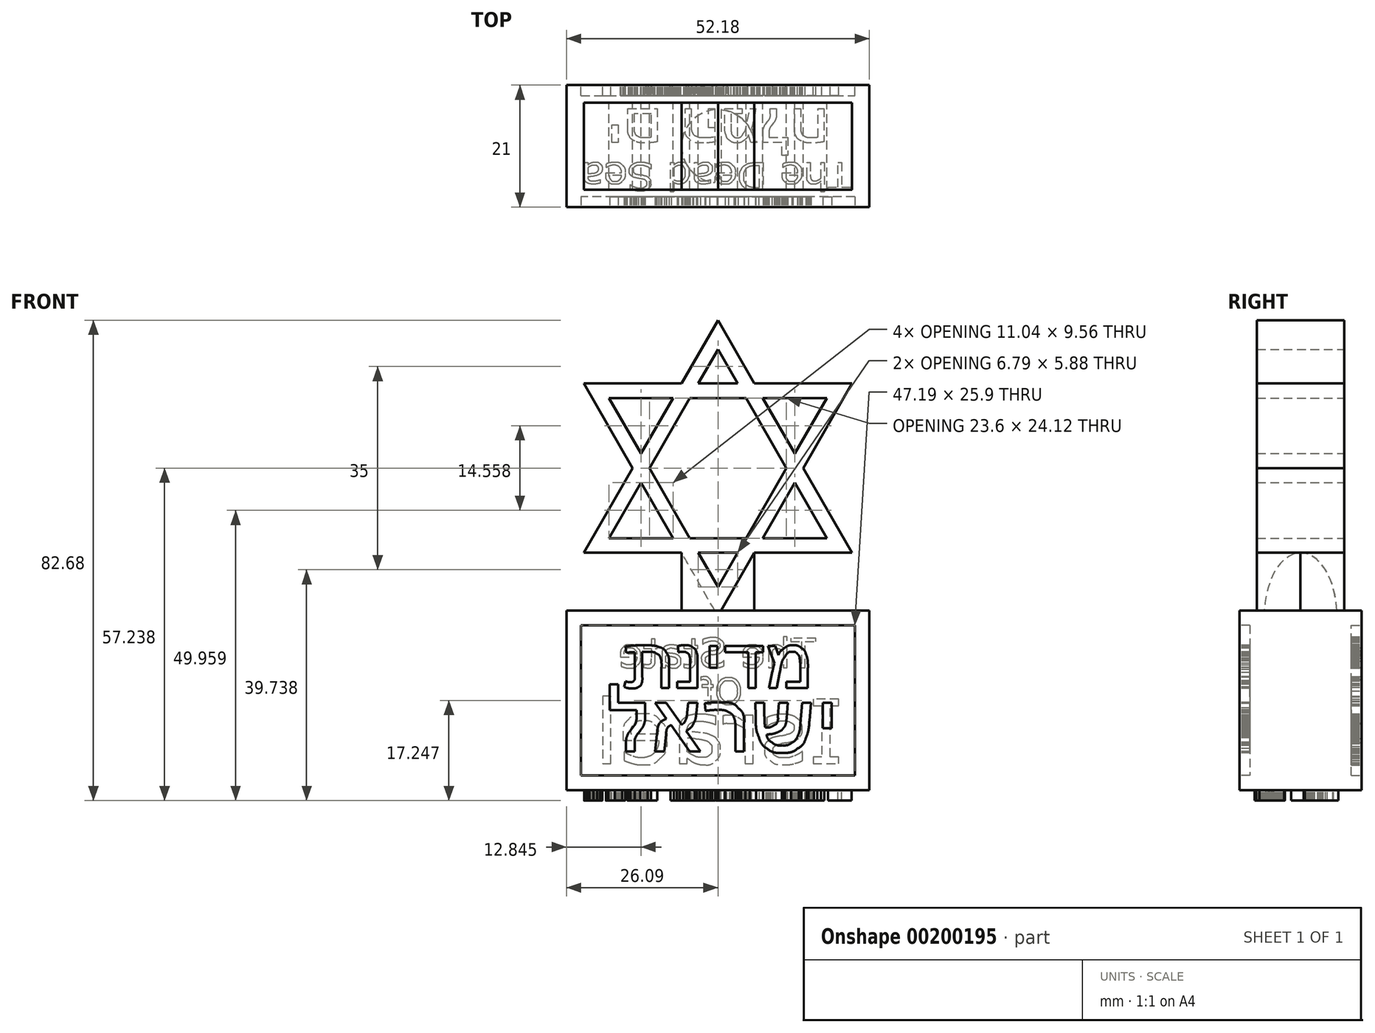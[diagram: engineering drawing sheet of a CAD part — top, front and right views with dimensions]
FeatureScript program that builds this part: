
annotation { "Feature Type Name" : "Feature", "Feature Type Description" : "" }
export const myFeature = defineFeature(function(context is Context, id is Id, definition is map)
    precondition{}
    {
        {
            var Q0;
            Q0=qCreatedBy(makeId("Front.planeOp"),FACE);
            var sketch = newSketch(context, id + "F0", { "sketchPlane" : qUnion([Q0])});
            skLineSegment(sketch, "E0", {"start": v(0, 0) * mm, "end": v(6.28, -10.88) * mm});
            skLineSegment(sketch, "E1", {"start": v(23.1, -40) * mm, "end": v(6.28, -40) * mm});
            skLineSegment(sketch, "E2", {"start": v(0, 0) * mm, "end": v(-6.28, -10.88) * mm});
            skLineSegment(sketch, "E3.0", {"start": v(0, -5) * mm, "end": v(-3.4, -10.88) * mm});
            skLineSegment(sketch, "E3.1", {"start": v(0, -5) * mm, "end": v(3.4, -10.88) * mm});
            skLineSegment(sketch, "E3.2", {"start": v(18.76, -37.5) * mm, "end": v(7.73, -37.5) * mm});
            skLineSegment(sketch, "E4", {"start": v(0, 0) * mm, "end": v(0, -40) * mm, "construction": true});
            skPoint(sketch, "E5", {"position": v(0, -20) * mm});
            skPoint(sketch, "E6", {"position": v(0, -10.88) * mm});
            skLineSegment(sketch, "E7", {"start": v(0, -10.88) * mm, "end": v(3.4, -10.88) * mm});
            skLineSegment(sketch, "E8", {"start": v(0, -40) * mm, "end": v(0, -57.57) * mm, "construction": true});
            skPoint(sketch, "E9", {"position": v(0, -50.88) * mm});
            skLineSegment(sketch, "E10", {"start": v(23.1, -10.88) * mm, "end": v(14.69, -25.44) * mm});
            skLineSegment(sketch, "E11", {"start": v(0, -10.88) * mm, "end": v(-3.4, -10.88) * mm});
            skLineSegment(sketch, "E12", {"start": v(-23.1, -10.88) * mm, "end": v(-14.69, -25.44) * mm});
            skLineSegment(sketch, "E13.0", {"start": v(18.76, -13.38) * mm, "end": v(13.25, -22.94) * mm});
            skLineSegment(sketch, "E14.0", {"start": v(11.19, -13.38) * mm, "end": v(18.76, -13.38) * mm});
            skLineSegment(sketch, "E14.1", {"start": v(11.19, -13.38) * mm, "end": v(7.73, -13.38) * mm});
            skLineSegment(sketch, "E15", {"start": v(-11.9, -13.38) * mm, "end": v(-18.76, -13.38) * mm});
            skLineSegment(sketch, "E16.trimOffspring", {"start": v(-18.76, -13.38) * mm, "end": v(-13.25, -22.94) * mm});
            skLineSegment(sketch, "E17.trimOffspring", {"start": v(4.84, -13.38) * mm, "end": v(11.8, -25.44) * mm});
            skLineSegment(sketch, "E18.trimOffspring", {"start": v(6.28, -10.88) * mm, "end": v(23.1, -10.88) * mm});
            skLineSegment(sketch, "E19.trimOffspring", {"start": v(7.73, -13.38) * mm, "end": v(13.25, -22.94) * mm});
            skLineSegment(sketch, "E20.trimOffspring", {"start": v(4.84, -13.38) * mm, "end": v(-4.84, -13.38) * mm});
            skLineSegment(sketch, "E21.trimOffspring", {"start": v(11.8, -25.44) * mm, "end": v(4.84, -37.5) * mm});
            skLineSegment(sketch, "E22.trimOffspring", {"start": v(14.69, -25.44) * mm, "end": v(23.1, -40) * mm});
            skLineSegment(sketch, "E23.trimOffspring", {"start": v(13.25, -27.94) * mm, "end": v(18.76, -37.5) * mm});
            skLineSegment(sketch, "E24.trimOffspring", {"start": v(13.25, -27.94) * mm, "end": v(7.73, -37.5) * mm});
            skLineSegment(sketch, "E25.trimOffspring", {"start": v(-7.73, -13.38) * mm, "end": v(-13.25, -22.94) * mm});
            skLineSegment(sketch, "E26.trimOffspring", {"start": v(-6.28, -10.88) * mm, "end": v(-23.1, -10.88) * mm});
            skLineSegment(sketch, "E27.trimOffspring", {"start": v(-4.84, -13.38) * mm, "end": v(-11.8, -25.44) * mm});
            skLineSegment(sketch, "E28.trimOffspring", {"start": v(-7.73, -13.38) * mm, "end": v(-11.9, -13.38) * mm});
            skLineSegment(sketch, "E29.trimOffspring", {"start": v(-14.69, -25.44) * mm, "end": v(-23.1, -40) * mm});
            skLineSegment(sketch, "E30.trimOffspring", {"start": v(-13.25, -27.94) * mm, "end": v(-18.76, -37.5) * mm});
            skLineSegment(sketch, "E31.trimOffspring", {"start": v(-13.25, -27.94) * mm, "end": v(-7.73, -37.5) * mm});
            skLineSegment(sketch, "E32.trimOffspring", {"start": v(-11.8, -25.44) * mm, "end": v(-4.84, -37.5) * mm});
            skLineSegment(sketch, "E33.trimOffspring", {"start": v(-6.28, -40) * mm, "end": v(0, -50.88) * mm});
            skLineSegment(sketch, "E34.trimOffspring", {"start": v(-7.73, -37.5) * mm, "end": v(-18.76, -37.5) * mm});
            skLineSegment(sketch, "E35.trimOffspring", {"start": v(-3.4, -40) * mm, "end": v(0, -45.88) * mm});
            skLineSegment(sketch, "E36.trimOffspring", {"start": v(-6.28, -40) * mm, "end": v(-23.1, -40) * mm});
            skLineSegment(sketch, "E37.trimOffspring", {"start": v(3.4, -40) * mm, "end": v(0, -45.88) * mm});
            skLineSegment(sketch, "E38.trimOffspring", {"start": v(4.84, -37.5) * mm, "end": v(-4.84, -37.5) * mm});
            skLineSegment(sketch, "E39.trimOffspring", {"start": v(6.28, -40) * mm, "end": v(0, -50.88) * mm});
            skLineSegment(sketch, "E40.trimOffspring", {"start": v(3.4, -40) * mm, "end": v(-3.4, -40) * mm});
            skSolve(sketch);
        }
        {
            var Q0;
            Q0=makeQuery(id+"F0.imprint","IMPRINT",FACE,{"disambiguationData":[TD([[makeQuery(id+"F0.imprint","IMPRINT",EDGE,{"derivedFrom":sQuery(id+"F0.wireOp",EDGE,"E0")}),-1.0]])]});
            extrude(context, id + "F1", {"entities" : qUnion([Q0]), "depth" : 15 * mm});
        }
        {
            var Q0;
            Q0=makeQuery(id+"F1.opExtrude","SWEPT_EDGE",EDGE,{"disambiguationData":[OSD([sQuery(id+"F0.wireOp",EDGE,"E33.trimOffspring"),sQuery(id+"F0.wireOp",EDGE,"E39.trimOffspring")])]});
            cPlane(context, id + "F2", {"entities" : qUnion([Q0]), "cplaneType" : CPlaneType.LINE_ANGLE, "offset" : 25 * mm, "angle" : 0 * degree, "width" : 150 * mm, "height" : 150 * mm});
        }
        {
            var Q0;
            Q0=qCreatedBy(id+"F2.planeOp",FACE);
            var sketch = newSketch(context, id + "F3", { "sketchPlane" : qUnion([Q0])});
            skLineSegment(sketch, "E41.0", {"start": v(-6.28, -15) * mm, "end": v(-6.28, 0) * mm});
            skLineSegment(sketch, "E42.0", {"start": v(0, -15) * mm, "end": v(0, 0) * mm});
            skLineSegment(sketch, "E43.0", {"start": v(6.28, -15) * mm, "end": v(6.28, 0) * mm});
            skLineSegment(sketch, "E44.0", {"start": v(6.28, 0) * mm, "end": v(0, 0) * mm});
            skLineSegment(sketch, "E45.0", {"start": v(-6.28, 0) * mm, "end": v(0, 0) * mm});
            skLineSegment(sketch, "E46.0", {"start": v(-6.28, -15) * mm, "end": v(0, -15) * mm});
            skLineSegment(sketch, "E47.0", {"start": v(6.28, -15) * mm, "end": v(0, -15) * mm});
            skPoint(sketch, "E48", {"position": v(0, -7.5) * mm});
            skCircle(sketch, "E49", {"center": v(0, -7.5) * mm, "radius": 6.28 * mm});
            skSolve(sketch);
        }
        {
            var Q0;
            {var subQ0=sQuery(id+"F3.wireOp",EDGE,"E49");var subQ1=sQuery(id+"F3.wireOp",EDGE,"E42.0");var subQ2=makeQuery(id+"F3.imprint","INTERSECT",VERTEX,{"disambiguationData":[OD(0.0)],"derivedFrom":[subQ1,subQ0]});Q0=makeQuery(id+"F3.imprint","IMPRINT",FACE,{"disambiguationData":[TD([[makeQuery(id+"F3.imprint","IMPRINT",EDGE,{"disambiguationData":[TD([[subQ2,-1.0]])],"derivedFrom":subQ1}),1.0]])]});}
            var Q1;
            Q1=makeQuery(id+"F1.opExtrude","SWEPT_FACE",FACE,{"disambiguationData":[OSD([sQuery(id+"F0.wireOp",EDGE,"E33.trimOffspring")])]});
            extrude(context, id + "F4", {"entities" : qUnion([Q0]), "operationType" : NewBodyOperationType.ADD, "endBound" : BoundingType.UP_TO_SURFACE, "endBoundEntityFace" : qUnion([Q1]), "depth" : 25 * mm});
        }
        {
            var Q0;
            {var subQ0=sQuery(id+"F3.wireOp",EDGE,"E49");var subQ1=sQuery(id+"F3.wireOp",EDGE,"E42.0");var subQ2=makeQuery(id+"F3.imprint","INTERSECT",VERTEX,{"disambiguationData":[OD(0.0)],"derivedFrom":[subQ1,subQ0]});Q0=makeQuery(id+"F3.imprint","IMPRINT",FACE,{"disambiguationData":[TD([[makeQuery(id+"F3.imprint","IMPRINT",EDGE,{"disambiguationData":[TD([[subQ2,-1.0]])],"derivedFrom":subQ1}),-1.0]])]});}
            var Q1;
            Q1=makeQuery(id+"F1.opExtrude","SWEPT_FACE",FACE,{"disambiguationData":[OSD([sQuery(id+"F0.wireOp",EDGE,"E39.trimOffspring")])]});
            extrude(context, id + "F5", {"entities" : qUnion([Q0]), "operationType" : NewBodyOperationType.ADD, "endBound" : BoundingType.UP_TO_SURFACE, "endBoundEntityFace" : qUnion([Q1]), "depth" : 25 * mm});
        }
        {
            var Q0;
            Q0=qCreatedBy(id+"F2.planeOp",FACE);
            var sketch = newSketch(context, id + "F6", { "sketchPlane" : qUnion([Q0])});
            skLineSegment(sketch, "E50.0", {"start": v(-6.28, 3) * mm, "end": v(-26.1, 3) * mm});
            skLineSegment(sketch, "E50.1", {"start": v(-26.1, -18) * mm, "end": v(-26.1, 3) * mm});
            skLineSegment(sketch, "E50.2", {"start": v(-6.28, -18) * mm, "end": v(-26.1, -18) * mm});
            skLineSegment(sketch, "E51.0", {"start": v(26.1, -18) * mm, "end": v(6.28, -18) * mm});
            skLineSegment(sketch, "E51.1", {"start": v(26.1, -18) * mm, "end": v(26.1, 3) * mm});
            skLineSegment(sketch, "E51.2", {"start": v(26.1, 3) * mm, "end": v(6.28, 3) * mm});
            skLineSegment(sketch, "E52", {"start": v(-6.28, -18) * mm, "end": v(6.28, -18) * mm});
            skLineSegment(sketch, "E53", {"start": v(6.28, 3) * mm, "end": v(-6.28, 3) * mm});
            skPoint(sketch, "E54.0.start.orphan", {"position": v(-6.28, -15) * mm});
            skPoint(sketch, "E55.0.start.orphan", {"position": v(-23.1, -15) * mm});
            skPoint(sketch, "E56.0.end.orphan", {"position": v(-23.1, 0) * mm});
            skPoint(sketch, "E56.0.start.orphan", {"position": v(-6.28, 0) * mm});
            skPoint(sketch, "E57.0.end.orphan", {"position": v(6.28, 0) * mm});
            skPoint(sketch, "E58.0.end.orphan", {"position": v(6.28, -15) * mm});
            skPoint(sketch, "E59.0.end.orphan", {"position": v(23.1, 0) * mm});
            skPoint(sketch, "E59.0.start.orphan", {"position": v(23.1, -15) * mm});
            skSolve(sketch);
        }
        {
            var Q0;
            Q0=qCreatedBy(id+"F2.planeOp",FACE);
            cPlane(context, id + "F7", {"entities" : qUnion([Q0]), "cplaneType" : CPlaneType.OFFSET, "offset" : 30 * mm, "oppositeDirection" : true, "width" : 150 * mm, "height" : 150 * mm});
        }
        {
            var Q0;
            Q0=qCreatedBy(id+"F7.planeOp",FACE);
            var sketch = newSketch(context, id + "F8", { "sketchPlane" : qUnion([Q0])});
            skLineSegment(sketch, "E60.0", {"start": v(-6.28, 3) * mm, "end": v(-26.1, 3) * mm});
            skLineSegment(sketch, "E61.0", {"start": v(-26.1, -18) * mm, "end": v(-26.1, 3) * mm});
            skLineSegment(sketch, "E62.0", {"start": v(6.28, 3) * mm, "end": v(-6.28, 3) * mm});
            skLineSegment(sketch, "E63.0", {"start": v(-6.28, -18) * mm, "end": v(6.28, -18) * mm});
            skLineSegment(sketch, "E64.0", {"start": v(26.1, -18) * mm, "end": v(6.28, -18) * mm});
            skLineSegment(sketch, "E65.0", {"start": v(26.1, -18) * mm, "end": v(26.1, 3) * mm});
            skLineSegment(sketch, "E66.0", {"start": v(26.1, 3) * mm, "end": v(6.28, 3) * mm});
            skLineSegment(sketch, "E67.0", {"start": v(-6.28, -18) * mm, "end": v(-26.1, -18) * mm});
            skSolve(sketch);
        }
        {
            var Q0;
            Q0 = qSketchRegion(id + "F8", true);
            extrude(context, id + "F9", {"entities" : qUnion([Q0]), "operationType" : NewBodyOperationType.ADD, "depth" : 30.9 * mm});
        }
        {
            var Q0;
            Q0=makeQuery(id+"F9.opExtrude","SWEPT_FACE",FACE,{"disambiguationData":[OSD([sQuery(id+"F8.wireOp",EDGE,"E63.0"),sQuery(id+"F8.wireOp",EDGE,"E64.0"),sQuery(id+"F8.wireOp",EDGE,"E67.0")])]});
            var sketch = newSketch(context, id + "F10", { "sketchPlane" : qUnion([Q0])});
            skLineSegment(sketch, "E68.0", {"start": v(26.1, -49.98) * mm, "end": v(-26.1, -49.98) * mm});
            skLineSegment(sketch, "E69.0", {"start": v(-26.1, -49.98) * mm, "end": v(-26.1, -80.88) * mm});
            skLineSegment(sketch, "E70.0", {"start": v(26.1, -49.98) * mm, "end": v(26.1, -80.88) * mm});
            skLineSegment(sketch, "E71.0", {"start": v(26.1, -80.88) * mm, "end": v(-26.1, -80.88) * mm});
            skLineSegment(sketch, "E72.0", {"start": v(23.6, -52.48) * mm, "end": v(-23.6, -52.48) * mm});
            skLineSegment(sketch, "E72.1", {"start": v(23.6, -52.48) * mm, "end": v(23.6, -78.38) * mm});
            skLineSegment(sketch, "E72.2", {"start": v(23.6, -78.38) * mm, "end": v(-23.6, -78.38) * mm});
            skLineSegment(sketch, "E72.3", {"start": v(-23.6, -52.48) * mm, "end": v(-23.6, -78.38) * mm});
            skLineSegment(sketch, "E73", {"start": v(9.73, -59.07) * mm, "end": v(8.6, -56.04) * mm});
            skLineSegment(sketch, "E74", {"start": v(8.6, -56.04) * mm, "end": v(9.89, -56.04) * mm});
            skLineSegment(sketch, "E75", {"start": v(9.89, -56.04) * mm, "end": v(10.42, -57.64) * mm});
            skFitSpline(sketch, "E76", {"points": [v(10.42, -57.64) * mm, v(10.64, -57.17) * mm, v(10.97, -56.77) * mm, v(11.43, -56.45) * mm]});
            skFitSpline(sketch, "E77", {"points": [v(11.43, -56.45) * mm, v(11.88, -56.12) * mm, v(12.37, -55.96) * mm, v(12.9, -55.96) * mm]});
            skFitSpline(sketch, "E78", {"points": [v(12.9, -55.96) * mm, v(13.45, -55.96) * mm, v(13.93, -56.1) * mm, v(14.33, -56.39) * mm]});
            skFitSpline(sketch, "E79", {"points": [v(14.33, -56.39) * mm, v(14.74, -56.67) * mm, v(15.03, -57.08) * mm, v(15.22, -57.63) * mm]});
            skFitSpline(sketch, "E80", {"points": [v(15.22, -57.63) * mm, v(15.4, -58.18) * mm, v(15.49, -59) * mm, v(15.49, -60.1) * mm]});
            skLineSegment(sketch, "E81", {"start": v(15.49, -60.1) * mm, "end": v(15.49, -63.3) * mm});
            skLineSegment(sketch, "E82", {"start": v(15.49, -63.3) * mm, "end": v(11.75, -63.3) * mm});
            skLineSegment(sketch, "E83", {"start": v(11.75, -63.3) * mm, "end": v(11.75, -62.2) * mm});
            skLineSegment(sketch, "E84", {"start": v(11.75, -62.2) * mm, "end": v(14.17, -62.2) * mm});
            skLineSegment(sketch, "E85", {"start": v(14.17, -62.2) * mm, "end": v(14.17, -60.07) * mm});
            skFitSpline(sketch, "E86", {"points": [v(14.17, -60.07) * mm, v(14.17, -59.27) * mm, v(14.14, -58.69) * mm, v(14.09, -58.32) * mm]});
            skFitSpline(sketch, "E87", {"points": [v(14.09, -58.32) * mm, v(14.04, -57.95) * mm, v(13.9, -57.65) * mm, v(13.68, -57.43) * mm]});
            skFitSpline(sketch, "E88", {"points": [v(13.68, -57.43) * mm, v(13.47, -57.2) * mm, v(13.2, -57.08) * mm, v(12.87, -57.08) * mm]});
            skFitSpline(sketch, "E89", {"points": [v(12.87, -57.08) * mm, v(12.36, -57.08) * mm, v(11.92, -57.34) * mm, v(11.56, -57.87) * mm]});
            skFitSpline(sketch, "E90", {"points": [v(11.56, -57.87) * mm, v(11.2, -58.4) * mm, v(10.9, -59.3) * mm, v(10.65, -60.6) * mm]});
            skLineSegment(sketch, "E91", {"start": v(10.65, -60.6) * mm, "end": v(10.14, -63.3) * mm});
            skLineSegment(sketch, "E92", {"start": v(10.14, -63.3) * mm, "end": v(8.82, -63.3) * mm});
            skLineSegment(sketch, "E93", {"start": v(8.82, -63.3) * mm, "end": v(9.4, -60.46) * mm});
            skFitSpline(sketch, "E94", {"points": [v(9.4, -60.46) * mm, v(9.45, -60.2) * mm, v(9.56, -59.73) * mm, v(9.73, -59.07) * mm]});
            skLineSegment(sketch, "E95", {"start": v(7.76, -57.13) * mm, "end": v(6.52, -57.13) * mm});
            skLineSegment(sketch, "E96", {"start": v(6.52, -57.13) * mm, "end": v(6.52, -63.3) * mm});
            skLineSegment(sketch, "E97", {"start": v(6.52, -63.3) * mm, "end": v(5.22, -63.3) * mm});
            skLineSegment(sketch, "E98", {"start": v(5.22, -63.3) * mm, "end": v(5.22, -57.13) * mm});
            skLineSegment(sketch, "E99", {"start": v(5.22, -57.13) * mm, "end": v(1.26, -57.13) * mm});
            skLineSegment(sketch, "E100", {"start": v(1.26, -57.13) * mm, "end": v(1.26, -56.04) * mm});
            skLineSegment(sketch, "E101", {"start": v(1.26, -56.04) * mm, "end": v(7.76, -56.04) * mm});
            skLineSegment(sketch, "E102", {"start": v(7.76, -56.04) * mm, "end": v(7.76, -57.13) * mm});
            skLineSegment(sketch, "E103", {"start": v(-0.07, -56.04) * mm, "end": v(-0.07, -59.8) * mm});
            skLineSegment(sketch, "E104", {"start": v(-0.07, -59.8) * mm, "end": v(-1.4, -59.8) * mm});
            skLineSegment(sketch, "E105", {"start": v(-1.4, -59.8) * mm, "end": v(-1.4, -56.04) * mm});
            skLineSegment(sketch, "E106", {"start": v(-1.4, -56.04) * mm, "end": v(-0.07, -56.04) * mm});
            skLineSegment(sketch, "E107", {"start": v(-3.5, -63.3) * mm, "end": v(-7, -63.3) * mm});
            skLineSegment(sketch, "E108", {"start": v(-7, -63.3) * mm, "end": v(-7, -62.2) * mm});
            skLineSegment(sketch, "E109", {"start": v(-7, -62.2) * mm, "end": v(-4.81, -62.2) * mm});
            skLineSegment(sketch, "E110", {"start": v(-4.81, -62.2) * mm, "end": v(-4.81, -58.64) * mm});
            skFitSpline(sketch, "E111", {"points": [v(-4.81, -58.64) * mm, v(-4.81, -58.25) * mm, v(-4.84, -57.95) * mm, v(-4.9, -57.75) * mm]});
            skFitSpline(sketch, "E112", {"points": [v(-4.9, -57.75) * mm, v(-4.96, -57.55) * mm, v(-5.09, -57.38) * mm, v(-5.29, -57.26) * mm]});
            skFitSpline(sketch, "E113", {"points": [v(-5.29, -57.26) * mm, v(-5.48, -57.14) * mm, v(-5.73, -57.08) * mm, v(-6.06, -57.08) * mm]});
            skFitSpline(sketch, "E114", {"points": [v(-6.06, -57.08) * mm, v(-6.34, -57.08) * mm, v(-6.58, -57.1) * mm, v(-6.8, -57.15) * mm]});
            skLineSegment(sketch, "E115", {"start": v(-6.8, -57.15) * mm, "end": v(-6.9, -56.1) * mm});
            skFitSpline(sketch, "E116", {"points": [v(-6.9, -56.1) * mm, v(-6.6, -56) * mm, v(-6.22, -55.96) * mm, v(-5.78, -55.96) * mm]});
            skFitSpline(sketch, "E117", {"points": [v(-5.78, -55.96) * mm, v(-5.16, -55.96) * mm, v(-4.68, -56.07) * mm, v(-4.36, -56.3) * mm]});
            skFitSpline(sketch, "E118", {"points": [v(-4.36, -56.3) * mm, v(-4.03, -56.54) * mm, v(-3.8, -56.82) * mm, v(-3.68, -57.17) * mm]});
            skFitSpline(sketch, "E119", {"points": [v(-3.68, -57.17) * mm, v(-3.57, -57.5) * mm, v(-3.5, -57.98) * mm, v(-3.5, -58.6) * mm]});
            skLineSegment(sketch, "E120", {"start": v(-3.5, -58.6) * mm, "end": v(-3.5, -63.3) * mm});
            skLineSegment(sketch, "E121", {"start": v(-16.14, -63.12) * mm, "end": v(-15.92, -62.14) * mm});
            skFitSpline(sketch, "E122", {"points": [v(-15.92, -62.14) * mm, v(-15.68, -62.23) * mm, v(-15.42, -62.27) * mm, v(-15.15, -62.27) * mm]});
            skFitSpline(sketch, "E123", {"points": [v(-15.15, -62.27) * mm, v(-14.83, -62.27) * mm, v(-14.61, -62.2) * mm, v(-14.5, -62.06) * mm]});
            skFitSpline(sketch, "E124", {"points": [v(-14.5, -62.06) * mm, v(-14.38, -61.92) * mm, v(-14.32, -61.67) * mm, v(-14.32, -61.3) * mm]});
            skLineSegment(sketch, "E125", {"start": v(-14.32, -61.3) * mm, "end": v(-14.32, -57.12) * mm});
            skFitSpline(sketch, "E126", {"points": [v(-14.32, -57.12) * mm, v(-14.71, -57.12) * mm, v(-15.2, -57.16) * mm, v(-15.76, -57.24) * mm]});
            skLineSegment(sketch, "E127", {"start": v(-15.76, -57.24) * mm, "end": v(-15.88, -56.15) * mm});
            skFitSpline(sketch, "E128", {"points": [v(-15.88, -56.15) * mm, v(-14.84, -56.02) * mm, v(-13.78, -55.96) * mm, v(-12.71, -55.96) * mm]});
            skFitSpline(sketch, "E129", {"points": [v(-12.71, -55.96) * mm, v(-11.63, -55.96) * mm, v(-10.8, -56.05) * mm, v(-10.2, -56.23) * mm]});
            skFitSpline(sketch, "E130", {"points": [v(-10.2, -56.23) * mm, v(-9.62, -56.41) * mm, v(-9.18, -56.75) * mm, v(-8.87, -57.23) * mm]});
            skFitSpline(sketch, "E131", {"points": [v(-8.87, -57.23) * mm, v(-8.56, -57.72) * mm, v(-8.4, -58.43) * mm, v(-8.4, -59.37) * mm]});
            skLineSegment(sketch, "E132", {"start": v(-8.4, -59.37) * mm, "end": v(-8.4, -63.3) * mm});
            skLineSegment(sketch, "E133", {"start": v(-8.4, -63.3) * mm, "end": v(-9.72, -63.3) * mm});
            skLineSegment(sketch, "E134", {"start": v(-9.72, -63.3) * mm, "end": v(-9.72, -59.72) * mm});
            skFitSpline(sketch, "E135", {"points": [v(-9.72, -59.72) * mm, v(-9.72, -59.02) * mm, v(-9.77, -58.5) * mm, v(-9.88, -58.17) * mm]});
            skFitSpline(sketch, "E136", {"points": [v(-9.88, -58.17) * mm, v(-9.98, -57.84) * mm, v(-10.22, -57.58) * mm, v(-10.58, -57.37) * mm]});
            skFitSpline(sketch, "E137", {"points": [v(-10.58, -57.37) * mm, v(-10.94, -57.17) * mm, v(-11.53, -57.06) * mm, v(-12.36, -57.06) * mm]});
            skLineSegment(sketch, "E138", {"start": v(-12.36, -57.06) * mm, "end": v(-13.02, -57.08) * mm});
            skLineSegment(sketch, "E139", {"start": v(-13.02, -57.08) * mm, "end": v(-13.02, -61.47) * mm});
            skFitSpline(sketch, "E140", {"points": [v(-13.02, -61.47) * mm, v(-13.02, -61.93) * mm, v(-13.06, -62.28) * mm, v(-13.15, -62.52) * mm]});
            skFitSpline(sketch, "E141", {"points": [v(-13.15, -62.52) * mm, v(-13.23, -62.76) * mm, v(-13.4, -62.96) * mm, v(-13.68, -63.12) * mm]});
            skFitSpline(sketch, "E142", {"points": [v(-13.68, -63.12) * mm, v(-13.94, -63.27) * mm, v(-14.34, -63.35) * mm, v(-14.86, -63.35) * mm]});
            skFitSpline(sketch, "E143", {"points": [v(-14.86, -63.35) * mm, v(-15.3, -63.35) * mm, v(-15.72, -63.27) * mm, v(-16.14, -63.12) * mm]});
            skLineSegment(sketch, "E144", {"start": v(19.6, -65.87) * mm, "end": v(19.6, -70.2) * mm});
            skLineSegment(sketch, "E145", {"start": v(19.6, -70.2) * mm, "end": v(18.06, -70.2) * mm});
            skLineSegment(sketch, "E146", {"start": v(18.06, -70.2) * mm, "end": v(18.06, -65.87) * mm});
            skLineSegment(sketch, "E147", {"start": v(18.06, -65.87) * mm, "end": v(19.6, -65.87) * mm});
            skLineSegment(sketch, "E148", {"start": v(7.95, -65.87) * mm, "end": v(7.98, -67.23) * mm});
            skFitSpline(sketch, "E149", {"points": [v(7.98, -67.23) * mm, v(8.01, -68.62) * mm, v(8.07, -69.58) * mm, v(8.16, -70.11) * mm]});
            skFitSpline(sketch, "E150", {"points": [v(8.16, -70.11) * mm, v(8.72, -70.11) * mm, v(9.22, -69.98) * mm, v(9.66, -69.7) * mm]});
            skFitSpline(sketch, "E151", {"points": [v(9.66, -69.7) * mm, v(10.11, -69.42) * mm, v(10.33, -68.9) * mm, v(10.33, -68.11) * mm]});
            skLineSegment(sketch, "E152", {"start": v(10.33, -68.11) * mm, "end": v(10.5, -65.87) * mm});
            skLineSegment(sketch, "E153", {"start": v(10.5, -65.87) * mm, "end": v(12.01, -65.87) * mm});
            skLineSegment(sketch, "E154", {"start": v(12.01, -65.87) * mm, "end": v(11.82, -68.5) * mm});
            skFitSpline(sketch, "E155", {"points": [v(11.82, -68.5) * mm, v(11.79, -68.95) * mm, v(11.74, -69.29) * mm, v(11.67, -69.52) * mm]});
            skFitSpline(sketch, "E156", {"points": [v(11.67, -69.52) * mm, v(11.6, -69.75) * mm, v(11.46, -70) * mm, v(11.25, -70.25) * mm]});
            skFitSpline(sketch, "E157", {"points": [v(11.25, -70.25) * mm, v(11.04, -70.5) * mm, v(10.7, -70.73) * mm, v(10.24, -70.93) * mm]});
            skFitSpline(sketch, "E158", {"points": [v(10.24, -70.93) * mm, v(9.78, -71.11) * mm, v(9.17, -71.24) * mm, v(8.39, -71.3) * mm]});
            skFitSpline(sketch, "E159", {"points": [v(8.39, -71.3) * mm, v(8.52, -71.87) * mm, v(8.82, -72.32) * mm, v(9.3, -72.67) * mm]});
            skFitSpline(sketch, "E160", {"points": [v(9.3, -72.67) * mm, v(9.78, -73) * mm, v(10.37, -73.18) * mm, v(11.07, -73.18) * mm]});
            skFitSpline(sketch, "E161", {"points": [v(11.07, -73.18) * mm, v(11.71, -73.18) * mm, v(12.26, -73.02) * mm, v(12.73, -72.72) * mm]});
            skFitSpline(sketch, "E162", {"points": [v(12.73, -72.72) * mm, v(13.19, -72.41) * mm, v(13.53, -72.01) * mm, v(13.75, -71.53) * mm]});
            skFitSpline(sketch, "E163", {"points": [v(13.75, -71.53) * mm, v(13.97, -71.04) * mm, v(14.12, -70.35) * mm, v(14.2, -69.45) * mm]});
            skLineSegment(sketch, "E164", {"start": v(14.2, -69.45) * mm, "end": v(14.53, -65.87) * mm});
            skLineSegment(sketch, "E165", {"start": v(14.53, -65.87) * mm, "end": v(16.04, -65.87) * mm});
            skLineSegment(sketch, "E166", {"start": v(16.04, -65.87) * mm, "end": v(15.76, -68.96) * mm});
            skFitSpline(sketch, "E167", {"points": [v(15.76, -68.96) * mm, v(15.65, -70.12) * mm, v(15.45, -71.1) * mm, v(15.17, -71.86) * mm]});
            skFitSpline(sketch, "E168", {"points": [v(15.17, -71.86) * mm, v(14.88, -72.63) * mm, v(14.4, -73.26) * mm, v(13.69, -73.74) * mm]});
            skFitSpline(sketch, "E169", {"points": [v(13.69, -73.74) * mm, v(12.99, -74.21) * mm, v(12.09, -74.45) * mm, v(10.98, -74.45) * mm]});
            skFitSpline(sketch, "E170", {"points": [v(10.98, -74.45) * mm, v(10, -74.45) * mm, v(9.17, -74.22) * mm, v(8.5, -73.74) * mm]});
            skFitSpline(sketch, "E171", {"points": [v(8.5, -73.74) * mm, v(7.85, -73.27) * mm, v(7.35, -72.59) * mm, v(7.02, -71.7) * mm]});
            skFitSpline(sketch, "E172", {"points": [v(7.02, -71.7) * mm, v(6.7, -70.82) * mm, v(6.53, -69.65) * mm, v(6.53, -68.18) * mm]});
            skLineSegment(sketch, "E173", {"start": v(6.53, -68.18) * mm, "end": v(6.42, -65.87) * mm});
            skLineSegment(sketch, "E174", {"start": v(6.42, -65.87) * mm, "end": v(7.95, -65.87) * mm});
            skFitSpline(sketch, "E175", {"points": [v(-2.27, -65.95) * mm, v(-1.46, -65.83) * mm, v(-0.72, -65.78) * mm, v(-0.04, -65.78) * mm]});
            skFitSpline(sketch, "E176", {"points": [v(-0.04, -65.78) * mm, v(1.65, -65.78) * mm, v(2.82, -66.1) * mm, v(3.48, -66.76) * mm]});
            skFitSpline(sketch, "E177", {"points": [v(3.48, -66.76) * mm, v(4.15, -67.41) * mm, v(4.48, -68.4) * mm, v(4.48, -69.71) * mm]});
            skLineSegment(sketch, "E178", {"start": v(4.48, -69.71) * mm, "end": v(4.48, -74.22) * mm});
            skLineSegment(sketch, "E179", {"start": v(4.48, -74.22) * mm, "end": v(2.99, -74.22) * mm});
            skLineSegment(sketch, "E180", {"start": v(2.99, -74.22) * mm, "end": v(2.99, -70.11) * mm});
            skFitSpline(sketch, "E181", {"points": [v(2.99, -70.11) * mm, v(2.99, -69.35) * mm, v(2.9, -68.78) * mm, v(2.74, -68.4) * mm]});
            skFitSpline(sketch, "E182", {"points": [v(2.74, -68.4) * mm, v(2.58, -68) * mm, v(2.27, -67.69) * mm, v(1.8, -67.45) * mm]});
            skFitSpline(sketch, "E183", {"points": [v(1.8, -67.45) * mm, v(1.35, -67.2) * mm, v(0.7, -67.08) * mm, v(-0.13, -67.08) * mm]});
            skFitSpline(sketch, "E184", {"points": [v(-0.13, -67.08) * mm, v(-0.7, -67.08) * mm, v(-1.36, -67.14) * mm, v(-2.14, -67.24) * mm]});
            skLineSegment(sketch, "E185", {"start": v(-2.14, -67.24) * mm, "end": v(-2.27, -65.95) * mm});
            skLineSegment(sketch, "E186", {"start": v(-3.01, -74.22) * mm, "end": v(-4.87, -74.22) * mm});
            skLineSegment(sketch, "E187", {"start": v(-4.87, -74.22) * mm, "end": v(-8.06, -69.71) * mm});
            skFitSpline(sketch, "E188", {"points": [v(-8.06, -69.71) * mm, v(-8.55, -69.98) * mm, v(-8.84, -70.52) * mm, v(-8.93, -71.33) * mm]});
            skLineSegment(sketch, "E189", {"start": v(-8.93, -71.33) * mm, "end": v(-9.27, -74.22) * mm});
            skLineSegment(sketch, "E190", {"start": v(-9.27, -74.22) * mm, "end": v(-10.83, -74.22) * mm});
            skLineSegment(sketch, "E191", {"start": v(-10.83, -74.22) * mm, "end": v(-10.49, -71.33) * mm});
            skFitSpline(sketch, "E192", {"points": [v(-10.49, -71.33) * mm, v(-10.33, -70) * mm, v(-9.79, -69.08) * mm, v(-8.85, -68.61) * mm]});
            skLineSegment(sketch, "E193", {"start": v(-8.85, -68.61) * mm, "end": v(-10.8, -65.87) * mm});
            skLineSegment(sketch, "E194", {"start": v(-10.8, -65.87) * mm, "end": v(-8.95, -65.87) * mm});
            skLineSegment(sketch, "E195", {"start": v(-8.95, -65.87) * mm, "end": v(-6.27, -69.61) * mm});
            skFitSpline(sketch, "E196", {"points": [v(-6.27, -69.61) * mm, v(-5.94, -69.4) * mm, v(-5.72, -69.15) * mm, v(-5.6, -68.89) * mm]});
            skFitSpline(sketch, "E197", {"points": [v(-5.6, -68.89) * mm, v(-5.46, -68.61) * mm, v(-5.36, -68.17) * mm, v(-5.29, -67.55) * mm]});
            skLineSegment(sketch, "E198", {"start": v(-5.29, -67.55) * mm, "end": v(-5.09, -65.87) * mm});
            skLineSegment(sketch, "E199", {"start": v(-5.09, -65.87) * mm, "end": v(-3.53, -65.87) * mm});
            skLineSegment(sketch, "E200", {"start": v(-3.53, -65.87) * mm, "end": v(-3.72, -67.6) * mm});
            skFitSpline(sketch, "E201", {"points": [v(-3.72, -67.6) * mm, v(-3.8, -68.34) * mm, v(-3.97, -68.94) * mm, v(-4.22, -69.42) * mm]});
            skFitSpline(sketch, "E202", {"points": [v(-4.22, -69.42) * mm, v(-4.47, -69.9) * mm, v(-4.9, -70.32) * mm, v(-5.51, -70.69) * mm]});
            skLineSegment(sketch, "E203", {"start": v(-5.51, -70.69) * mm, "end": v(-3.01, -74.22) * mm});
            skLineSegment(sketch, "E204", {"start": v(-17.15, -65.87) * mm, "end": v(-12.52, -65.87) * mm});
            skLineSegment(sketch, "E205", {"start": v(-12.52, -65.87) * mm, "end": v(-12.52, -67.95) * mm});
            skFitSpline(sketch, "E206", {"points": [v(-12.52, -67.95) * mm, v(-12.52, -68.54) * mm, v(-12.58, -69.01) * mm, v(-12.69, -69.38) * mm]});
            skFitSpline(sketch, "E207", {"points": [v(-12.69, -69.38) * mm, v(-12.8, -69.74) * mm, v(-12.99, -70.11) * mm, v(-13.26, -70.48) * mm]});
            skLineSegment(sketch, "E208", {"start": v(-13.26, -70.48) * mm, "end": v(-13.69, -71.05) * mm});
            skFitSpline(sketch, "E209", {"points": [v(-13.69, -71.05) * mm, v(-14.11, -71.62) * mm, v(-14.32, -72.23) * mm, v(-14.32, -72.89) * mm]});
            skLineSegment(sketch, "E210", {"start": v(-14.32, -72.89) * mm, "end": v(-14.32, -74.22) * mm});
            skLineSegment(sketch, "E211", {"start": v(-14.32, -74.22) * mm, "end": v(-15.83, -74.22) * mm});
            skLineSegment(sketch, "E212", {"start": v(-15.83, -74.22) * mm, "end": v(-15.83, -73.1) * mm});
            skFitSpline(sketch, "E213", {"points": [v(-15.83, -73.1) * mm, v(-15.83, -72.42) * mm, v(-15.76, -71.91) * mm, v(-15.63, -71.57) * mm]});
            skFitSpline(sketch, "E214", {"points": [v(-15.63, -71.57) * mm, v(-15.5, -71.23) * mm, v(-15.3, -70.9) * mm, v(-15.04, -70.56) * mm]});
            skLineSegment(sketch, "E215", {"start": v(-15.04, -70.56) * mm, "end": v(-14.57, -69.96) * mm});
            skFitSpline(sketch, "E216", {"points": [v(-14.57, -69.96) * mm, v(-14.34, -69.67) * mm, v(-14.19, -69.4) * mm, v(-14.13, -69.17) * mm]});
            skFitSpline(sketch, "E217", {"points": [v(-14.13, -69.17) * mm, v(-14.06, -68.93) * mm, v(-14.02, -68.63) * mm, v(-14.02, -68.26) * mm]});
            skLineSegment(sketch, "E218", {"start": v(-14.02, -68.26) * mm, "end": v(-14.02, -67.13) * mm});
            skLineSegment(sketch, "E219", {"start": v(-14.02, -67.13) * mm, "end": v(-18.65, -67.13) * mm});
            skLineSegment(sketch, "E220", {"start": v(-18.65, -67.13) * mm, "end": v(-18.65, -62.68) * mm});
            skLineSegment(sketch, "E221", {"start": v(-18.65, -62.68) * mm, "end": v(-17.15, -62.68) * mm});
            skLineSegment(sketch, "E222", {"start": v(-17.15, -62.68) * mm, "end": v(-17.15, -65.87) * mm});
            skSolve(sketch);
        }
        {
            var Q0;
            Q0=makeQuery(id+"F10.imprint","IMPRINT",FACE,{"disambiguationData":[TD([[makeQuery(id+"F10.imprint","IMPRINT",EDGE,{"derivedFrom":sQuery(id+"F10.wireOp",EDGE,"E72.0")}),1.0]])]});
            extrude(context, id + "F11", {"entities" : qUnion([Q0]), "operationType" : NewBodyOperationType.REMOVE, "oppositeDirection" : true, "depth" : 1.8 * mm});
        }
        {
            var Q0;
            Q0=makeQuery(id+"F9.opExtrude","SWEPT_FACE",FACE,{"disambiguationData":[OSD([sQuery(id+"F8.wireOp",EDGE,"E60.0"),sQuery(id+"F8.wireOp",EDGE,"E62.0"),sQuery(id+"F8.wireOp",EDGE,"E66.0")])]});
            var sketch = newSketch(context, id + "F12", { "sketchPlane" : qUnion([Q0])});
            skLineSegment(sketch, "E223.0.0", {"start": v(-23.6, -78.38) * mm, "end": v(-23.6, -52.48) * mm});
            skLineSegment(sketch, "E223.0.1", {"start": v(-23.6, -52.48) * mm, "end": v(23.6, -52.48) * mm});
            skLineSegment(sketch, "E223.0.2", {"start": v(23.6, -52.48) * mm, "end": v(23.6, -78.38) * mm});
            skLineSegment(sketch, "E223.0.3", {"start": v(23.6, -78.38) * mm, "end": v(-23.6, -78.38) * mm});
            skLineSegment(sketch, "E224", {"start": v(19.87, -76.3) * mm, "end": v(18.47, -76.3) * mm});
            skLineSegment(sketch, "E225", {"start": v(18.47, -76.3) * mm, "end": v(18.47, -64.72) * mm});
            skLineSegment(sketch, "E226", {"start": v(18.47, -64.72) * mm, "end": v(19.87, -64.72) * mm});
            skLineSegment(sketch, "E227", {"start": v(19.87, -64.72) * mm, "end": v(19.87, -76.3) * mm});
            skLineSegment(sketch, "E228", {"start": v(16.33, -72.3) * mm, "end": v(10.2, -72.3) * mm});
            skFitSpline(sketch, "E229", {"points": [v(10.2, -72.3) * mm, v(10.2, -72.8) * mm, v(10.28, -73.25) * mm, v(10.44, -73.63) * mm]});
            skFitSpline(sketch, "E230", {"points": [v(10.44, -73.63) * mm, v(10.6, -74) * mm, v(10.8, -74.32) * mm, v(11.07, -74.56) * mm]});
            skFitSpline(sketch, "E231", {"points": [v(11.07, -74.56) * mm, v(11.33, -74.8) * mm, v(11.63, -74.98) * mm, v(11.99, -75.1) * mm]});
            skFitSpline(sketch, "E232", {"points": [v(11.99, -75.1) * mm, v(12.34, -75.22) * mm, v(12.74, -75.28) * mm, v(13.16, -75.28) * mm]});
            skFitSpline(sketch, "E233", {"points": [v(13.16, -75.28) * mm, v(13.73, -75.28) * mm, v(14.3, -75.17) * mm, v(14.87, -74.94) * mm]});
            skFitSpline(sketch, "E234", {"points": [v(14.87, -74.94) * mm, v(15.44, -74.71) * mm, v(15.85, -74.5) * mm, v(16.1, -74.27) * mm]});
            skLineSegment(sketch, "E235", {"start": v(16.1, -74.27) * mm, "end": v(16.17, -74.27) * mm});
            skLineSegment(sketch, "E236", {"start": v(16.17, -74.27) * mm, "end": v(16.17, -75.8) * mm});
            skFitSpline(sketch, "E237", {"points": [v(16.17, -75.8) * mm, v(15.7, -76) * mm, v(15.22, -76.16) * mm, v(14.73, -76.3) * mm]});
            skFitSpline(sketch, "E238", {"points": [v(14.73, -76.3) * mm, v(14.23, -76.43) * mm, v(13.72, -76.5) * mm, v(13.18, -76.5) * mm]});
            skFitSpline(sketch, "E239", {"points": [v(13.18, -76.5) * mm, v(11.8, -76.5) * mm, v(10.72, -76.13) * mm, v(9.95, -75.38) * mm]});
            skFitSpline(sketch, "E240", {"points": [v(9.95, -75.38) * mm, v(9.17, -74.63) * mm, v(8.79, -73.57) * mm, v(8.79, -72.2) * mm]});
            skFitSpline(sketch, "E241", {"points": [v(8.79, -72.2) * mm, v(8.79, -70.84) * mm, v(9.16, -69.76) * mm, v(9.9, -68.96) * mm]});
            skFitSpline(sketch, "E242", {"points": [v(9.9, -68.96) * mm, v(10.64, -68.16) * mm, v(11.62, -67.76) * mm, v(12.83, -67.76) * mm]});
            skFitSpline(sketch, "E243", {"points": [v(12.83, -67.76) * mm, v(13.95, -67.76) * mm, v(14.81, -68.09) * mm, v(15.42, -68.74) * mm]});
            skFitSpline(sketch, "E244", {"points": [v(15.42, -68.74) * mm, v(16.03, -69.4) * mm, v(16.33, -70.33) * mm, v(16.33, -71.53) * mm]});
            skLineSegment(sketch, "E245", {"start": v(16.33, -71.53) * mm, "end": v(16.33, -72.3) * mm});
            skFitSpline(sketch, "E246", {"points": [v(14.97, -71.22) * mm, v(14.97, -70.49) * mm, v(14.78, -69.92) * mm, v(14.41, -69.52) * mm]});
            skFitSpline(sketch, "E247", {"points": [v(14.41, -69.52) * mm, v(14.05, -69.12) * mm, v(13.5, -68.91) * mm, v(12.75, -68.91) * mm]});
            skFitSpline(sketch, "E248", {"points": [v(12.75, -68.91) * mm, v(12, -68.91) * mm, v(11.4, -69.14) * mm, v(10.96, -69.58) * mm]});
            skFitSpline(sketch, "E249", {"points": [v(10.96, -69.58) * mm, v(10.52, -70.02) * mm, v(10.27, -70.57) * mm, v(10.2, -71.22) * mm]});
            skLineSegment(sketch, "E250", {"start": v(10.2, -71.22) * mm, "end": v(14.97, -71.22) * mm});
            skLineSegment(sketch, "E251", {"start": v(6.67, -76.3) * mm, "end": v(5.27, -76.3) * mm});
            skLineSegment(sketch, "E252", {"start": v(5.27, -76.3) * mm, "end": v(5.27, -75.42) * mm});
            skFitSpline(sketch, "E253", {"points": [v(5.27, -75.42) * mm, v(5.15, -75.5) * mm, v(4.98, -75.62) * mm, v(4.77, -75.78) * mm]});
            skFitSpline(sketch, "E254", {"points": [v(4.77, -75.78) * mm, v(4.56, -75.92) * mm, v(4.36, -76.04) * mm, v(4.16, -76.13) * mm]});
            skFitSpline(sketch, "E255", {"points": [v(4.16, -76.13) * mm, v(3.92, -76.25) * mm, v(3.66, -76.34) * mm, v(3.35, -76.42) * mm]});
            skFitSpline(sketch, "E256", {"points": [v(3.35, -76.42) * mm, v(3.05, -76.5) * mm, v(2.7, -76.54) * mm, v(2.29, -76.54) * mm]});
            skFitSpline(sketch, "E257", {"points": [v(2.29, -76.54) * mm, v(1.54, -76.54) * mm, v(0.9, -76.29) * mm, v(0.38, -75.8) * mm]});
            skFitSpline(sketch, "E258", {"points": [v(0.38, -75.8) * mm, v(-0.14, -75.3) * mm, v(-0.4, -74.66) * mm, v(-0.4, -73.9) * mm]});
            skFitSpline(sketch, "E259", {"points": [v(-0.4, -73.9) * mm, v(-0.4, -73.26) * mm, v(-0.26, -72.75) * mm, v(0, -72.37) * mm]});
            skFitSpline(sketch, "E260", {"points": [v(0, -72.37) * mm, v(0.28, -71.98) * mm, v(0.66, -71.67) * mm, v(1.17, -71.44) * mm]});
            skFitSpline(sketch, "E261", {"points": [v(1.17, -71.44) * mm, v(1.67, -71.22) * mm, v(2.28, -71.07) * mm, v(2.99, -71) * mm]});
            skFitSpline(sketch, "E262", {"points": [v(2.99, -71) * mm, v(3.7, -70.91) * mm, v(4.46, -70.85) * mm, v(5.27, -70.81) * mm]});
            skLineSegment(sketch, "E263", {"start": v(5.27, -70.81) * mm, "end": v(5.27, -70.6) * mm});
            skFitSpline(sketch, "E264", {"points": [v(5.27, -70.6) * mm, v(5.27, -70.28) * mm, v(5.22, -70.02) * mm, v(5.1, -69.8) * mm]});
            skFitSpline(sketch, "E265", {"points": [v(5.1, -69.8) * mm, v(5, -69.6) * mm, v(4.83, -69.44) * mm, v(4.63, -69.32) * mm]});
            skFitSpline(sketch, "E266", {"points": [v(4.63, -69.32) * mm, v(4.43, -69.2) * mm, v(4.19, -69.13) * mm, v(3.91, -69.09) * mm]});
            skFitSpline(sketch, "E267", {"points": [v(3.91, -69.09) * mm, v(3.63, -69.05) * mm, v(3.34, -69.03) * mm, v(3.04, -69.03) * mm]});
            skFitSpline(sketch, "E268", {"points": [v(3.04, -69.03) * mm, v(2.67, -69.03) * mm, v(2.26, -69.08) * mm, v(1.81, -69.17) * mm]});
            skFitSpline(sketch, "E269", {"points": [v(1.81, -69.17) * mm, v(1.36, -69.27) * mm, v(0.9, -69.4) * mm, v(0.41, -69.6) * mm]});
            skLineSegment(sketch, "E270", {"start": v(0.41, -69.6) * mm, "end": v(0.34, -69.6) * mm});
            skLineSegment(sketch, "E271", {"start": v(0.34, -69.6) * mm, "end": v(0.34, -68.17) * mm});
            skFitSpline(sketch, "E272", {"points": [v(0.34, -68.17) * mm, v(0.61, -68.1) * mm, v(1, -68.01) * mm, v(1.52, -67.92) * mm]});
            skFitSpline(sketch, "E273", {"points": [v(1.52, -67.92) * mm, v(2.04, -67.84) * mm, v(2.55, -67.8) * mm, v(3.05, -67.8) * mm]});
            skFitSpline(sketch, "E274", {"points": [v(3.05, -67.8) * mm, v(3.63, -67.8) * mm, v(4.14, -67.84) * mm, v(4.57, -67.94) * mm]});
            skFitSpline(sketch, "E275", {"points": [v(4.57, -67.94) * mm, v(5.01, -68.03) * mm, v(5.39, -68.2) * mm, v(5.7, -68.43) * mm]});
            skFitSpline(sketch, "E276", {"points": [v(5.7, -68.43) * mm, v(6.02, -68.66) * mm, v(6.26, -68.95) * mm, v(6.42, -69.32) * mm]});
            skFitSpline(sketch, "E277", {"points": [v(6.42, -69.32) * mm, v(6.58, -69.68) * mm, v(6.67, -70.13) * mm, v(6.67, -70.66) * mm]});
            skLineSegment(sketch, "E278", {"start": v(6.67, -70.66) * mm, "end": v(6.67, -76.3) * mm});
            skLineSegment(sketch, "E279", {"start": v(5.27, -74.26) * mm, "end": v(5.27, -71.94) * mm});
            skFitSpline(sketch, "E280", {"points": [v(5.27, -71.94) * mm, v(4.85, -71.97) * mm, v(4.34, -72) * mm, v(3.76, -72.06) * mm]});
            skFitSpline(sketch, "E281", {"points": [v(3.76, -72.06) * mm, v(3.19, -72.1) * mm, v(2.73, -72.18) * mm, v(2.4, -72.27) * mm]});
            skFitSpline(sketch, "E282", {"points": [v(2.4, -72.27) * mm, v(2, -72.38) * mm, v(1.67, -72.56) * mm, v(1.42, -72.8) * mm]});
            skFitSpline(sketch, "E283", {"points": [v(1.42, -72.8) * mm, v(1.17, -73.04) * mm, v(1.05, -73.37) * mm, v(1.05, -73.8) * mm]});
            skFitSpline(sketch, "E284", {"points": [v(1.05, -73.8) * mm, v(1.05, -74.27) * mm, v(1.2, -74.63) * mm, v(1.48, -74.88) * mm]});
            skFitSpline(sketch, "E285", {"points": [v(1.48, -74.88) * mm, v(1.77, -75.11) * mm, v(2.2, -75.23) * mm, v(2.8, -75.23) * mm]});
            skFitSpline(sketch, "E286", {"points": [v(2.8, -75.23) * mm, v(3.29, -75.23) * mm, v(3.74, -75.14) * mm, v(4.14, -74.95) * mm]});
            skFitSpline(sketch, "E287", {"points": [v(4.14, -74.95) * mm, v(4.55, -74.76) * mm, v(4.93, -74.53) * mm, v(5.27, -74.26) * mm]});
            skLineSegment(sketch, "E288", {"start": v(-0.86, -69.52) * mm, "end": v(-0.93, -69.52) * mm});
            skFitSpline(sketch, "E289", {"points": [v(-0.93, -69.52) * mm, v(-1.14, -69.47) * mm, v(-1.34, -69.43) * mm, v(-1.54, -69.41) * mm]});
            skFitSpline(sketch, "E290", {"points": [v(-1.54, -69.41) * mm, v(-1.74, -69.39) * mm, v(-1.97, -69.38) * mm, v(-2.24, -69.38) * mm]});
            skFitSpline(sketch, "E291", {"points": [v(-2.24, -69.38) * mm, v(-2.67, -69.38) * mm, v(-3.08, -69.47) * mm, v(-3.49, -69.67) * mm]});
            skFitSpline(sketch, "E292", {"points": [v(-3.49, -69.67) * mm, v(-3.89, -69.85) * mm, v(-4.27, -70.1) * mm, v(-4.65, -70.4) * mm]});
            skLineSegment(sketch, "E293", {"start": v(-4.65, -70.4) * mm, "end": v(-4.65, -76.3) * mm});
            skLineSegment(sketch, "E294", {"start": v(-4.65, -76.3) * mm, "end": v(-6.05, -76.3) * mm});
            skLineSegment(sketch, "E295", {"start": v(-6.05, -76.3) * mm, "end": v(-6.05, -68) * mm});
            skLineSegment(sketch, "E296", {"start": v(-6.05, -68) * mm, "end": v(-4.65, -68) * mm});
            skLineSegment(sketch, "E297", {"start": v(-4.65, -68) * mm, "end": v(-4.65, -69.22) * mm});
            skFitSpline(sketch, "E298", {"points": [v(-4.65, -69.22) * mm, v(-4.1, -68.77) * mm, v(-3.6, -68.46) * mm, v(-3.18, -68.27) * mm]});
            skFitSpline(sketch, "E299", {"points": [v(-3.18, -68.27) * mm, v(-2.75, -68.09) * mm, v(-2.32, -68) * mm, v(-1.88, -68) * mm]});
            skFitSpline(sketch, "E300", {"points": [v(-1.88, -68) * mm, v(-1.63, -68) * mm, v(-1.46, -68) * mm, v(-1.35, -68.01) * mm]});
            skFitSpline(sketch, "E301", {"points": [v(-1.35, -68.01) * mm, v(-1.24, -68.02) * mm, v(-1.08, -68.05) * mm, v(-0.86, -68.08) * mm]});
            skLineSegment(sketch, "E302", {"start": v(-0.86, -68.08) * mm, "end": v(-0.86, -69.52) * mm});
            skFitSpline(sketch, "E303", {"points": [v(-8.05, -73.9) * mm, v(-8.05, -74.67) * mm, v(-8.37, -75.29) * mm, v(-9, -75.78) * mm]});
            skFitSpline(sketch, "E304", {"points": [v(-9, -75.78) * mm, v(-9.63, -76.26) * mm, v(-10.48, -76.5) * mm, v(-11.57, -76.5) * mm]});
            skFitSpline(sketch, "E305", {"points": [v(-11.57, -76.5) * mm, v(-12.18, -76.5) * mm, v(-12.75, -76.43) * mm, v(-13.26, -76.29) * mm]});
            skFitSpline(sketch, "E306", {"points": [v(-13.26, -76.29) * mm, v(-13.78, -76.14) * mm, v(-14.2, -75.98) * mm, v(-14.55, -75.8) * mm]});
            skLineSegment(sketch, "E307", {"start": v(-14.55, -75.8) * mm, "end": v(-14.55, -74.24) * mm});
            skLineSegment(sketch, "E308", {"start": v(-14.55, -74.24) * mm, "end": v(-14.48, -74.24) * mm});
            skFitSpline(sketch, "E309", {"points": [v(-14.48, -74.24) * mm, v(-14.04, -74.57) * mm, v(-13.54, -74.83) * mm, v(-13, -75.03) * mm]});
            skFitSpline(sketch, "E310", {"points": [v(-13, -75.03) * mm, v(-12.46, -75.23) * mm, v(-11.94, -75.32) * mm, v(-11.45, -75.32) * mm]});
            skFitSpline(sketch, "E311", {"points": [v(-11.45, -75.32) * mm, v(-10.83, -75.32) * mm, v(-10.35, -75.22) * mm, v(-10, -75.02) * mm]});
            skFitSpline(sketch, "E312", {"points": [v(-10, -75.02) * mm, v(-9.66, -74.83) * mm, v(-9.48, -74.51) * mm, v(-9.48, -74.09) * mm]});
            skFitSpline(sketch, "E313", {"points": [v(-9.48, -74.09) * mm, v(-9.48, -73.76) * mm, v(-9.58, -73.51) * mm, v(-9.77, -73.34) * mm]});
            skFitSpline(sketch, "E314", {"points": [v(-9.77, -73.34) * mm, v(-9.95, -73.17) * mm, v(-10.32, -73.03) * mm, v(-10.85, -72.91) * mm]});
            skFitSpline(sketch, "E315", {"points": [v(-10.85, -72.91) * mm, v(-11.05, -72.87) * mm, v(-11.31, -72.81) * mm, v(-11.63, -72.75) * mm]});
            skFitSpline(sketch, "E316", {"points": [v(-11.63, -72.75) * mm, v(-11.95, -72.7) * mm, v(-12.24, -72.63) * mm, v(-12.5, -72.56) * mm]});
            skFitSpline(sketch, "E317", {"points": [v(-12.5, -72.56) * mm, v(-13.23, -72.37) * mm, v(-13.75, -72.08) * mm, v(-14.06, -71.71) * mm]});
            skFitSpline(sketch, "E318", {"points": [v(-14.06, -71.71) * mm, v(-14.36, -71.34) * mm, v(-14.51, -70.87) * mm, v(-14.51, -70.33) * mm]});
            skFitSpline(sketch, "E319", {"points": [v(-14.51, -70.33) * mm, v(-14.51, -69.99) * mm, v(-14.44, -69.66) * mm, v(-14.3, -69.36) * mm]});
            skFitSpline(sketch, "E320", {"points": [v(-14.3, -69.36) * mm, v(-14.16, -69.06) * mm, v(-13.95, -68.79) * mm, v(-13.66, -68.55) * mm]});
            skFitSpline(sketch, "E321", {"points": [v(-13.66, -68.55) * mm, v(-13.38, -68.32) * mm, v(-13.03, -68.13) * mm, v(-12.6, -68) * mm]});
            skFitSpline(sketch, "E322", {"points": [v(-12.6, -68) * mm, v(-12.17, -67.86) * mm, v(-11.69, -67.8) * mm, v(-11.16, -67.8) * mm]});
            skFitSpline(sketch, "E323", {"points": [v(-11.16, -67.8) * mm, v(-10.66, -67.8) * mm, v(-10.16, -67.85) * mm, v(-9.65, -67.98) * mm]});
            skFitSpline(sketch, "E324", {"points": [v(-9.65, -67.98) * mm, v(-9.14, -68.1) * mm, v(-8.72, -68.24) * mm, v(-8.38, -68.42) * mm]});
            skLineSegment(sketch, "E325", {"start": v(-8.38, -68.42) * mm, "end": v(-8.38, -69.91) * mm});
            skLineSegment(sketch, "E326", {"start": v(-8.38, -69.91) * mm, "end": v(-8.46, -69.91) * mm});
            skFitSpline(sketch, "E327", {"points": [v(-8.46, -69.91) * mm, v(-8.81, -69.65) * mm, v(-9.25, -69.43) * mm, v(-9.76, -69.25) * mm]});
            skFitSpline(sketch, "E328", {"points": [v(-9.76, -69.25) * mm, v(-10.27, -69.07) * mm, v(-10.77, -68.97) * mm, v(-11.26, -68.97) * mm]});
            skFitSpline(sketch, "E329", {"points": [v(-11.26, -68.97) * mm, v(-11.77, -68.97) * mm, v(-12.2, -69.07) * mm, v(-12.56, -69.27) * mm]});
            skFitSpline(sketch, "E330", {"points": [v(-12.56, -69.27) * mm, v(-12.9, -69.47) * mm, v(-13.09, -69.76) * mm, v(-13.09, -70.14) * mm]});
            skFitSpline(sketch, "E331", {"points": [v(-13.09, -70.14) * mm, v(-13.09, -70.48) * mm, v(-12.98, -70.74) * mm, v(-12.77, -70.92) * mm]});
            skFitSpline(sketch, "E332", {"points": [v(-12.77, -70.92) * mm, v(-12.56, -71.1) * mm, v(-12.22, -71.23) * mm, v(-11.75, -71.34) * mm]});
            skFitSpline(sketch, "E333", {"points": [v(-11.75, -71.34) * mm, v(-11.5, -71.4) * mm, v(-11.2, -71.46) * mm, v(-10.9, -71.52) * mm]});
            skFitSpline(sketch, "E334", {"points": [v(-10.9, -71.52) * mm, v(-10.57, -71.58) * mm, v(-10.3, -71.63) * mm, v(-10.09, -71.68) * mm]});
            skFitSpline(sketch, "E335", {"points": [v(-10.09, -71.68) * mm, v(-9.44, -71.83) * mm, v(-8.94, -72.09) * mm, v(-8.58, -72.45) * mm]});
            skFitSpline(sketch, "E336", {"points": [v(-8.58, -72.45) * mm, v(-8.23, -72.82) * mm, v(-8.05, -73.3) * mm, v(-8.05, -73.9) * mm]});
            skLineSegment(sketch, "E337", {"start": v(-16.4, -76.3) * mm, "end": v(-20.78, -76.3) * mm});
            skLineSegment(sketch, "E338", {"start": v(-20.78, -76.3) * mm, "end": v(-20.78, -75.17) * mm});
            skLineSegment(sketch, "E339", {"start": v(-20.78, -75.17) * mm, "end": v(-19.33, -75.17) * mm});
            skLineSegment(sketch, "E340", {"start": v(-19.33, -75.17) * mm, "end": v(-19.33, -66.35) * mm});
            skLineSegment(sketch, "E341", {"start": v(-19.33, -66.35) * mm, "end": v(-20.78, -66.35) * mm});
            skLineSegment(sketch, "E342", {"start": v(-20.78, -66.35) * mm, "end": v(-20.78, -65.22) * mm});
            skLineSegment(sketch, "E343", {"start": v(-20.78, -65.22) * mm, "end": v(-16.4, -65.22) * mm});
            skLineSegment(sketch, "E344", {"start": v(-16.4, -65.22) * mm, "end": v(-16.4, -66.35) * mm});
            skLineSegment(sketch, "E345", {"start": v(-16.4, -66.35) * mm, "end": v(-17.86, -66.35) * mm});
            skLineSegment(sketch, "E346", {"start": v(-17.86, -66.35) * mm, "end": v(-17.86, -75.17) * mm});
            skLineSegment(sketch, "E347", {"start": v(-17.86, -75.17) * mm, "end": v(-16.4, -75.17) * mm});
            skLineSegment(sketch, "E348", {"start": v(-16.4, -75.17) * mm, "end": v(-16.4, -76.3) * mm});
            skLineSegment(sketch, "E349", {"start": v(2.95, -61.94) * mm, "end": v(2.92, -61.94) * mm});
            skFitSpline(sketch, "E350", {"points": [v(2.92, -61.94) * mm, v(2.85, -61.92) * mm, v(2.77, -61.9) * mm, v(2.67, -61.89) * mm]});
            skFitSpline(sketch, "E351", {"points": [v(2.67, -61.89) * mm, v(2.57, -61.87) * mm, v(2.48, -61.86) * mm, v(2.4, -61.86) * mm]});
            skFitSpline(sketch, "E352", {"points": [v(2.4, -61.86) * mm, v(2.16, -61.86) * mm, v(1.99, -61.91) * mm, v(1.88, -62.02) * mm]});
            skFitSpline(sketch, "E353", {"points": [v(1.88, -62.02) * mm, v(1.77, -62.13) * mm, v(1.72, -62.32) * mm, v(1.72, -62.6) * mm]});
            skLineSegment(sketch, "E354", {"start": v(1.72, -62.6) * mm, "end": v(1.72, -62.71) * mm});
            skLineSegment(sketch, "E355", {"start": v(1.72, -62.71) * mm, "end": v(2.74, -62.71) * mm});
            skLineSegment(sketch, "E356", {"start": v(2.74, -62.71) * mm, "end": v(2.74, -63.19) * mm});
            skLineSegment(sketch, "E357", {"start": v(2.74, -63.19) * mm, "end": v(1.73, -63.19) * mm});
            skLineSegment(sketch, "E358", {"start": v(1.73, -63.19) * mm, "end": v(1.73, -66.07) * mm});
            skLineSegment(sketch, "E359", {"start": v(1.73, -66.07) * mm, "end": v(1.17, -66.07) * mm});
            skLineSegment(sketch, "E360", {"start": v(1.17, -66.07) * mm, "end": v(1.17, -63.19) * mm});
            skLineSegment(sketch, "E361", {"start": v(1.17, -63.19) * mm, "end": v(0.79, -63.19) * mm});
            skLineSegment(sketch, "E362", {"start": v(0.79, -63.19) * mm, "end": v(0.79, -62.71) * mm});
            skLineSegment(sketch, "E363", {"start": v(0.79, -62.71) * mm, "end": v(1.17, -62.71) * mm});
            skLineSegment(sketch, "E364", {"start": v(1.17, -62.71) * mm, "end": v(1.17, -62.6) * mm});
            skFitSpline(sketch, "E365", {"points": [v(1.17, -62.6) * mm, v(1.17, -62.2) * mm, v(1.27, -61.9) * mm, v(1.47, -61.69) * mm]});
            skFitSpline(sketch, "E366", {"points": [v(1.47, -61.69) * mm, v(1.66, -61.47) * mm, v(1.95, -61.36) * mm, v(2.33, -61.36) * mm]});
            skFitSpline(sketch, "E367", {"points": [v(2.33, -61.36) * mm, v(2.45, -61.36) * mm, v(2.57, -61.37) * mm, v(2.67, -61.38) * mm]});
            skFitSpline(sketch, "E368", {"points": [v(2.67, -61.38) * mm, v(2.77, -61.4) * mm, v(2.86, -61.4) * mm, v(2.95, -61.42) * mm]});
            skLineSegment(sketch, "E369", {"start": v(2.95, -61.42) * mm, "end": v(2.95, -61.94) * mm});
            skLineSegment(sketch, "E370", {"start": v(2.95, -61.94) * mm, "end": v(2.95, -61.94) * mm});
            skFitSpline(sketch, "E371", {"points": [v(-0.33, -62.1) * mm, v(-0.14, -62.3) * mm, v(0, -62.56) * mm, v(0.1, -62.85) * mm]});
            skFitSpline(sketch, "E372", {"points": [v(0.1, -62.85) * mm, v(0.19, -63.14) * mm, v(0.24, -63.47) * mm, v(0.24, -63.84) * mm]});
            skFitSpline(sketch, "E373", {"points": [v(0.24, -63.84) * mm, v(0.24, -64.2) * mm, v(0.19, -64.54) * mm, v(0.09, -64.83) * mm]});
            skFitSpline(sketch, "E374", {"points": [v(0.09, -64.83) * mm, v(0, -65.12) * mm, v(-0.15, -65.36) * mm, v(-0.33, -65.56) * mm]});
            skFitSpline(sketch, "E375", {"points": [v(-0.33, -65.56) * mm, v(-0.51, -65.76) * mm, v(-0.73, -65.91) * mm, v(-0.98, -66.01) * mm]});
            skFitSpline(sketch, "E376", {"points": [v(-0.98, -66.01) * mm, v(-1.23, -66.12) * mm, v(-1.52, -66.17) * mm, v(-1.84, -66.17) * mm]});
            skFitSpline(sketch, "E377", {"points": [v(-1.84, -66.17) * mm, v(-2.16, -66.17) * mm, v(-2.44, -66.11) * mm, v(-2.7, -66.01) * mm]});
            skFitSpline(sketch, "E378", {"points": [v(-2.7, -66.01) * mm, v(-2.96, -65.9) * mm, v(-3.18, -65.75) * mm, v(-3.36, -65.56) * mm]});
            skFitSpline(sketch, "E379", {"points": [v(-3.36, -65.56) * mm, v(-3.54, -65.36) * mm, v(-3.68, -65.11) * mm, v(-3.78, -64.83) * mm]});
            skFitSpline(sketch, "E380", {"points": [v(-3.78, -64.83) * mm, v(-3.87, -64.54) * mm, v(-3.92, -64.2) * mm, v(-3.92, -63.84) * mm]});
            skFitSpline(sketch, "E381", {"points": [v(-3.92, -63.84) * mm, v(-3.92, -63.47) * mm, v(-3.87, -63.14) * mm, v(-3.78, -62.86) * mm]});
            skFitSpline(sketch, "E382", {"points": [v(-3.78, -62.86) * mm, v(-3.68, -62.56) * mm, v(-3.54, -62.32) * mm, v(-3.36, -62.1) * mm]});
            skFitSpline(sketch, "E383", {"points": [v(-3.36, -62.1) * mm, v(-3.18, -61.91) * mm, v(-2.96, -61.76) * mm, v(-2.7, -61.66) * mm]});
            skFitSpline(sketch, "E384", {"points": [v(-2.7, -61.66) * mm, v(-2.44, -61.55) * mm, v(-2.15, -61.5) * mm, v(-1.84, -61.5) * mm]});
            skFitSpline(sketch, "E385", {"points": [v(-1.84, -61.5) * mm, v(-1.52, -61.5) * mm, v(-1.23, -61.55) * mm, v(-0.98, -61.66) * mm]});
            skFitSpline(sketch, "E386", {"points": [v(-0.98, -61.66) * mm, v(-0.72, -61.77) * mm, v(-0.5, -61.91) * mm, v(-0.33, -62.1) * mm]});
            skFitSpline(sketch, "E387", {"points": [v(-0.38, -63.84) * mm, v(-0.38, -63.25) * mm, v(-0.51, -62.8) * mm, v(-0.77, -62.5) * mm]});
            skFitSpline(sketch, "E388", {"points": [v(-0.77, -62.5) * mm, v(-1.03, -62.17) * mm, v(-1.39, -62.02) * mm, v(-1.84, -62.02) * mm]});
            skFitSpline(sketch, "E389", {"points": [v(-1.84, -62.02) * mm, v(-2.3, -62.02) * mm, v(-2.65, -62.17) * mm, v(-2.91, -62.5) * mm]});
            skFitSpline(sketch, "E390", {"points": [v(-2.91, -62.5) * mm, v(-3.17, -62.8) * mm, v(-3.3, -63.25) * mm, v(-3.3, -63.84) * mm]});
            skFitSpline(sketch, "E391", {"points": [v(-3.3, -63.84) * mm, v(-3.3, -64.42) * mm, v(-3.17, -64.87) * mm, v(-2.9, -65.19) * mm]});
            skFitSpline(sketch, "E392", {"points": [v(-2.9, -65.19) * mm, v(-2.64, -65.5) * mm, v(-2.28, -65.65) * mm, v(-1.84, -65.65) * mm]});
            skFitSpline(sketch, "E393", {"points": [v(-1.84, -65.65) * mm, v(-1.4, -65.65) * mm, v(-1.04, -65.5) * mm, v(-0.78, -65.19) * mm]});
            skFitSpline(sketch, "E394", {"points": [v(-0.78, -65.19) * mm, v(-0.51, -64.87) * mm, v(-0.38, -64.42) * mm, v(-0.38, -63.84) * mm]});
            skLineSegment(sketch, "E395", {"start": v(16.77, -57.95) * mm, "end": v(13.97, -57.95) * mm});
            skFitSpline(sketch, "E396", {"points": [v(13.97, -57.95) * mm, v(13.97, -58.18) * mm, v(14, -58.39) * mm, v(14.07, -58.56) * mm]});
            skFitSpline(sketch, "E397", {"points": [v(14.07, -58.56) * mm, v(14.14, -58.73) * mm, v(14.24, -58.88) * mm, v(14.36, -58.99) * mm]});
            skFitSpline(sketch, "E398", {"points": [v(14.36, -58.99) * mm, v(14.48, -59.1) * mm, v(14.62, -59.18) * mm, v(14.78, -59.23) * mm]});
            skFitSpline(sketch, "E399", {"points": [v(14.78, -59.23) * mm, v(14.94, -59.29) * mm, v(15.12, -59.31) * mm, v(15.32, -59.31) * mm]});
            skFitSpline(sketch, "E400", {"points": [v(15.32, -59.31) * mm, v(15.58, -59.31) * mm, v(15.84, -59.26) * mm, v(16.1, -59.16) * mm]});
            skFitSpline(sketch, "E401", {"points": [v(16.1, -59.16) * mm, v(16.36, -59.06) * mm, v(16.55, -58.95) * mm, v(16.66, -58.85) * mm]});
            skLineSegment(sketch, "E402", {"start": v(16.66, -58.85) * mm, "end": v(16.7, -58.85) * mm});
            skLineSegment(sketch, "E403", {"start": v(16.7, -58.85) * mm, "end": v(16.7, -59.55) * mm});
            skFitSpline(sketch, "E404", {"points": [v(16.7, -59.55) * mm, v(16.48, -59.64) * mm, v(16.26, -59.72) * mm, v(16.03, -59.78) * mm]});
            skFitSpline(sketch, "E405", {"points": [v(16.03, -59.78) * mm, v(15.8, -59.84) * mm, v(15.57, -59.87) * mm, v(15.33, -59.87) * mm]});
            skFitSpline(sketch, "E406", {"points": [v(15.33, -59.87) * mm, v(14.7, -59.87) * mm, v(14.2, -59.7) * mm, v(13.85, -59.36) * mm]});
            skFitSpline(sketch, "E407", {"points": [v(13.85, -59.36) * mm, v(13.5, -59.02) * mm, v(13.32, -58.53) * mm, v(13.32, -57.9) * mm]});
            skFitSpline(sketch, "E408", {"points": [v(13.32, -57.9) * mm, v(13.32, -57.28) * mm, v(13.49, -56.79) * mm, v(13.82, -56.42) * mm]});
            skFitSpline(sketch, "E409", {"points": [v(13.82, -56.42) * mm, v(14.16, -56.06) * mm, v(14.61, -55.87) * mm, v(15.17, -55.87) * mm]});
            skFitSpline(sketch, "E410", {"points": [v(15.17, -55.87) * mm, v(15.68, -55.87) * mm, v(16.07, -56.02) * mm, v(16.35, -56.32) * mm]});
            skFitSpline(sketch, "E411", {"points": [v(16.35, -56.32) * mm, v(16.63, -56.62) * mm, v(16.77, -57.05) * mm, v(16.77, -57.6) * mm]});
            skLineSegment(sketch, "E412", {"start": v(16.77, -57.6) * mm, "end": v(16.77, -57.95) * mm});
            skFitSpline(sketch, "E413", {"points": [v(16.15, -57.46) * mm, v(16.14, -57.12) * mm, v(16.06, -56.86) * mm, v(15.9, -56.68) * mm]});
            skFitSpline(sketch, "E414", {"points": [v(15.9, -56.68) * mm, v(15.73, -56.5) * mm, v(15.47, -56.4) * mm, v(15.13, -56.4) * mm]});
            skFitSpline(sketch, "E415", {"points": [v(15.13, -56.4) * mm, v(14.79, -56.4) * mm, v(14.51, -56.5) * mm, v(14.31, -56.7) * mm]});
            skFitSpline(sketch, "E416", {"points": [v(14.31, -56.7) * mm, v(14.1, -56.9) * mm, v(14, -57.16) * mm, v(13.97, -57.46) * mm]});
            skLineSegment(sketch, "E417", {"start": v(13.97, -57.46) * mm, "end": v(16.15, -57.46) * mm});
            skFitSpline(sketch, "E418", {"points": [v(12.8, -59.75) * mm, v(12.69, -59.78) * mm, v(12.56, -59.8) * mm, v(12.41, -59.83) * mm]});
            skFitSpline(sketch, "E419", {"points": [v(12.41, -59.83) * mm, v(12.27, -59.85) * mm, v(12.15, -59.86) * mm, v(12.04, -59.86) * mm]});
            skFitSpline(sketch, "E420", {"points": [v(12.04, -59.86) * mm, v(11.65, -59.86) * mm, v(11.35, -59.75) * mm, v(11.15, -59.55) * mm]});
            skFitSpline(sketch, "E421", {"points": [v(11.15, -59.55) * mm, v(10.95, -59.34) * mm, v(10.85, -59) * mm, v(10.85, -58.54) * mm]});
            skLineSegment(sketch, "E422", {"start": v(10.85, -58.54) * mm, "end": v(10.85, -56.52) * mm});
            skLineSegment(sketch, "E423", {"start": v(10.85, -56.52) * mm, "end": v(10.41, -56.52) * mm});
            skLineSegment(sketch, "E424", {"start": v(10.41, -56.52) * mm, "end": v(10.41, -55.98) * mm});
            skLineSegment(sketch, "E425", {"start": v(10.41, -55.98) * mm, "end": v(10.85, -55.98) * mm});
            skLineSegment(sketch, "E426", {"start": v(10.85, -55.98) * mm, "end": v(10.85, -54.89) * mm});
            skLineSegment(sketch, "E427", {"start": v(10.85, -54.89) * mm, "end": v(11.49, -54.89) * mm});
            skLineSegment(sketch, "E428", {"start": v(11.49, -54.89) * mm, "end": v(11.49, -55.98) * mm});
            skLineSegment(sketch, "E429", {"start": v(11.49, -55.98) * mm, "end": v(12.8, -55.98) * mm});
            skLineSegment(sketch, "E430", {"start": v(12.8, -55.98) * mm, "end": v(12.8, -56.52) * mm});
            skLineSegment(sketch, "E431", {"start": v(12.8, -56.52) * mm, "end": v(11.49, -56.52) * mm});
            skLineSegment(sketch, "E432", {"start": v(11.49, -56.52) * mm, "end": v(11.49, -58.25) * mm});
            skFitSpline(sketch, "E433", {"points": [v(11.49, -58.25) * mm, v(11.49, -58.45) * mm, v(11.5, -58.6) * mm, v(11.5, -58.72) * mm]});
            skFitSpline(sketch, "E434", {"points": [v(11.5, -58.72) * mm, v(11.5, -58.83) * mm, v(11.54, -58.94) * mm, v(11.6, -59.03) * mm]});
            skFitSpline(sketch, "E435", {"points": [v(11.6, -59.03) * mm, v(11.65, -59.13) * mm, v(11.71, -59.2) * mm, v(11.8, -59.24) * mm]});
            skFitSpline(sketch, "E436", {"points": [v(11.8, -59.24) * mm, v(11.89, -59.28) * mm, v(12.02, -59.3) * mm, v(12.2, -59.3) * mm]});
            skFitSpline(sketch, "E437", {"points": [v(12.2, -59.3) * mm, v(12.3, -59.3) * mm, v(12.42, -59.28) * mm, v(12.53, -59.25) * mm]});
            skFitSpline(sketch, "E438", {"points": [v(12.53, -59.25) * mm, v(12.64, -59.22) * mm, v(12.72, -59.2) * mm, v(12.77, -59.17) * mm]});
            skLineSegment(sketch, "E439", {"start": v(12.77, -59.17) * mm, "end": v(12.8, -59.17) * mm});
            skLineSegment(sketch, "E440", {"start": v(12.8, -59.17) * mm, "end": v(12.8, -59.75) * mm});
            skLineSegment(sketch, "E441", {"start": v(12.8, -59.75) * mm, "end": v(12.8, -59.75) * mm});
            skLineSegment(sketch, "E442", {"start": v(9.6, -59.78) * mm, "end": v(8.96, -59.78) * mm});
            skLineSegment(sketch, "E443", {"start": v(8.96, -59.78) * mm, "end": v(8.96, -59.38) * mm});
            skFitSpline(sketch, "E444", {"points": [v(8.96, -59.38) * mm, v(8.9, -59.42) * mm, v(8.82, -59.47) * mm, v(8.73, -59.54) * mm]});
            skFitSpline(sketch, "E445", {"points": [v(8.73, -59.54) * mm, v(8.63, -59.6) * mm, v(8.54, -59.66) * mm, v(8.45, -59.7) * mm]});
            skFitSpline(sketch, "E446", {"points": [v(8.45, -59.7) * mm, v(8.34, -59.76) * mm, v(8.22, -59.8) * mm, v(8.08, -59.83) * mm]});
            skFitSpline(sketch, "E447", {"points": [v(8.08, -59.83) * mm, v(7.94, -59.87) * mm, v(7.78, -59.89) * mm, v(7.6, -59.89) * mm]});
            skFitSpline(sketch, "E448", {"points": [v(7.6, -59.89) * mm, v(7.25, -59.89) * mm, v(6.96, -59.78) * mm, v(6.72, -59.55) * mm]});
            skFitSpline(sketch, "E449", {"points": [v(6.72, -59.55) * mm, v(6.48, -59.32) * mm, v(6.36, -59.03) * mm, v(6.36, -58.68) * mm]});
            skFitSpline(sketch, "E450", {"points": [v(6.36, -58.68) * mm, v(6.36, -58.4) * mm, v(6.42, -58.16) * mm, v(6.55, -57.98) * mm]});
            skFitSpline(sketch, "E451", {"points": [v(6.55, -57.98) * mm, v(6.67, -57.8) * mm, v(6.85, -57.66) * mm, v(7.08, -57.56) * mm]});
            skFitSpline(sketch, "E452", {"points": [v(7.08, -57.56) * mm, v(7.3, -57.46) * mm, v(7.59, -57.39) * mm, v(7.91, -57.35) * mm]});
            skFitSpline(sketch, "E453", {"points": [v(7.91, -57.35) * mm, v(8.24, -57.32) * mm, v(8.58, -57.29) * mm, v(8.96, -57.27) * mm]});
            skLineSegment(sketch, "E454", {"start": v(8.96, -57.27) * mm, "end": v(8.96, -57.17) * mm});
            skFitSpline(sketch, "E455", {"points": [v(8.96, -57.17) * mm, v(8.96, -57.03) * mm, v(8.93, -56.9) * mm, v(8.88, -56.81) * mm]});
            skFitSpline(sketch, "E456", {"points": [v(8.88, -56.81) * mm, v(8.83, -56.71) * mm, v(8.76, -56.64) * mm, v(8.66, -56.59) * mm]});
            skFitSpline(sketch, "E457", {"points": [v(8.66, -56.59) * mm, v(8.57, -56.53) * mm, v(8.46, -56.5) * mm, v(8.33, -56.48) * mm]});
            skFitSpline(sketch, "E458", {"points": [v(8.33, -56.48) * mm, v(8.2, -56.46) * mm, v(8.07, -56.45) * mm, v(7.93, -56.45) * mm]});
            skFitSpline(sketch, "E459", {"points": [v(7.93, -56.45) * mm, v(7.77, -56.45) * mm, v(7.58, -56.48) * mm, v(7.37, -56.52) * mm]});
            skFitSpline(sketch, "E460", {"points": [v(7.37, -56.52) * mm, v(7.17, -56.56) * mm, v(6.95, -56.63) * mm, v(6.73, -56.71) * mm]});
            skLineSegment(sketch, "E461", {"start": v(6.73, -56.71) * mm, "end": v(6.7, -56.71) * mm});
            skLineSegment(sketch, "E462", {"start": v(6.7, -56.71) * mm, "end": v(6.7, -56.06) * mm});
            skFitSpline(sketch, "E463", {"points": [v(6.7, -56.06) * mm, v(6.82, -56.03) * mm, v(7, -55.99) * mm, v(7.24, -55.95) * mm]});
            skFitSpline(sketch, "E464", {"points": [v(7.24, -55.95) * mm, v(7.48, -55.9) * mm, v(7.7, -55.89) * mm, v(7.94, -55.89) * mm]});
            skFitSpline(sketch, "E465", {"points": [v(7.94, -55.89) * mm, v(8.2, -55.89) * mm, v(8.44, -55.91) * mm, v(8.64, -55.96) * mm]});
            skFitSpline(sketch, "E466", {"points": [v(8.64, -55.96) * mm, v(8.84, -56) * mm, v(9, -56.07) * mm, v(9.15, -56.18) * mm]});
            skFitSpline(sketch, "E467", {"points": [v(9.15, -56.18) * mm, v(9.3, -56.28) * mm, v(9.4, -56.42) * mm, v(9.48, -56.59) * mm]});
            skFitSpline(sketch, "E468", {"points": [v(9.48, -56.59) * mm, v(9.56, -56.75) * mm, v(9.6, -56.96) * mm, v(9.6, -57.2) * mm]});
            skLineSegment(sketch, "E469", {"start": v(9.6, -57.2) * mm, "end": v(9.6, -59.78) * mm});
            skLineSegment(sketch, "E470", {"start": v(9.6, -59.78) * mm, "end": v(9.6, -59.78) * mm});
            skLineSegment(sketch, "E471", {"start": v(8.96, -58.85) * mm, "end": v(8.96, -57.79) * mm});
            skFitSpline(sketch, "E472", {"points": [v(8.96, -57.79) * mm, v(8.76, -57.8) * mm, v(8.53, -57.82) * mm, v(8.27, -57.84) * mm]});
            skFitSpline(sketch, "E473", {"points": [v(8.27, -57.84) * mm, v(8, -57.86) * mm, v(7.8, -57.9) * mm, v(7.64, -57.94) * mm]});
            skFitSpline(sketch, "E474", {"points": [v(7.64, -57.94) * mm, v(7.45, -57.99) * mm, v(7.3, -58.07) * mm, v(7.2, -58.18) * mm]});
            skFitSpline(sketch, "E475", {"points": [v(7.2, -58.18) * mm, v(7.08, -58.3) * mm, v(7.02, -58.44) * mm, v(7.02, -58.64) * mm]});
            skFitSpline(sketch, "E476", {"points": [v(7.02, -58.64) * mm, v(7.02, -58.85) * mm, v(7.09, -59.02) * mm, v(7.22, -59.13) * mm]});
            skFitSpline(sketch, "E477", {"points": [v(7.22, -59.13) * mm, v(7.35, -59.24) * mm, v(7.55, -59.3) * mm, v(7.82, -59.3) * mm]});
            skFitSpline(sketch, "E478", {"points": [v(7.82, -59.3) * mm, v(8.05, -59.3) * mm, v(8.25, -59.25) * mm, v(8.44, -59.16) * mm]});
            skFitSpline(sketch, "E479", {"points": [v(8.44, -59.16) * mm, v(8.63, -59.08) * mm, v(8.8, -58.97) * mm, v(8.96, -58.85) * mm]});
            skFitSpline(sketch, "E480", {"points": [v(5.86, -59.75) * mm, v(5.74, -59.78) * mm, v(5.6, -59.8) * mm, v(5.47, -59.83) * mm]});
            skFitSpline(sketch, "E481", {"points": [v(5.47, -59.83) * mm, v(5.33, -59.85) * mm, v(5.2, -59.86) * mm, v(5.09, -59.86) * mm]});
            skFitSpline(sketch, "E482", {"points": [v(5.09, -59.86) * mm, v(4.7, -59.86) * mm, v(4.4, -59.75) * mm, v(4.2, -59.55) * mm]});
            skFitSpline(sketch, "E483", {"points": [v(4.2, -59.55) * mm, v(4, -59.34) * mm, v(3.9, -59) * mm, v(3.9, -58.54) * mm]});
            skLineSegment(sketch, "E484", {"start": v(3.9, -58.54) * mm, "end": v(3.9, -56.52) * mm});
            skLineSegment(sketch, "E485", {"start": v(3.9, -56.52) * mm, "end": v(3.47, -56.52) * mm});
            skLineSegment(sketch, "E486", {"start": v(3.47, -56.52) * mm, "end": v(3.47, -55.98) * mm});
            skLineSegment(sketch, "E487", {"start": v(3.47, -55.98) * mm, "end": v(3.9, -55.98) * mm});
            skLineSegment(sketch, "E488", {"start": v(3.9, -55.98) * mm, "end": v(3.9, -54.89) * mm});
            skLineSegment(sketch, "E489", {"start": v(3.9, -54.89) * mm, "end": v(4.54, -54.89) * mm});
            skLineSegment(sketch, "E490", {"start": v(4.54, -54.89) * mm, "end": v(4.54, -55.98) * mm});
            skLineSegment(sketch, "E491", {"start": v(4.54, -55.98) * mm, "end": v(5.86, -55.98) * mm});
            skLineSegment(sketch, "E492", {"start": v(5.86, -55.98) * mm, "end": v(5.86, -56.52) * mm});
            skLineSegment(sketch, "E493", {"start": v(5.86, -56.52) * mm, "end": v(4.54, -56.52) * mm});
            skLineSegment(sketch, "E494", {"start": v(4.54, -56.52) * mm, "end": v(4.54, -58.25) * mm});
            skFitSpline(sketch, "E495", {"points": [v(4.54, -58.25) * mm, v(4.54, -58.45) * mm, v(4.54, -58.6) * mm, v(4.55, -58.72) * mm]});
            skFitSpline(sketch, "E496", {"points": [v(4.55, -58.72) * mm, v(4.56, -58.83) * mm, v(4.6, -58.94) * mm, v(4.65, -59.03) * mm]});
            skFitSpline(sketch, "E497", {"points": [v(4.65, -59.03) * mm, v(4.7, -59.13) * mm, v(4.77, -59.2) * mm, v(4.85, -59.24) * mm]});
            skFitSpline(sketch, "E498", {"points": [v(4.85, -59.24) * mm, v(4.94, -59.28) * mm, v(5.08, -59.3) * mm, v(5.25, -59.3) * mm]});
            skFitSpline(sketch, "E499", {"points": [v(5.25, -59.3) * mm, v(5.36, -59.3) * mm, v(5.47, -59.28) * mm, v(5.58, -59.25) * mm]});
            skFitSpline(sketch, "E500", {"points": [v(5.58, -59.25) * mm, v(5.7, -59.22) * mm, v(5.78, -59.2) * mm, v(5.83, -59.17) * mm]});
            skLineSegment(sketch, "E501", {"start": v(5.83, -59.17) * mm, "end": v(5.86, -59.17) * mm});
            skLineSegment(sketch, "E502", {"start": v(5.86, -59.17) * mm, "end": v(5.86, -59.75) * mm});
            skLineSegment(sketch, "E503", {"start": v(5.86, -59.75) * mm, "end": v(5.86, -59.75) * mm});
            skFitSpline(sketch, "E504", {"points": [v(2.85, -58.34) * mm, v(2.85, -58.53) * mm, v(2.8, -58.73) * mm, v(2.71, -58.92) * mm]});
            skFitSpline(sketch, "E505", {"points": [v(2.71, -58.92) * mm, v(2.62, -59.11) * mm, v(2.5, -59.28) * mm, v(2.33, -59.41) * mm]});
            skFitSpline(sketch, "E506", {"points": [v(2.33, -59.41) * mm, v(2.15, -59.56) * mm, v(1.94, -59.67) * mm, v(1.7, -59.75) * mm]});
            skFitSpline(sketch, "E507", {"points": [v(1.7, -59.75) * mm, v(1.45, -59.83) * mm, v(1.16, -59.88) * mm, v(0.82, -59.88) * mm]});
            skFitSpline(sketch, "E508", {"points": [v(0.82, -59.88) * mm, v(0.45, -59.88) * mm, v(0.13, -59.84) * mm, v(-0.17, -59.77) * mm]});
            skFitSpline(sketch, "E509", {"points": [v(-0.17, -59.77) * mm, v(-0.46, -59.7) * mm, v(-0.75, -59.6) * mm, v(-1.06, -59.47) * mm]});
            skLineSegment(sketch, "E510", {"start": v(-1.06, -59.47) * mm, "end": v(-1.06, -58.63) * mm});
            skLineSegment(sketch, "E511", {"start": v(-1.06, -58.63) * mm, "end": v(-1, -58.63) * mm});
            skFitSpline(sketch, "E512", {"points": [v(-1, -58.63) * mm, v(-0.75, -58.84) * mm, v(-0.46, -59) * mm, v(-0.12, -59.12) * mm]});
            skFitSpline(sketch, "E513", {"points": [v(-0.12, -59.12) * mm, v(0.22, -59.24) * mm, v(0.53, -59.3) * mm, v(0.83, -59.3) * mm]});
            skFitSpline(sketch, "E514", {"points": [v(0.83, -59.3) * mm, v(1.24, -59.3) * mm, v(1.57, -59.21) * mm, v(1.8, -59.06) * mm]});
            skFitSpline(sketch, "E515", {"points": [v(1.8, -59.06) * mm, v(2.04, -58.9) * mm, v(2.15, -58.7) * mm, v(2.15, -58.43) * mm]});
            skFitSpline(sketch, "E516", {"points": [v(2.15, -58.43) * mm, v(2.15, -58.2) * mm, v(2.1, -58.04) * mm, v(1.99, -57.93) * mm]});
            skFitSpline(sketch, "E517", {"points": [v(1.99, -57.93) * mm, v(1.88, -57.83) * mm, v(1.7, -57.74) * mm, v(1.48, -57.69) * mm]});
            skFitSpline(sketch, "E518", {"points": [v(1.48, -57.69) * mm, v(1.31, -57.64) * mm, v(1.13, -57.6) * mm, v(0.93, -57.57) * mm]});
            skFitSpline(sketch, "E519", {"points": [v(0.93, -57.57) * mm, v(0.73, -57.54) * mm, v(0.52, -57.5) * mm, v(0.3, -57.46) * mm]});
            skFitSpline(sketch, "E520", {"points": [v(0.3, -57.46) * mm, v(-0.15, -57.37) * mm, v(-0.48, -57.2) * mm, v(-0.7, -56.97) * mm]});
            skFitSpline(sketch, "E521", {"points": [v(-0.7, -56.97) * mm, v(-0.92, -56.74) * mm, v(-1.03, -56.44) * mm, v(-1.03, -56.07) * mm]});
            skFitSpline(sketch, "E522", {"points": [v(-1.03, -56.07) * mm, v(-1.03, -55.65) * mm, v(-0.85, -55.3) * mm, v(-0.49, -55.03) * mm]});
            skFitSpline(sketch, "E523", {"points": [v(-0.49, -55.03) * mm, v(-0.13, -54.76) * mm, v(0.33, -54.62) * mm, v(0.88, -54.62) * mm]});
            skFitSpline(sketch, "E524", {"points": [v(0.88, -54.62) * mm, v(1.23, -54.62) * mm, v(1.56, -54.65) * mm, v(1.86, -54.72) * mm]});
            skFitSpline(sketch, "E525", {"points": [v(1.86, -54.72) * mm, v(2.16, -54.8) * mm, v(2.42, -54.87) * mm, v(2.65, -54.97) * mm]});
            skLineSegment(sketch, "E526", {"start": v(2.65, -54.97) * mm, "end": v(2.65, -55.77) * mm});
            skLineSegment(sketch, "E527", {"start": v(2.65, -55.77) * mm, "end": v(2.6, -55.77) * mm});
            skFitSpline(sketch, "E528", {"points": [v(2.6, -55.77) * mm, v(2.4, -55.6) * mm, v(2.15, -55.47) * mm, v(1.84, -55.37) * mm]});
            skFitSpline(sketch, "E529", {"points": [v(1.84, -55.37) * mm, v(1.53, -55.26) * mm, v(1.2, -55.2) * mm, v(0.87, -55.2) * mm]});
            skFitSpline(sketch, "E530", {"points": [v(0.87, -55.2) * mm, v(0.51, -55.2) * mm, v(0.22, -55.28) * mm, v(0, -55.43) * mm]});
            skFitSpline(sketch, "E531", {"points": [v(0, -55.43) * mm, v(-0.22, -55.58) * mm, v(-0.32, -55.77) * mm, v(-0.32, -56) * mm]});
            skFitSpline(sketch, "E532", {"points": [v(-0.32, -56) * mm, v(-0.32, -56.22) * mm, v(-0.27, -56.38) * mm, v(-0.16, -56.5) * mm]});
            skFitSpline(sketch, "E533", {"points": [v(-0.16, -56.5) * mm, v(-0.05, -56.62) * mm, v(0.14, -56.72) * mm, v(0.42, -56.78) * mm]});
            skFitSpline(sketch, "E534", {"points": [v(0.42, -56.78) * mm, v(0.56, -56.81) * mm, v(0.77, -56.85) * mm, v(1.03, -56.9) * mm]});
            skFitSpline(sketch, "E535", {"points": [v(1.03, -56.9) * mm, v(1.3, -56.94) * mm, v(1.53, -56.99) * mm, v(1.72, -57.04) * mm]});
            skFitSpline(sketch, "E536", {"points": [v(1.72, -57.04) * mm, v(2.1, -57.13) * mm, v(2.38, -57.29) * mm, v(2.57, -57.49) * mm]});
            skFitSpline(sketch, "E537", {"points": [v(2.57, -57.49) * mm, v(2.76, -57.7) * mm, v(2.85, -57.97) * mm, v(2.85, -58.34) * mm]});
            skLineSegment(sketch, "E538", {"start": v(-4.3, -57.95) * mm, "end": v(-7.1, -57.95) * mm});
            skFitSpline(sketch, "E539", {"points": [v(-7.1, -57.95) * mm, v(-7.1, -58.18) * mm, v(-7.07, -58.39) * mm, v(-7, -58.56) * mm]});
            skFitSpline(sketch, "E540", {"points": [v(-7, -58.56) * mm, v(-6.93, -58.73) * mm, v(-6.84, -58.88) * mm, v(-6.71, -58.99) * mm]});
            skFitSpline(sketch, "E541", {"points": [v(-6.71, -58.99) * mm, v(-6.6, -59.1) * mm, v(-6.46, -59.18) * mm, v(-6.3, -59.23) * mm]});
            skFitSpline(sketch, "E542", {"points": [v(-6.3, -59.23) * mm, v(-6.13, -59.29) * mm, v(-5.95, -59.31) * mm, v(-5.76, -59.31) * mm]});
            skFitSpline(sketch, "E543", {"points": [v(-5.76, -59.31) * mm, v(-5.5, -59.31) * mm, v(-5.24, -59.26) * mm, v(-4.98, -59.16) * mm]});
            skFitSpline(sketch, "E544", {"points": [v(-4.98, -59.16) * mm, v(-4.71, -59.06) * mm, v(-4.53, -58.95) * mm, v(-4.41, -58.85) * mm]});
            skLineSegment(sketch, "E545", {"start": v(-4.41, -58.85) * mm, "end": v(-4.38, -58.85) * mm});
            skLineSegment(sketch, "E546", {"start": v(-4.38, -58.85) * mm, "end": v(-4.38, -59.55) * mm});
            skFitSpline(sketch, "E547", {"points": [v(-4.38, -59.55) * mm, v(-4.6, -59.64) * mm, v(-4.82, -59.72) * mm, v(-5.04, -59.78) * mm]});
            skFitSpline(sketch, "E548", {"points": [v(-5.04, -59.78) * mm, v(-5.27, -59.84) * mm, v(-5.5, -59.87) * mm, v(-5.75, -59.87) * mm]});
            skFitSpline(sketch, "E549", {"points": [v(-5.75, -59.87) * mm, v(-6.38, -59.87) * mm, v(-6.87, -59.7) * mm, v(-7.23, -59.36) * mm]});
            skFitSpline(sketch, "E550", {"points": [v(-7.23, -59.36) * mm, v(-7.58, -59.02) * mm, v(-7.76, -58.53) * mm, v(-7.76, -57.9) * mm]});
            skFitSpline(sketch, "E551", {"points": [v(-7.76, -57.9) * mm, v(-7.76, -57.28) * mm, v(-7.59, -56.79) * mm, v(-7.25, -56.42) * mm]});
            skFitSpline(sketch, "E552", {"points": [v(-7.25, -56.42) * mm, v(-6.91, -56.06) * mm, v(-6.46, -55.87) * mm, v(-5.9, -55.87) * mm]});
            skFitSpline(sketch, "E553", {"points": [v(-5.9, -55.87) * mm, v(-5.4, -55.87) * mm, v(-5, -56.02) * mm, v(-4.72, -56.32) * mm]});
            skFitSpline(sketch, "E554", {"points": [v(-4.72, -56.32) * mm, v(-4.44, -56.62) * mm, v(-4.3, -57.05) * mm, v(-4.3, -57.6) * mm]});
            skLineSegment(sketch, "E555", {"start": v(-4.3, -57.6) * mm, "end": v(-4.3, -57.95) * mm});
            skFitSpline(sketch, "E556", {"points": [v(-4.93, -57.46) * mm, v(-4.93, -57.12) * mm, v(-5.02, -56.86) * mm, v(-5.18, -56.68) * mm]});
            skFitSpline(sketch, "E557", {"points": [v(-5.18, -56.68) * mm, v(-5.35, -56.5) * mm, v(-5.6, -56.4) * mm, v(-5.94, -56.4) * mm]});
            skFitSpline(sketch, "E558", {"points": [v(-5.94, -56.4) * mm, v(-6.29, -56.4) * mm, v(-6.56, -56.5) * mm, v(-6.76, -56.7) * mm]});
            skFitSpline(sketch, "E559", {"points": [v(-6.76, -56.7) * mm, v(-6.97, -56.9) * mm, v(-7.08, -57.16) * mm, v(-7.1, -57.46) * mm]});
            skLineSegment(sketch, "E560", {"start": v(-7.1, -57.46) * mm, "end": v(-4.93, -57.46) * mm});
            skLineSegment(sketch, "E561", {"start": v(-8.72, -59.78) * mm, "end": v(-9.36, -59.78) * mm});
            skLineSegment(sketch, "E562", {"start": v(-9.36, -59.78) * mm, "end": v(-9.36, -57.62) * mm});
            skFitSpline(sketch, "E563", {"points": [v(-9.36, -57.62) * mm, v(-9.36, -57.44) * mm, v(-9.37, -57.28) * mm, v(-9.4, -57.13) * mm]});
            skFitSpline(sketch, "E564", {"points": [v(-9.4, -57.13) * mm, v(-9.41, -56.97) * mm, v(-9.45, -56.85) * mm, v(-9.5, -56.77) * mm]});
            skFitSpline(sketch, "E565", {"points": [v(-9.5, -56.77) * mm, v(-9.56, -56.67) * mm, v(-9.64, -56.6) * mm, v(-9.75, -56.55) * mm]});
            skFitSpline(sketch, "E566", {"points": [v(-9.75, -56.55) * mm, v(-9.86, -56.5) * mm, v(-10, -56.48) * mm, v(-10.17, -56.48) * mm]});
            skFitSpline(sketch, "E567", {"points": [v(-10.17, -56.48) * mm, v(-10.34, -56.48) * mm, v(-10.52, -56.53) * mm, v(-10.71, -56.61) * mm]});
            skFitSpline(sketch, "E568", {"points": [v(-10.71, -56.61) * mm, v(-10.9, -56.7) * mm, v(-11.09, -56.8) * mm, v(-11.26, -56.94) * mm]});
            skLineSegment(sketch, "E569", {"start": v(-11.26, -56.94) * mm, "end": v(-11.26, -59.78) * mm});
            skLineSegment(sketch, "E570", {"start": v(-11.26, -59.78) * mm, "end": v(-11.9, -59.78) * mm});
            skLineSegment(sketch, "E571", {"start": v(-11.9, -59.78) * mm, "end": v(-11.9, -54.48) * mm});
            skLineSegment(sketch, "E572", {"start": v(-11.9, -54.48) * mm, "end": v(-11.26, -54.48) * mm});
            skLineSegment(sketch, "E573", {"start": v(-11.26, -54.48) * mm, "end": v(-11.26, -56.4) * mm});
            skFitSpline(sketch, "E574", {"points": [v(-11.26, -56.4) * mm, v(-11.06, -56.24) * mm, v(-10.86, -56.1) * mm, v(-10.64, -56.01) * mm]});
            skFitSpline(sketch, "E575", {"points": [v(-10.64, -56.01) * mm, v(-10.43, -55.92) * mm, v(-10.21, -55.87) * mm, v(-9.99, -55.87) * mm]});
            skFitSpline(sketch, "E576", {"points": [v(-9.99, -55.87) * mm, v(-9.58, -55.87) * mm, v(-9.26, -56) * mm, v(-9.05, -56.24) * mm]});
            skFitSpline(sketch, "E577", {"points": [v(-9.05, -56.24) * mm, v(-8.83, -56.5) * mm, v(-8.72, -56.85) * mm, v(-8.72, -57.31) * mm]});
            skLineSegment(sketch, "E578", {"start": v(-8.72, -57.31) * mm, "end": v(-8.72, -59.78) * mm});
            skLineSegment(sketch, "E579", {"start": v(-12.54, -55.31) * mm, "end": v(-14.35, -55.31) * mm});
            skLineSegment(sketch, "E580", {"start": v(-14.35, -55.31) * mm, "end": v(-14.35, -59.78) * mm});
            skLineSegment(sketch, "E581", {"start": v(-14.35, -59.78) * mm, "end": v(-15.03, -59.78) * mm});
            skLineSegment(sketch, "E582", {"start": v(-15.03, -59.78) * mm, "end": v(-15.03, -55.31) * mm});
            skLineSegment(sketch, "E583", {"start": v(-15.03, -55.31) * mm, "end": v(-16.84, -55.31) * mm});
            skLineSegment(sketch, "E584", {"start": v(-16.84, -55.31) * mm, "end": v(-16.84, -54.71) * mm});
            skLineSegment(sketch, "E585", {"start": v(-16.84, -54.71) * mm, "end": v(-12.54, -54.71) * mm});
            skLineSegment(sketch, "E586", {"start": v(-12.54, -54.71) * mm, "end": v(-12.54, -55.31) * mm});
            skSolve(sketch);
        }
        {
            var Q0;
            Q0=makeQuery(id+"F12.imprint","IMPRINT",FACE,{"disambiguationData":[TD([[makeQuery(id+"F12.imprint","IMPRINT",EDGE,{"derivedFrom":sQuery(id+"F12.wireOp",EDGE,"E223.0.0")}),-1.0]])]});
            var Q1;
            Q1=makeQuery(id+"F12.imprint","IMPRINT",FACE,{"disambiguationData":[TD([[makeQuery(id+"F12.imprint","IMPRINT",EDGE,{"derivedFrom":sQuery(id+"F12.wireOp",EDGE,"E556")}),1.0]])]});
            var Q2;
            Q2=makeQuery(id+"F12.imprint","IMPRINT",FACE,{"disambiguationData":[TD([[makeQuery(id+"F12.imprint","IMPRINT",EDGE,{"derivedFrom":sQuery(id+"F12.wireOp",EDGE,"E387")}),1.0]])]});
            var Q3;
            Q3=makeQuery(id+"F12.imprint","IMPRINT",FACE,{"disambiguationData":[TD([[makeQuery(id+"F12.imprint","IMPRINT",EDGE,{"derivedFrom":sQuery(id+"F12.wireOp",EDGE,"E471")}),1.0]])]});
            var Q4;
            Q4=makeQuery(id+"F12.imprint","IMPRINT",FACE,{"disambiguationData":[TD([[makeQuery(id+"F12.imprint","IMPRINT",EDGE,{"derivedFrom":sQuery(id+"F12.wireOp",EDGE,"E413")}),1.0]])]});
            var Q5;
            Q5=makeQuery(id+"F12.imprint","IMPRINT",FACE,{"disambiguationData":[TD([[makeQuery(id+"F12.imprint","IMPRINT",EDGE,{"derivedFrom":sQuery(id+"F12.wireOp",EDGE,"E246")}),1.0]])]});
            var Q6;
            Q6=makeQuery(id+"F12.imprint","IMPRINT",FACE,{"disambiguationData":[TD([[makeQuery(id+"F12.imprint","IMPRINT",EDGE,{"derivedFrom":sQuery(id+"F12.wireOp",EDGE,"E279")}),1.0]])]});
            extrude(context, id + "F13", {"entities" : qUnion([Q0, Q1, Q2, Q3, Q4, Q5, Q6]), "operationType" : NewBodyOperationType.REMOVE, "oppositeDirection" : true, "depth" : 1.8 * mm});
        }
        {
            var Q0;
            Q0=makeQuery(id+"F9.opExtrude","CAP_FACE",FACE,{"disambiguationData":[OSD([sQuery(id+"F8.wireOp",EDGE,"E61.0"),sQuery(id+"F8.wireOp",EDGE,"E60.0"),sQuery(id+"F8.wireOp",EDGE,"E62.0"),sQuery(id+"F8.wireOp",EDGE,"E63.0"),sQuery(id+"F8.wireOp",EDGE,"E64.0"),sQuery(id+"F8.wireOp",EDGE,"E65.0"),sQuery(id+"F8.wireOp",EDGE,"E66.0"),sQuery(id+"F8.wireOp",EDGE,"E67.0")])],"isStart":true});
            var sketch = newSketch(context, id + "F14", { "sketchPlane" : qUnion([Q0])});
            skLineSegment(sketch, "E587", {"start": v(13.18, 1.02) * mm, "end": v(14.24, 1.02) * mm});
            skLineSegment(sketch, "E588", {"start": v(14.24, 1.02) * mm, "end": v(14.24, 4.2) * mm});
            skFitSpline(sketch, "E589", {"points": [v(14.24, 4.2) * mm, v(14.24, 4.62) * mm, v(14.28, 4.96) * mm, v(14.38, 5.2) * mm]});
            skFitSpline(sketch, "E590", {"points": [v(14.38, 5.2) * mm, v(14.47, 5.45) * mm, v(14.67, 5.65) * mm, v(14.95, 5.8) * mm]});
            skFitSpline(sketch, "E591", {"points": [v(14.95, 5.8) * mm, v(15.24, 5.94) * mm, v(15.65, 6.02) * mm, v(16.19, 6.02) * mm]});
            skFitSpline(sketch, "E592", {"points": [v(16.19, 6.02) * mm, v(16.5, 6.02) * mm, v(16.85, 6) * mm, v(17.23, 5.94) * mm]});
            skLineSegment(sketch, "E593", {"start": v(17.23, 5.94) * mm, "end": v(17.23, 1.02) * mm});
            skLineSegment(sketch, "E594", {"start": v(17.23, 1.02) * mm, "end": v(18.29, 1.02) * mm});
            skLineSegment(sketch, "E595", {"start": v(18.29, 1.02) * mm, "end": v(18.29, 6.74) * mm});
            skFitSpline(sketch, "E596", {"points": [v(18.29, 6.74) * mm, v(17.5, 6.87) * mm, v(16.78, 6.94) * mm, v(16.12, 6.94) * mm]});
            skFitSpline(sketch, "E597", {"points": [v(16.12, 6.94) * mm, v(15.4, 6.94) * mm, v(14.82, 6.83) * mm, v(14.38, 6.62) * mm]});
            skFitSpline(sketch, "E598", {"points": [v(14.38, 6.62) * mm, v(13.94, 6.4) * mm, v(13.63, 6.12) * mm, v(13.45, 5.77) * mm]});
            skFitSpline(sketch, "E599", {"points": [v(13.45, 5.77) * mm, v(13.27, 5.42) * mm, v(13.18, 4.93) * mm, v(13.18, 4.3) * mm]});
            skLineSegment(sketch, "E600", {"start": v(13.18, 4.3) * mm, "end": v(13.18, 1.02) * mm});
            skLineSegment(sketch, "E601", {"start": v(11, 6.87) * mm, "end": v(7.75, 6.87) * mm});
            skLineSegment(sketch, "E602", {"start": v(7.75, 6.87) * mm, "end": v(7.75, 5.41) * mm});
            skFitSpline(sketch, "E603", {"points": [v(7.75, 5.41) * mm, v(7.75, 5) * mm, v(7.8, 4.67) * mm, v(7.87, 4.41) * mm]});
            skFitSpline(sketch, "E604", {"points": [v(7.87, 4.41) * mm, v(7.95, 4.16) * mm, v(8.08, 3.9) * mm, v(8.27, 3.64) * mm]});
            skLineSegment(sketch, "E605", {"start": v(8.27, 3.64) * mm, "end": v(8.57, 3.24) * mm});
            skFitSpline(sketch, "E606", {"points": [v(8.57, 3.24) * mm, v(8.87, 2.84) * mm, v(9.02, 2.41) * mm, v(9.02, 1.96) * mm]});
            skLineSegment(sketch, "E607", {"start": v(9.02, 1.96) * mm, "end": v(9.02, 1.02) * mm});
            skLineSegment(sketch, "E608", {"start": v(9.02, 1.02) * mm, "end": v(10.07, 1.02) * mm});
            skLineSegment(sketch, "E609", {"start": v(10.07, 1.02) * mm, "end": v(10.07, 1.8) * mm});
            skFitSpline(sketch, "E610", {"points": [v(10.07, 1.8) * mm, v(10.07, 2.28) * mm, v(10.02, 2.64) * mm, v(9.93, 2.88) * mm]});
            skFitSpline(sketch, "E611", {"points": [v(9.93, 2.88) * mm, v(9.83, 3.12) * mm, v(9.7, 3.35) * mm, v(9.52, 3.58) * mm]});
            skLineSegment(sketch, "E612", {"start": v(9.52, 3.58) * mm, "end": v(9.19, 4) * mm});
            skFitSpline(sketch, "E613", {"points": [v(9.19, 4) * mm, v(9.02, 4.2) * mm, v(8.92, 4.4) * mm, v(8.88, 4.56) * mm]});
            skFitSpline(sketch, "E614", {"points": [v(8.88, 4.56) * mm, v(8.83, 4.72) * mm, v(8.8, 4.94) * mm, v(8.8, 5.2) * mm]});
            skLineSegment(sketch, "E615", {"start": v(8.8, 5.2) * mm, "end": v(8.8, 5.99) * mm});
            skLineSegment(sketch, "E616", {"start": v(8.8, 5.99) * mm, "end": v(12.04, 5.99) * mm});
            skLineSegment(sketch, "E617", {"start": v(12.04, 5.99) * mm, "end": v(12.04, 9.1) * mm});
            skLineSegment(sketch, "E618", {"start": v(12.04, 9.1) * mm, "end": v(11, 9.1) * mm});
            skLineSegment(sketch, "E619", {"start": v(11, 9.1) * mm, "end": v(11, 6.87) * mm});
            skLineSegment(sketch, "E620", {"start": v(5.8, 4.43) * mm, "end": v(6.7, 6.87) * mm});
            skLineSegment(sketch, "E621", {"start": v(6.7, 6.87) * mm, "end": v(5.68, 6.87) * mm});
            skLineSegment(sketch, "E622", {"start": v(5.68, 6.87) * mm, "end": v(5.25, 5.58) * mm});
            skFitSpline(sketch, "E623", {"points": [v(5.25, 5.58) * mm, v(5.07, 5.96) * mm, v(4.8, 6.28) * mm, v(4.43, 6.54) * mm]});
            skFitSpline(sketch, "E624", {"points": [v(4.43, 6.54) * mm, v(4.07, 6.8) * mm, v(3.67, 6.94) * mm, v(3.25, 6.94) * mm]});
            skFitSpline(sketch, "E625", {"points": [v(3.25, 6.94) * mm, v(2.8, 6.94) * mm, v(2.42, 6.82) * mm, v(2.1, 6.59) * mm]});
            skFitSpline(sketch, "E626", {"points": [v(2.1, 6.59) * mm, v(1.77, 6.36) * mm, v(1.53, 6.03) * mm, v(1.38, 5.58) * mm]});
            skFitSpline(sketch, "E627", {"points": [v(1.38, 5.58) * mm, v(1.23, 5.14) * mm, v(1.16, 4.48) * mm, v(1.16, 3.6) * mm]});
            skLineSegment(sketch, "E628", {"start": v(1.16, 3.6) * mm, "end": v(1.16, 1.02) * mm});
            skLineSegment(sketch, "E629", {"start": v(1.16, 1.02) * mm, "end": v(4.18, 1.02) * mm});
            skLineSegment(sketch, "E630", {"start": v(4.18, 1.02) * mm, "end": v(4.18, 1.9) * mm});
            skLineSegment(sketch, "E631", {"start": v(4.18, 1.9) * mm, "end": v(2.22, 1.9) * mm});
            skLineSegment(sketch, "E632", {"start": v(2.22, 1.9) * mm, "end": v(2.22, 3.62) * mm});
            skFitSpline(sketch, "E633", {"points": [v(2.22, 3.62) * mm, v(2.22, 4.26) * mm, v(2.25, 4.73) * mm, v(2.3, 5.03) * mm]});
            skFitSpline(sketch, "E634", {"points": [v(2.3, 5.03) * mm, v(2.33, 5.33) * mm, v(2.44, 5.57) * mm, v(2.62, 5.75) * mm]});
            skFitSpline(sketch, "E635", {"points": [v(2.62, 5.75) * mm, v(2.79, 5.94) * mm, v(3, 6.03) * mm, v(3.27, 6.03) * mm]});
            skFitSpline(sketch, "E636", {"points": [v(3.27, 6.03) * mm, v(3.68, 6.03) * mm, v(4.03, 5.82) * mm, v(4.32, 5.4) * mm]});
            skFitSpline(sketch, "E637", {"points": [v(4.32, 5.4) * mm, v(4.61, 4.97) * mm, v(4.86, 4.23) * mm, v(5.06, 3.19) * mm]});
            skLineSegment(sketch, "E638", {"start": v(5.06, 3.19) * mm, "end": v(5.47, 1.02) * mm});
            skLineSegment(sketch, "E639", {"start": v(5.47, 1.02) * mm, "end": v(6.54, 1.02) * mm});
            skLineSegment(sketch, "E640", {"start": v(6.54, 1.02) * mm, "end": v(6.07, 3.3) * mm});
            skFitSpline(sketch, "E641", {"points": [v(6.07, 3.3) * mm, v(6.03, 3.52) * mm, v(5.94, 3.9) * mm, v(5.8, 4.43) * mm]});
            skFitSpline(sketch, "E642", {"points": [v(-0.47, 6.76) * mm, v(-1.14, 6.88) * mm, v(-1.78, 6.94) * mm, v(-2.41, 6.94) * mm]});
            skFitSpline(sketch, "E643", {"points": [v(-2.41, 6.94) * mm, v(-3.63, 6.94) * mm, v(-4.47, 6.7) * mm, v(-4.94, 6.26) * mm]});
            skFitSpline(sketch, "E644", {"points": [v(-4.94, 6.26) * mm, v(-5.4, 5.8) * mm, v(-5.64, 5.11) * mm, v(-5.64, 4.18) * mm]});
            skLineSegment(sketch, "E645", {"start": v(-5.64, 4.18) * mm, "end": v(-5.64, 1.02) * mm});
            skLineSegment(sketch, "E646", {"start": v(-5.64, 1.02) * mm, "end": v(-4.59, 1.02) * mm});
            skLineSegment(sketch, "E647", {"start": v(-4.59, 1.02) * mm, "end": v(-4.59, 3.9) * mm});
            skFitSpline(sketch, "E648", {"points": [v(-4.59, 3.9) * mm, v(-4.59, 4.48) * mm, v(-4.52, 4.91) * mm, v(-4.38, 5.18) * mm]});
            skFitSpline(sketch, "E649", {"points": [v(-4.38, 5.18) * mm, v(-4.25, 5.46) * mm, v(-4.01, 5.67) * mm, v(-3.68, 5.8) * mm]});
            skFitSpline(sketch, "E650", {"points": [v(-3.68, 5.8) * mm, v(-3.35, 5.95) * mm, v(-2.87, 6.02) * mm, v(-2.23, 6.02) * mm]});
            skFitSpline(sketch, "E651", {"points": [v(-2.23, 6.02) * mm, v(-1.73, 6.02) * mm, v(-1.17, 5.97) * mm, v(-0.56, 5.87) * mm]});
            skLineSegment(sketch, "E652", {"start": v(-0.56, 5.87) * mm, "end": v(-0.47, 6.76) * mm});
            skLineSegment(sketch, "E653", {"start": v(-1.59, 4.32) * mm, "end": v(-1.59, 1.02) * mm});
            skLineSegment(sketch, "E654", {"start": v(-1.59, 1.02) * mm, "end": v(-0.54, 1.02) * mm});
            skLineSegment(sketch, "E655", {"start": v(-0.54, 1.02) * mm, "end": v(-0.54, 4.32) * mm});
            skLineSegment(sketch, "E656", {"start": v(-0.54, 4.32) * mm, "end": v(-1.59, 4.32) * mm});
            skLineSegment(sketch, "E657", {"start": v(-15.52, 1.02) * mm, "end": v(-10.42, 1.02) * mm});
            skLineSegment(sketch, "E658", {"start": v(-10.42, 1.02) * mm, "end": v(-10.42, 6.74) * mm});
            skFitSpline(sketch, "E659", {"points": [v(-10.42, 6.74) * mm, v(-11.2, 6.87) * mm, v(-11.93, 6.94) * mm, v(-12.59, 6.94) * mm]});
            skFitSpline(sketch, "E660", {"points": [v(-12.59, 6.94) * mm, v(-13.3, 6.94) * mm, v(-13.89, 6.83) * mm, v(-14.32, 6.62) * mm]});
            skFitSpline(sketch, "E661", {"points": [v(-14.32, 6.62) * mm, v(-14.76, 6.4) * mm, v(-15.07, 6.12) * mm, v(-15.25, 5.77) * mm]});
            skFitSpline(sketch, "E662", {"points": [v(-15.25, 5.77) * mm, v(-15.43, 5.42) * mm, v(-15.52, 4.93) * mm, v(-15.52, 4.3) * mm]});
            skLineSegment(sketch, "E663", {"start": v(-15.52, 4.3) * mm, "end": v(-15.52, 1.02) * mm});
            skLineSegment(sketch, "E664", {"start": v(-14.47, 1.9) * mm, "end": v(-14.47, 4.2) * mm});
            skFitSpline(sketch, "E665", {"points": [v(-14.47, 4.2) * mm, v(-14.47, 4.62) * mm, v(-14.42, 4.96) * mm, v(-14.33, 5.2) * mm]});
            skFitSpline(sketch, "E666", {"points": [v(-14.33, 5.2) * mm, v(-14.23, 5.45) * mm, v(-14.04, 5.65) * mm, v(-13.76, 5.8) * mm]});
            skFitSpline(sketch, "E667", {"points": [v(-13.76, 5.8) * mm, v(-13.47, 5.94) * mm, v(-13.06, 6.02) * mm, v(-12.52, 6.02) * mm]});
            skFitSpline(sketch, "E668", {"points": [v(-12.52, 6.02) * mm, v(-12.2, 6.02) * mm, v(-11.86, 6) * mm, v(-11.47, 5.94) * mm]});
            skLineSegment(sketch, "E669", {"start": v(-11.47, 5.94) * mm, "end": v(-11.47, 1.9) * mm});
            skLineSegment(sketch, "E670", {"start": v(-11.47, 1.9) * mm, "end": v(-14.47, 1.9) * mm});
            skLineSegment(sketch, "E671", {"start": v(-18.26, 6.87) * mm, "end": v(-18.26, 3.84) * mm});
            skLineSegment(sketch, "E672", {"start": v(-18.26, 3.84) * mm, "end": v(-17.19, 3.84) * mm});
            skLineSegment(sketch, "E673", {"start": v(-17.19, 3.84) * mm, "end": v(-17.19, 6.87) * mm});
            skLineSegment(sketch, "E674", {"start": v(-17.19, 6.87) * mm, "end": v(-18.26, 6.87) * mm});
            skLineSegment(sketch, "E675", {"start": v(-23.02, 10.34) * mm, "end": v(-22.41, 10.34) * mm});
            skLineSegment(sketch, "E676", {"start": v(-22.41, 10.34) * mm, "end": v(-22.41, 10.72) * mm});
            skFitSpline(sketch, "E677", {"points": [v(-22.41, 10.72) * mm, v(-22.36, 10.69) * mm, v(-22.28, 10.63) * mm, v(-22.19, 10.57) * mm]});
            skFitSpline(sketch, "E678", {"points": [v(-22.19, 10.57) * mm, v(-22.1, 10.5) * mm, v(-22.01, 10.45) * mm, v(-21.92, 10.41) * mm]});
            skFitSpline(sketch, "E679", {"points": [v(-21.92, 10.41) * mm, v(-21.82, 10.36) * mm, v(-21.7, 10.32) * mm, v(-21.57, 10.29) * mm]});
            skFitSpline(sketch, "E680", {"points": [v(-21.57, 10.29) * mm, v(-21.44, 10.25) * mm, v(-21.29, 10.24) * mm, v(-21.1, 10.24) * mm]});
            skFitSpline(sketch, "E681", {"points": [v(-21.1, 10.24) * mm, v(-20.78, 10.24) * mm, v(-20.5, 10.34) * mm, v(-20.28, 10.56) * mm]});
            skFitSpline(sketch, "E682", {"points": [v(-20.28, 10.56) * mm, v(-20.05, 10.78) * mm, v(-19.94, 11.05) * mm, v(-19.94, 11.39) * mm]});
            skFitSpline(sketch, "E683", {"points": [v(-19.94, 11.39) * mm, v(-19.94, 11.66) * mm, v(-20, 11.88) * mm, v(-20.11, 12.05) * mm]});
            skFitSpline(sketch, "E684", {"points": [v(-20.11, 12.05) * mm, v(-20.23, 12.22) * mm, v(-20.4, 12.36) * mm, v(-20.62, 12.45) * mm]});
            skFitSpline(sketch, "E685", {"points": [v(-20.62, 12.45) * mm, v(-20.84, 12.55) * mm, v(-21.1, 12.62) * mm, v(-21.41, 12.65) * mm]});
            skFitSpline(sketch, "E686", {"points": [v(-21.41, 12.65) * mm, v(-21.72, 12.69) * mm, v(-22.06, 12.71) * mm, v(-22.41, 12.73) * mm]});
            skLineSegment(sketch, "E687", {"start": v(-22.41, 12.73) * mm, "end": v(-22.41, 12.82) * mm});
            skFitSpline(sketch, "E688", {"points": [v(-22.41, 12.82) * mm, v(-22.41, 12.96) * mm, v(-22.39, 13.08) * mm, v(-22.34, 13.17) * mm]});
            skFitSpline(sketch, "E689", {"points": [v(-22.34, 13.17) * mm, v(-22.29, 13.26) * mm, v(-22.22, 13.33) * mm, v(-22.13, 13.38) * mm]});
            skFitSpline(sketch, "E690", {"points": [v(-22.13, 13.38) * mm, v(-22.04, 13.43) * mm, v(-21.94, 13.47) * mm, v(-21.82, 13.48) * mm]});
            skFitSpline(sketch, "E691", {"points": [v(-21.82, 13.48) * mm, v(-21.7, 13.5) * mm, v(-21.57, 13.5) * mm, v(-21.44, 13.5) * mm]});
            skFitSpline(sketch, "E692", {"points": [v(-21.44, 13.5) * mm, v(-21.28, 13.5) * mm, v(-21.1, 13.49) * mm, v(-20.9, 13.44) * mm]});
            skFitSpline(sketch, "E693", {"points": [v(-20.9, 13.44) * mm, v(-20.7, 13.4) * mm, v(-20.5, 13.34) * mm, v(-20.3, 13.26) * mm]});
            skLineSegment(sketch, "E694", {"start": v(-20.3, 13.26) * mm, "end": v(-20.26, 13.26) * mm});
            skLineSegment(sketch, "E695", {"start": v(-20.26, 13.26) * mm, "end": v(-20.26, 13.88) * mm});
            skFitSpline(sketch, "E696", {"points": [v(-20.26, 13.88) * mm, v(-20.38, 13.91) * mm, v(-20.55, 13.95) * mm, v(-20.78, 13.99) * mm]});
            skFitSpline(sketch, "E697", {"points": [v(-20.78, 13.99) * mm, v(-21, 14.03) * mm, v(-21.22, 14.05) * mm, v(-21.44, 14.05) * mm]});
            skFitSpline(sketch, "E698", {"points": [v(-21.44, 14.05) * mm, v(-21.7, 14.05) * mm, v(-21.92, 14.03) * mm, v(-22.1, 13.98) * mm]});
            skFitSpline(sketch, "E699", {"points": [v(-22.1, 13.98) * mm, v(-22.3, 13.94) * mm, v(-22.46, 13.87) * mm, v(-22.6, 13.77) * mm]});
            skFitSpline(sketch, "E700", {"points": [v(-22.6, 13.77) * mm, v(-22.73, 13.67) * mm, v(-22.84, 13.54) * mm, v(-22.9, 13.38) * mm]});
            skFitSpline(sketch, "E701", {"points": [v(-22.9, 13.38) * mm, v(-22.98, 13.22) * mm, v(-23.02, 13.03) * mm, v(-23.02, 12.8) * mm]});
            skLineSegment(sketch, "E702", {"start": v(-23.02, 12.8) * mm, "end": v(-23.02, 10.34) * mm});
            skLineSegment(sketch, "E703", {"start": v(-22.41, 11.23) * mm, "end": v(-22.41, 12.24) * mm});
            skFitSpline(sketch, "E704", {"points": [v(-22.41, 12.24) * mm, v(-22.22, 12.23) * mm, v(-22, 12.2) * mm, v(-21.75, 12.19) * mm]});
            skFitSpline(sketch, "E705", {"points": [v(-21.75, 12.19) * mm, v(-21.5, 12.17) * mm, v(-21.3, 12.14) * mm, v(-21.16, 12.1) * mm]});
            skFitSpline(sketch, "E706", {"points": [v(-21.16, 12.1) * mm, v(-20.98, 12.04) * mm, v(-20.84, 11.97) * mm, v(-20.73, 11.86) * mm]});
            skFitSpline(sketch, "E707", {"points": [v(-20.73, 11.86) * mm, v(-20.62, 11.76) * mm, v(-20.57, 11.61) * mm, v(-20.57, 11.43) * mm]});
            skFitSpline(sketch, "E708", {"points": [v(-20.57, 11.43) * mm, v(-20.57, 11.22) * mm, v(-20.63, 11.07) * mm, v(-20.76, 10.96) * mm]});
            skFitSpline(sketch, "E709", {"points": [v(-20.76, 10.96) * mm, v(-20.88, 10.86) * mm, v(-21.07, 10.8) * mm, v(-21.33, 10.8) * mm]});
            skFitSpline(sketch, "E710", {"points": [v(-21.33, 10.8) * mm, v(-21.54, 10.8) * mm, v(-21.74, 10.84) * mm, v(-21.92, 10.93) * mm]});
            skFitSpline(sketch, "E711", {"points": [v(-21.92, 10.93) * mm, v(-22.1, 11.01) * mm, v(-22.26, 11.11) * mm, v(-22.41, 11.23) * mm]});
            skLineSegment(sketch, "E712", {"start": v(-19.28, 12.08) * mm, "end": v(-16.6, 12.08) * mm});
            skFitSpline(sketch, "E713", {"points": [v(-16.6, 12.08) * mm, v(-16.6, 11.86) * mm, v(-16.64, 11.67) * mm, v(-16.7, 11.5) * mm]});
            skFitSpline(sketch, "E714", {"points": [v(-16.7, 11.5) * mm, v(-16.78, 11.34) * mm, v(-16.87, 11.2) * mm, v(-16.98, 11.1) * mm]});
            skFitSpline(sketch, "E715", {"points": [v(-16.98, 11.1) * mm, v(-17.1, 11) * mm, v(-17.23, 10.91) * mm, v(-17.38, 10.86) * mm]});
            skFitSpline(sketch, "E716", {"points": [v(-17.38, 10.86) * mm, v(-17.54, 10.8) * mm, v(-17.7, 10.78) * mm, v(-17.9, 10.78) * mm]});
            skFitSpline(sketch, "E717", {"points": [v(-17.9, 10.78) * mm, v(-18.14, 10.78) * mm, v(-18.39, 10.83) * mm, v(-18.64, 10.93) * mm]});
            skFitSpline(sketch, "E718", {"points": [v(-18.64, 10.93) * mm, v(-18.89, 11.03) * mm, v(-19.07, 11.13) * mm, v(-19.17, 11.22) * mm]});
            skLineSegment(sketch, "E719", {"start": v(-19.17, 11.22) * mm, "end": v(-19.2, 11.22) * mm});
            skLineSegment(sketch, "E720", {"start": v(-19.2, 11.22) * mm, "end": v(-19.2, 10.56) * mm});
            skFitSpline(sketch, "E721", {"points": [v(-19.2, 10.56) * mm, v(-19, 10.47) * mm, v(-18.8, 10.4) * mm, v(-18.58, 10.34) * mm]});
            skFitSpline(sketch, "E722", {"points": [v(-18.58, 10.34) * mm, v(-18.36, 10.28) * mm, v(-18.14, 10.25) * mm, v(-17.9, 10.25) * mm]});
            skFitSpline(sketch, "E723", {"points": [v(-17.9, 10.25) * mm, v(-17.3, 10.25) * mm, v(-16.83, 10.41) * mm, v(-16.5, 10.74) * mm]});
            skFitSpline(sketch, "E724", {"points": [v(-16.5, 10.74) * mm, v(-16.16, 11.07) * mm, v(-15.99, 11.53) * mm, v(-15.99, 12.13) * mm]});
            skFitSpline(sketch, "E725", {"points": [v(-15.99, 12.13) * mm, v(-15.99, 12.72) * mm, v(-16.15, 13.19) * mm, v(-16.47, 13.54) * mm]});
            skFitSpline(sketch, "E726", {"points": [v(-16.47, 13.54) * mm, v(-16.8, 13.89) * mm, v(-17.22, 14.06) * mm, v(-17.75, 14.06) * mm]});
            skFitSpline(sketch, "E727", {"points": [v(-17.75, 14.06) * mm, v(-18.24, 14.06) * mm, v(-18.61, 13.92) * mm, v(-18.88, 13.63) * mm]});
            skFitSpline(sketch, "E728", {"points": [v(-18.88, 13.63) * mm, v(-19.14, 13.35) * mm, v(-19.28, 12.94) * mm, v(-19.28, 12.42) * mm]});
            skLineSegment(sketch, "E729", {"start": v(-19.28, 12.42) * mm, "end": v(-19.28, 12.08) * mm});
            skFitSpline(sketch, "E730", {"points": [v(-18.68, 12.55) * mm, v(-18.68, 12.87) * mm, v(-18.6, 13.12) * mm, v(-18.44, 13.3) * mm]});
            skFitSpline(sketch, "E731", {"points": [v(-18.44, 13.3) * mm, v(-18.28, 13.47) * mm, v(-18.04, 13.56) * mm, v(-17.72, 13.56) * mm]});
            skFitSpline(sketch, "E732", {"points": [v(-17.72, 13.56) * mm, v(-17.4, 13.56) * mm, v(-17.13, 13.46) * mm, v(-16.94, 13.27) * mm]});
            skFitSpline(sketch, "E733", {"points": [v(-16.94, 13.27) * mm, v(-16.74, 13.08) * mm, v(-16.63, 12.84) * mm, v(-16.6, 12.55) * mm]});
            skLineSegment(sketch, "E734", {"start": v(-16.6, 12.55) * mm, "end": v(-18.68, 12.55) * mm});
            skFitSpline(sketch, "E735", {"points": [v(-15.26, 11.71) * mm, v(-15.26, 11.53) * mm, v(-15.22, 11.34) * mm, v(-15.13, 11.16) * mm]});
            skFitSpline(sketch, "E736", {"points": [v(-15.13, 11.16) * mm, v(-15.04, 10.97) * mm, v(-14.92, 10.82) * mm, v(-14.76, 10.69) * mm]});
            skFitSpline(sketch, "E737", {"points": [v(-14.76, 10.69) * mm, v(-14.59, 10.55) * mm, v(-14.39, 10.44) * mm, v(-14.16, 10.37) * mm]});
            skFitSpline(sketch, "E738", {"points": [v(-14.16, 10.37) * mm, v(-13.93, 10.29) * mm, v(-13.65, 10.25) * mm, v(-13.33, 10.25) * mm]});
            skFitSpline(sketch, "E739", {"points": [v(-13.33, 10.25) * mm, v(-12.98, 10.25) * mm, v(-12.66, 10.28) * mm, v(-12.39, 10.35) * mm]});
            skFitSpline(sketch, "E740", {"points": [v(-12.39, 10.35) * mm, v(-12.1, 10.41) * mm, v(-11.83, 10.5) * mm, v(-11.54, 10.63) * mm]});
            skLineSegment(sketch, "E741", {"start": v(-11.54, 10.63) * mm, "end": v(-11.54, 11.44) * mm});
            skLineSegment(sketch, "E742", {"start": v(-11.54, 11.44) * mm, "end": v(-11.58, 11.44) * mm});
            skFitSpline(sketch, "E743", {"points": [v(-11.58, 11.44) * mm, v(-11.83, 11.24) * mm, v(-12.11, 11.08) * mm, v(-12.43, 10.97) * mm]});
            skFitSpline(sketch, "E744", {"points": [v(-12.43, 10.97) * mm, v(-12.75, 10.86) * mm, v(-13.05, 10.8) * mm, v(-13.33, 10.8) * mm]});
            skFitSpline(sketch, "E745", {"points": [v(-13.33, 10.8) * mm, v(-13.73, 10.8) * mm, v(-14.04, 10.88) * mm, v(-14.26, 11.03) * mm]});
            skFitSpline(sketch, "E746", {"points": [v(-14.26, 11.03) * mm, v(-14.48, 11.18) * mm, v(-14.6, 11.38) * mm, v(-14.6, 11.62) * mm]});
            skFitSpline(sketch, "E747", {"points": [v(-14.6, 11.62) * mm, v(-14.6, 11.84) * mm, v(-14.54, 12) * mm, v(-14.44, 12.1) * mm]});
            skFitSpline(sketch, "E748", {"points": [v(-14.44, 12.1) * mm, v(-14.33, 12.2) * mm, v(-14.17, 12.28) * mm, v(-13.96, 12.33) * mm]});
            skFitSpline(sketch, "E749", {"points": [v(-13.96, 12.33) * mm, v(-13.8, 12.38) * mm, v(-13.62, 12.41) * mm, v(-13.43, 12.44) * mm]});
            skFitSpline(sketch, "E750", {"points": [v(-13.43, 12.44) * mm, v(-13.24, 12.47) * mm, v(-13.04, 12.5) * mm, v(-12.83, 12.55) * mm]});
            skFitSpline(sketch, "E751", {"points": [v(-12.83, 12.55) * mm, v(-12.4, 12.64) * mm, v(-12.08, 12.8) * mm, v(-11.88, 13.01) * mm]});
            skFitSpline(sketch, "E752", {"points": [v(-11.88, 13.01) * mm, v(-11.67, 13.23) * mm, v(-11.57, 13.52) * mm, v(-11.57, 13.87) * mm]});
            skFitSpline(sketch, "E753", {"points": [v(-11.57, 13.87) * mm, v(-11.57, 14.28) * mm, v(-11.74, 14.6) * mm, v(-12.08, 14.86) * mm]});
            skFitSpline(sketch, "E754", {"points": [v(-12.08, 14.86) * mm, v(-12.42, 15.12) * mm, v(-12.86, 15.25) * mm, v(-13.38, 15.25) * mm]});
            skFitSpline(sketch, "E755", {"points": [v(-13.38, 15.25) * mm, v(-13.72, 15.25) * mm, v(-14.03, 15.22) * mm, v(-14.32, 15.16) * mm]});
            skFitSpline(sketch, "E756", {"points": [v(-14.32, 15.16) * mm, v(-14.6, 15.1) * mm, v(-14.85, 15.01) * mm, v(-15.07, 14.92) * mm]});
            skLineSegment(sketch, "E757", {"start": v(-15.07, 14.92) * mm, "end": v(-15.07, 14.16) * mm});
            skLineSegment(sketch, "E758", {"start": v(-15.07, 14.16) * mm, "end": v(-15.02, 14.16) * mm});
            skFitSpline(sketch, "E759", {"points": [v(-15.02, 14.16) * mm, v(-14.84, 14.31) * mm, v(-14.6, 14.44) * mm, v(-14.3, 14.54) * mm]});
            skFitSpline(sketch, "E760", {"points": [v(-14.3, 14.54) * mm, v(-14, 14.65) * mm, v(-13.7, 14.7) * mm, v(-13.38, 14.7) * mm]});
            skFitSpline(sketch, "E761", {"points": [v(-13.38, 14.7) * mm, v(-13.03, 14.7) * mm, v(-12.76, 14.63) * mm, v(-12.55, 14.48) * mm]});
            skFitSpline(sketch, "E762", {"points": [v(-12.55, 14.48) * mm, v(-12.34, 14.34) * mm, v(-12.24, 14.16) * mm, v(-12.24, 13.93) * mm]});
            skFitSpline(sketch, "E763", {"points": [v(-12.24, 13.93) * mm, v(-12.24, 13.73) * mm, v(-12.29, 13.57) * mm, v(-12.4, 13.46) * mm]});
            skFitSpline(sketch, "E764", {"points": [v(-12.4, 13.46) * mm, v(-12.5, 13.35) * mm, v(-12.68, 13.26) * mm, v(-12.94, 13.2) * mm]});
            skFitSpline(sketch, "E765", {"points": [v(-12.94, 13.2) * mm, v(-13.08, 13.17) * mm, v(-13.28, 13.13) * mm, v(-13.53, 13.09) * mm]});
            skFitSpline(sketch, "E766", {"points": [v(-13.53, 13.09) * mm, v(-13.79, 13.04) * mm, v(-14, 13) * mm, v(-14.18, 12.95) * mm]});
            skFitSpline(sketch, "E767", {"points": [v(-14.18, 12.95) * mm, v(-14.54, 12.86) * mm, v(-14.8, 12.71) * mm, v(-14.99, 12.52) * mm]});
            skFitSpline(sketch, "E768", {"points": [v(-14.99, 12.52) * mm, v(-15.17, 12.33) * mm, v(-15.26, 12.06) * mm, v(-15.26, 11.71) * mm]});
            skLineSegment(sketch, "E769", {"start": v(-8.17, 10.34) * mm, "end": v(-7.56, 10.34) * mm});
            skLineSegment(sketch, "E770", {"start": v(-7.56, 10.34) * mm, "end": v(-7.56, 10.72) * mm});
            skFitSpline(sketch, "E771", {"points": [v(-7.56, 10.72) * mm, v(-7.38, 10.56) * mm, v(-7.2, 10.45) * mm, v(-7.01, 10.36) * mm]});
            skFitSpline(sketch, "E772", {"points": [v(-7.01, 10.36) * mm, v(-6.82, 10.28) * mm, v(-6.61, 10.24) * mm, v(-6.4, 10.24) * mm]});
            skFitSpline(sketch, "E773", {"points": [v(-6.4, 10.24) * mm, v(-5.96, 10.24) * mm, v(-5.62, 10.4) * mm, v(-5.36, 10.74) * mm]});
            skFitSpline(sketch, "E774", {"points": [v(-5.36, 10.74) * mm, v(-5.1, 11.07) * mm, v(-4.98, 11.53) * mm, v(-4.98, 12.12) * mm]});
            skFitSpline(sketch, "E775", {"points": [v(-4.98, 12.12) * mm, v(-4.98, 12.43) * mm, v(-5.02, 12.7) * mm, v(-5.11, 12.94) * mm]});
            skFitSpline(sketch, "E776", {"points": [v(-5.11, 12.94) * mm, v(-5.2, 13.18) * mm, v(-5.32, 13.39) * mm, v(-5.47, 13.55) * mm]});
            skFitSpline(sketch, "E777", {"points": [v(-5.47, 13.55) * mm, v(-5.61, 13.72) * mm, v(-5.79, 13.84) * mm, v(-5.98, 13.93) * mm]});
            skFitSpline(sketch, "E778", {"points": [v(-5.98, 13.93) * mm, v(-6.18, 14.02) * mm, v(-6.38, 14.06) * mm, v(-6.6, 14.06) * mm]});
            skFitSpline(sketch, "E779", {"points": [v(-6.6, 14.06) * mm, v(-6.78, 14.06) * mm, v(-6.95, 14.04) * mm, v(-7.1, 14) * mm]});
            skFitSpline(sketch, "E780", {"points": [v(-7.1, 14) * mm, v(-7.24, 13.96) * mm, v(-7.4, 13.9) * mm, v(-7.56, 13.81) * mm]});
            skLineSegment(sketch, "E781", {"start": v(-7.56, 13.81) * mm, "end": v(-7.56, 15.38) * mm});
            skLineSegment(sketch, "E782", {"start": v(-7.56, 15.38) * mm, "end": v(-8.17, 15.38) * mm});
            skLineSegment(sketch, "E783", {"start": v(-8.17, 15.38) * mm, "end": v(-8.17, 10.34) * mm});
            skLineSegment(sketch, "E784", {"start": v(-7.56, 11.23) * mm, "end": v(-7.56, 13.3) * mm});
            skFitSpline(sketch, "E785", {"points": [v(-7.56, 13.3) * mm, v(-7.4, 13.38) * mm, v(-7.25, 13.43) * mm, v(-7.12, 13.46) * mm]});
            skFitSpline(sketch, "E786", {"points": [v(-7.12, 13.46) * mm, v(-6.99, 13.49) * mm, v(-6.85, 13.5) * mm, v(-6.7, 13.5) * mm]});
            skFitSpline(sketch, "E787", {"points": [v(-6.7, 13.5) * mm, v(-6.35, 13.5) * mm, v(-6.09, 13.38) * mm, v(-5.9, 13.15) * mm]});
            skFitSpline(sketch, "E788", {"points": [v(-5.9, 13.15) * mm, v(-5.7, 12.9) * mm, v(-5.61, 12.57) * mm, v(-5.61, 12.13) * mm]});
            skFitSpline(sketch, "E789", {"points": [v(-5.61, 12.13) * mm, v(-5.61, 11.7) * mm, v(-5.68, 11.38) * mm, v(-5.83, 11.15) * mm]});
            skFitSpline(sketch, "E790", {"points": [v(-5.83, 11.15) * mm, v(-5.98, 10.93) * mm, v(-6.21, 10.82) * mm, v(-6.54, 10.82) * mm]});
            skFitSpline(sketch, "E791", {"points": [v(-6.54, 10.82) * mm, v(-6.71, 10.82) * mm, v(-6.89, 10.85) * mm, v(-7.06, 10.93) * mm]});
            skFitSpline(sketch, "E792", {"points": [v(-7.06, 10.93) * mm, v(-7.24, 11) * mm, v(-7.4, 11.1) * mm, v(-7.56, 11.23) * mm]});
            skLineSegment(sketch, "E793", {"start": v(-4.05, 10.34) * mm, "end": v(-3.44, 10.34) * mm});
            skLineSegment(sketch, "E794", {"start": v(-3.44, 10.34) * mm, "end": v(-3.44, 10.72) * mm});
            skFitSpline(sketch, "E795", {"points": [v(-3.44, 10.72) * mm, v(-3.4, 10.69) * mm, v(-3.32, 10.63) * mm, v(-3.22, 10.57) * mm]});
            skFitSpline(sketch, "E796", {"points": [v(-3.22, 10.57) * mm, v(-3.13, 10.5) * mm, v(-3.04, 10.45) * mm, v(-2.96, 10.41) * mm]});
            skFitSpline(sketch, "E797", {"points": [v(-2.96, 10.41) * mm, v(-2.86, 10.36) * mm, v(-2.74, 10.32) * mm, v(-2.6, 10.29) * mm]});
            skFitSpline(sketch, "E798", {"points": [v(-2.6, 10.29) * mm, v(-2.48, 10.25) * mm, v(-2.32, 10.24) * mm, v(-2.14, 10.24) * mm]});
            skFitSpline(sketch, "E799", {"points": [v(-2.14, 10.24) * mm, v(-1.82, 10.24) * mm, v(-1.54, 10.34) * mm, v(-1.31, 10.56) * mm]});
            skFitSpline(sketch, "E800", {"points": [v(-1.31, 10.56) * mm, v(-1.09, 10.78) * mm, v(-0.97, 11.05) * mm, v(-0.97, 11.39) * mm]});
            skFitSpline(sketch, "E801", {"points": [v(-0.97, 11.39) * mm, v(-0.97, 11.66) * mm, v(-1.03, 11.88) * mm, v(-1.15, 12.05) * mm]});
            skFitSpline(sketch, "E802", {"points": [v(-1.15, 12.05) * mm, v(-1.27, 12.22) * mm, v(-1.44, 12.36) * mm, v(-1.65, 12.45) * mm]});
            skFitSpline(sketch, "E803", {"points": [v(-1.65, 12.45) * mm, v(-1.87, 12.55) * mm, v(-2.14, 12.62) * mm, v(-2.45, 12.65) * mm]});
            skFitSpline(sketch, "E804", {"points": [v(-2.45, 12.65) * mm, v(-2.76, 12.69) * mm, v(-3.09, 12.71) * mm, v(-3.44, 12.73) * mm]});
            skLineSegment(sketch, "E805", {"start": v(-3.44, 12.73) * mm, "end": v(-3.44, 12.82) * mm});
            skFitSpline(sketch, "E806", {"points": [v(-3.44, 12.82) * mm, v(-3.44, 12.96) * mm, v(-3.42, 13.08) * mm, v(-3.37, 13.17) * mm]});
            skFitSpline(sketch, "E807", {"points": [v(-3.37, 13.17) * mm, v(-3.32, 13.26) * mm, v(-3.25, 13.33) * mm, v(-3.16, 13.38) * mm]});
            skFitSpline(sketch, "E808", {"points": [v(-3.16, 13.38) * mm, v(-3.08, 13.43) * mm, v(-2.97, 13.47) * mm, v(-2.85, 13.48) * mm]});
            skFitSpline(sketch, "E809", {"points": [v(-2.85, 13.48) * mm, v(-2.73, 13.5) * mm, v(-2.6, 13.5) * mm, v(-2.47, 13.5) * mm]});
            skFitSpline(sketch, "E810", {"points": [v(-2.47, 13.5) * mm, v(-2.31, 13.5) * mm, v(-2.13, 13.49) * mm, v(-1.94, 13.44) * mm]});
            skFitSpline(sketch, "E811", {"points": [v(-1.94, 13.44) * mm, v(-1.74, 13.4) * mm, v(-1.54, 13.34) * mm, v(-1.33, 13.26) * mm]});
            skLineSegment(sketch, "E812", {"start": v(-1.33, 13.26) * mm, "end": v(-1.3, 13.26) * mm});
            skLineSegment(sketch, "E813", {"start": v(-1.3, 13.26) * mm, "end": v(-1.3, 13.88) * mm});
            skFitSpline(sketch, "E814", {"points": [v(-1.3, 13.88) * mm, v(-1.41, 13.91) * mm, v(-1.58, 13.95) * mm, v(-1.8, 13.99) * mm]});
            skFitSpline(sketch, "E815", {"points": [v(-1.8, 13.99) * mm, v(-2.03, 14.03) * mm, v(-2.26, 14.05) * mm, v(-2.47, 14.05) * mm]});
            skFitSpline(sketch, "E816", {"points": [v(-2.47, 14.05) * mm, v(-2.73, 14.05) * mm, v(-2.95, 14.03) * mm, v(-3.14, 13.98) * mm]});
            skFitSpline(sketch, "E817", {"points": [v(-3.14, 13.98) * mm, v(-3.33, 13.94) * mm, v(-3.5, 13.87) * mm, v(-3.63, 13.77) * mm]});
            skFitSpline(sketch, "E818", {"points": [v(-3.63, 13.77) * mm, v(-3.77, 13.67) * mm, v(-3.87, 13.54) * mm, v(-3.94, 13.38) * mm]});
            skFitSpline(sketch, "E819", {"points": [v(-3.94, 13.38) * mm, v(-4.02, 13.22) * mm, v(-4.05, 13.03) * mm, v(-4.05, 12.8) * mm]});
            skLineSegment(sketch, "E820", {"start": v(-4.05, 12.8) * mm, "end": v(-4.05, 10.34) * mm});
            skLineSegment(sketch, "E821", {"start": v(-3.44, 11.23) * mm, "end": v(-3.44, 12.24) * mm});
            skFitSpline(sketch, "E822", {"points": [v(-3.44, 12.24) * mm, v(-3.26, 12.23) * mm, v(-3.04, 12.2) * mm, v(-2.79, 12.19) * mm]});
            skFitSpline(sketch, "E823", {"points": [v(-2.79, 12.19) * mm, v(-2.54, 12.17) * mm, v(-2.34, 12.14) * mm, v(-2.19, 12.1) * mm]});
            skFitSpline(sketch, "E824", {"points": [v(-2.19, 12.1) * mm, v(-2.01, 12.04) * mm, v(-1.87, 11.97) * mm, v(-1.76, 11.86) * mm]});
            skFitSpline(sketch, "E825", {"points": [v(-1.76, 11.86) * mm, v(-1.66, 11.76) * mm, v(-1.6, 11.61) * mm, v(-1.6, 11.43) * mm]});
            skFitSpline(sketch, "E826", {"points": [v(-1.6, 11.43) * mm, v(-1.6, 11.22) * mm, v(-1.66, 11.07) * mm, v(-1.8, 10.96) * mm]});
            skFitSpline(sketch, "E827", {"points": [v(-1.8, 10.96) * mm, v(-1.92, 10.86) * mm, v(-2.1, 10.8) * mm, v(-2.36, 10.8) * mm]});
            skFitSpline(sketch, "E828", {"points": [v(-2.36, 10.8) * mm, v(-2.58, 10.8) * mm, v(-2.77, 10.84) * mm, v(-2.95, 10.93) * mm]});
            skFitSpline(sketch, "E829", {"points": [v(-2.95, 10.93) * mm, v(-3.13, 11.01) * mm, v(-3.3, 11.11) * mm, v(-3.44, 11.23) * mm]});
            skLineSegment(sketch, "E830", {"start": v(-0.31, 12.08) * mm, "end": v(2.36, 12.08) * mm});
            skFitSpline(sketch, "E831", {"points": [v(2.36, 12.08) * mm, v(2.36, 11.86) * mm, v(2.32, 11.67) * mm, v(2.26, 11.5) * mm]});
            skFitSpline(sketch, "E832", {"points": [v(2.26, 11.5) * mm, v(2.2, 11.34) * mm, v(2.1, 11.2) * mm, v(1.98, 11.1) * mm]});
            skFitSpline(sketch, "E833", {"points": [v(1.98, 11.1) * mm, v(1.87, 11) * mm, v(1.74, 10.91) * mm, v(1.58, 10.86) * mm]});
            skFitSpline(sketch, "E834", {"points": [v(1.58, 10.86) * mm, v(1.43, 10.8) * mm, v(1.26, 10.78) * mm, v(1.07, 10.78) * mm]});
            skFitSpline(sketch, "E835", {"points": [v(1.07, 10.78) * mm, v(0.82, 10.78) * mm, v(0.58, 10.83) * mm, v(0.33, 10.93) * mm]});
            skFitSpline(sketch, "E836", {"points": [v(0.33, 10.93) * mm, v(0.08, 11.03) * mm, v(-0.1, 11.13) * mm, v(-0.2, 11.22) * mm]});
            skLineSegment(sketch, "E837", {"start": v(-0.2, 11.22) * mm, "end": v(-0.24, 11.22) * mm});
            skLineSegment(sketch, "E838", {"start": v(-0.24, 11.22) * mm, "end": v(-0.24, 10.56) * mm});
            skFitSpline(sketch, "E839", {"points": [v(-0.24, 10.56) * mm, v(-0.03, 10.47) * mm, v(0.18, 10.4) * mm, v(0.39, 10.34) * mm]});
            skFitSpline(sketch, "E840", {"points": [v(0.39, 10.34) * mm, v(0.6, 10.28) * mm, v(0.83, 10.25) * mm, v(1.06, 10.25) * mm]});
            skFitSpline(sketch, "E841", {"points": [v(1.06, 10.25) * mm, v(1.66, 10.25) * mm, v(2.13, 10.41) * mm, v(2.47, 10.74) * mm]});
            skFitSpline(sketch, "E842", {"points": [v(2.47, 10.74) * mm, v(2.8, 11.07) * mm, v(2.98, 11.53) * mm, v(2.98, 12.13) * mm]});
            skFitSpline(sketch, "E843", {"points": [v(2.98, 12.13) * mm, v(2.98, 12.72) * mm, v(2.82, 13.19) * mm, v(2.5, 13.54) * mm]});
            skFitSpline(sketch, "E844", {"points": [v(2.5, 13.54) * mm, v(2.17, 13.89) * mm, v(1.74, 14.06) * mm, v(1.22, 14.06) * mm]});
            skFitSpline(sketch, "E845", {"points": [v(1.22, 14.06) * mm, v(0.73, 14.06) * mm, v(0.35, 13.92) * mm, v(0.09, 13.63) * mm]});
            skFitSpline(sketch, "E846", {"points": [v(0.09, 13.63) * mm, v(-0.18, 13.35) * mm, v(-0.31, 12.94) * mm, v(-0.31, 12.42) * mm]});
            skLineSegment(sketch, "E847", {"start": v(-0.31, 12.42) * mm, "end": v(-0.31, 12.08) * mm});
            skFitSpline(sketch, "E848", {"points": [v(0.28, 12.55) * mm, v(0.28, 12.87) * mm, v(0.37, 13.12) * mm, v(0.53, 13.3) * mm]});
            skFitSpline(sketch, "E849", {"points": [v(0.53, 13.3) * mm, v(0.68, 13.47) * mm, v(0.92, 13.56) * mm, v(1.25, 13.56) * mm]});
            skFitSpline(sketch, "E850", {"points": [v(1.25, 13.56) * mm, v(1.58, 13.56) * mm, v(1.84, 13.46) * mm, v(2.03, 13.27) * mm]});
            skFitSpline(sketch, "E851", {"points": [v(2.03, 13.27) * mm, v(2.22, 13.08) * mm, v(2.33, 12.84) * mm, v(2.36, 12.55) * mm]});
            skLineSegment(sketch, "E852", {"start": v(2.36, 12.55) * mm, "end": v(0.28, 12.55) * mm});
            skFitSpline(sketch, "E853", {"points": [v(3.72, 12.75) * mm, v(3.72, 12.3) * mm, v(3.81, 11.9) * mm, v(4, 11.55) * mm]});
            skFitSpline(sketch, "E854", {"points": [v(4, 11.55) * mm, v(4.2, 11.2) * mm, v(4.45, 10.92) * mm, v(4.77, 10.72) * mm]});
            skFitSpline(sketch, "E855", {"points": [v(4.77, 10.72) * mm, v(4.99, 10.59) * mm, v(5.23, 10.49) * mm, v(5.5, 10.43) * mm]});
            skFitSpline(sketch, "E856", {"points": [v(5.5, 10.43) * mm, v(5.78, 10.37) * mm, v(6.13, 10.34) * mm, v(6.58, 10.34) * mm]});
            skLineSegment(sketch, "E857", {"start": v(6.58, 10.34) * mm, "end": v(7.8, 10.34) * mm});
            skLineSegment(sketch, "E858", {"start": v(7.8, 10.34) * mm, "end": v(7.8, 15.17) * mm});
            skLineSegment(sketch, "E859", {"start": v(7.8, 15.17) * mm, "end": v(6.6, 15.17) * mm});
            skFitSpline(sketch, "E860", {"points": [v(6.6, 15.17) * mm, v(6.12, 15.17) * mm, v(5.74, 15.13) * mm, v(5.47, 15.06) * mm]});
            skFitSpline(sketch, "E861", {"points": [v(5.47, 15.06) * mm, v(5.19, 15) * mm, v(4.95, 14.9) * mm, v(4.76, 14.78) * mm]});
            skFitSpline(sketch, "E862", {"points": [v(4.76, 14.78) * mm, v(4.43, 14.58) * mm, v(4.18, 14.3) * mm, v(4, 13.96) * mm]});
            skFitSpline(sketch, "E863", {"points": [v(4, 13.96) * mm, v(3.8, 13.62) * mm, v(3.72, 13.22) * mm, v(3.72, 12.75) * mm]});
            skFitSpline(sketch, "E864", {"points": [v(4.39, 12.76) * mm, v(4.39, 13.13) * mm, v(4.45, 13.45) * mm, v(4.59, 13.71) * mm]});
            skFitSpline(sketch, "E865", {"points": [v(4.59, 13.71) * mm, v(4.72, 13.97) * mm, v(4.91, 14.18) * mm, v(5.18, 14.33) * mm]});
            skFitSpline(sketch, "E866", {"points": [v(5.18, 14.33) * mm, v(5.37, 14.43) * mm, v(5.57, 14.5) * mm, v(5.78, 14.55) * mm]});
            skFitSpline(sketch, "E867", {"points": [v(5.78, 14.55) * mm, v(6, 14.6) * mm, v(6.25, 14.61) * mm, v(6.55, 14.61) * mm]});
            skLineSegment(sketch, "E868", {"start": v(6.55, 14.61) * mm, "end": v(7.15, 14.61) * mm});
            skLineSegment(sketch, "E869", {"start": v(7.15, 14.61) * mm, "end": v(7.15, 10.89) * mm});
            skLineSegment(sketch, "E870", {"start": v(7.15, 10.89) * mm, "end": v(6.55, 10.89) * mm});
            skFitSpline(sketch, "E871", {"points": [v(6.55, 10.89) * mm, v(6.24, 10.89) * mm, v(5.97, 10.91) * mm, v(5.74, 10.96) * mm]});
            skFitSpline(sketch, "E872", {"points": [v(5.74, 10.96) * mm, v(5.51, 11) * mm, v(5.3, 11.09) * mm, v(5.1, 11.2) * mm]});
            skFitSpline(sketch, "E873", {"points": [v(5.1, 11.2) * mm, v(4.87, 11.36) * mm, v(4.69, 11.56) * mm, v(4.57, 11.82) * mm]});
            skFitSpline(sketch, "E874", {"points": [v(4.57, 11.82) * mm, v(4.45, 12.07) * mm, v(4.39, 12.38) * mm, v(4.39, 12.76) * mm]});
            skLineSegment(sketch, "E875", {"start": v(11.1, 12.08) * mm, "end": v(13.77, 12.08) * mm});
            skFitSpline(sketch, "E876", {"points": [v(13.77, 12.08) * mm, v(13.77, 11.86) * mm, v(13.74, 11.67) * mm, v(13.67, 11.5) * mm]});
            skFitSpline(sketch, "E877", {"points": [v(13.67, 11.5) * mm, v(13.6, 11.34) * mm, v(13.51, 11.2) * mm, v(13.4, 11.1) * mm]});
            skFitSpline(sketch, "E878", {"points": [v(13.4, 11.1) * mm, v(13.29, 11) * mm, v(13.15, 10.91) * mm, v(13, 10.86) * mm]});
            skFitSpline(sketch, "E879", {"points": [v(13, 10.86) * mm, v(12.84, 10.8) * mm, v(12.67, 10.78) * mm, v(12.49, 10.78) * mm]});
            skFitSpline(sketch, "E880", {"points": [v(12.49, 10.78) * mm, v(12.24, 10.78) * mm, v(12, 10.83) * mm, v(11.74, 10.93) * mm]});
            skFitSpline(sketch, "E881", {"points": [v(11.74, 10.93) * mm, v(11.5, 11.03) * mm, v(11.31, 11.13) * mm, v(11.2, 11.22) * mm]});
            skLineSegment(sketch, "E882", {"start": v(11.2, 11.22) * mm, "end": v(11.18, 11.22) * mm});
            skLineSegment(sketch, "E883", {"start": v(11.18, 11.22) * mm, "end": v(11.18, 10.56) * mm});
            skFitSpline(sketch, "E884", {"points": [v(11.18, 10.56) * mm, v(11.38, 10.47) * mm, v(11.6, 10.4) * mm, v(11.8, 10.34) * mm]});
            skFitSpline(sketch, "E885", {"points": [v(11.8, 10.34) * mm, v(12.02, 10.28) * mm, v(12.24, 10.25) * mm, v(12.48, 10.25) * mm]});
            skFitSpline(sketch, "E886", {"points": [v(12.48, 10.25) * mm, v(13.08, 10.25) * mm, v(13.55, 10.41) * mm, v(13.89, 10.74) * mm]});
            skFitSpline(sketch, "E887", {"points": [v(13.89, 10.74) * mm, v(14.22, 11.07) * mm, v(14.4, 11.53) * mm, v(14.4, 12.13) * mm]});
            skFitSpline(sketch, "E888", {"points": [v(14.4, 12.13) * mm, v(14.4, 12.72) * mm, v(14.23, 13.19) * mm, v(13.9, 13.54) * mm]});
            skFitSpline(sketch, "E889", {"points": [v(13.9, 13.54) * mm, v(13.59, 13.89) * mm, v(13.16, 14.06) * mm, v(12.63, 14.06) * mm]});
            skFitSpline(sketch, "E890", {"points": [v(12.63, 14.06) * mm, v(12.14, 14.06) * mm, v(11.77, 13.92) * mm, v(11.5, 13.63) * mm]});
            skFitSpline(sketch, "E891", {"points": [v(11.5, 13.63) * mm, v(11.24, 13.35) * mm, v(11.1, 12.94) * mm, v(11.1, 12.42) * mm]});
            skLineSegment(sketch, "E892", {"start": v(11.1, 12.42) * mm, "end": v(11.1, 12.08) * mm});
            skFitSpline(sketch, "E893", {"points": [v(11.7, 12.55) * mm, v(11.7, 12.87) * mm, v(11.78, 13.12) * mm, v(11.94, 13.3) * mm]});
            skFitSpline(sketch, "E894", {"points": [v(11.94, 13.3) * mm, v(12.1, 13.47) * mm, v(12.34, 13.56) * mm, v(12.66, 13.56) * mm]});
            skFitSpline(sketch, "E895", {"points": [v(12.66, 13.56) * mm, v(13, 13.56) * mm, v(13.25, 13.46) * mm, v(13.45, 13.27) * mm]});
            skFitSpline(sketch, "E896", {"points": [v(13.45, 13.27) * mm, v(13.64, 13.08) * mm, v(13.75, 12.84) * mm, v(13.77, 12.55) * mm]});
            skLineSegment(sketch, "E897", {"start": v(13.77, 12.55) * mm, "end": v(11.7, 12.55) * mm});
            skLineSegment(sketch, "E898", {"start": v(15.31, 10.34) * mm, "end": v(15.92, 10.34) * mm});
            skLineSegment(sketch, "E899", {"start": v(15.92, 10.34) * mm, "end": v(15.92, 12.4) * mm});
            skFitSpline(sketch, "E900", {"points": [v(15.92, 12.4) * mm, v(15.92, 12.57) * mm, v(15.93, 12.72) * mm, v(15.95, 12.87) * mm]});
            skFitSpline(sketch, "E901", {"points": [v(15.95, 12.87) * mm, v(15.97, 13.01) * mm, v(16, 13.13) * mm, v(16.06, 13.2) * mm]});
            skFitSpline(sketch, "E902", {"points": [v(16.06, 13.2) * mm, v(16.11, 13.3) * mm, v(16.19, 13.37) * mm, v(16.3, 13.41) * mm]});
            skFitSpline(sketch, "E903", {"points": [v(16.3, 13.41) * mm, v(16.4, 13.46) * mm, v(16.52, 13.48) * mm, v(16.69, 13.48) * mm]});
            skFitSpline(sketch, "E904", {"points": [v(16.69, 13.48) * mm, v(16.85, 13.48) * mm, v(17.03, 13.44) * mm, v(17.2, 13.36) * mm]});
            skFitSpline(sketch, "E905", {"points": [v(17.2, 13.36) * mm, v(17.39, 13.27) * mm, v(17.56, 13.17) * mm, v(17.73, 13.04) * mm]});
            skLineSegment(sketch, "E906", {"start": v(17.73, 13.04) * mm, "end": v(17.73, 10.34) * mm});
            skLineSegment(sketch, "E907", {"start": v(17.73, 10.34) * mm, "end": v(18.34, 10.34) * mm});
            skLineSegment(sketch, "E908", {"start": v(18.34, 10.34) * mm, "end": v(18.34, 15.38) * mm});
            skLineSegment(sketch, "E909", {"start": v(18.34, 15.38) * mm, "end": v(17.73, 15.38) * mm});
            skLineSegment(sketch, "E910", {"start": v(17.73, 15.38) * mm, "end": v(17.73, 13.56) * mm});
            skFitSpline(sketch, "E911", {"points": [v(17.73, 13.56) * mm, v(17.54, 13.71) * mm, v(17.34, 13.84) * mm, v(17.14, 13.93) * mm]});
            skFitSpline(sketch, "E912", {"points": [v(17.14, 13.93) * mm, v(16.94, 14.02) * mm, v(16.73, 14.06) * mm, v(16.51, 14.06) * mm]});
            skFitSpline(sketch, "E913", {"points": [v(16.51, 14.06) * mm, v(16.12, 14.06) * mm, v(15.82, 13.94) * mm, v(15.62, 13.7) * mm]});
            skFitSpline(sketch, "E914", {"points": [v(15.62, 13.7) * mm, v(15.41, 13.47) * mm, v(15.31, 13.13) * mm, v(15.31, 12.69) * mm]});
            skLineSegment(sketch, "E915", {"start": v(15.31, 12.69) * mm, "end": v(15.31, 10.34) * mm});
            skLineSegment(sketch, "E916", {"start": v(18.95, 14.6) * mm, "end": v(20.67, 14.6) * mm});
            skLineSegment(sketch, "E917", {"start": v(20.67, 14.6) * mm, "end": v(20.67, 10.34) * mm});
            skLineSegment(sketch, "E918", {"start": v(20.67, 10.34) * mm, "end": v(21.31, 10.34) * mm});
            skLineSegment(sketch, "E919", {"start": v(21.31, 10.34) * mm, "end": v(21.31, 14.6) * mm});
            skLineSegment(sketch, "E920", {"start": v(21.31, 14.6) * mm, "end": v(23.04, 14.6) * mm});
            skLineSegment(sketch, "E921", {"start": v(23.04, 14.6) * mm, "end": v(23.04, 15.17) * mm});
            skLineSegment(sketch, "E922", {"start": v(23.04, 15.17) * mm, "end": v(18.95, 15.17) * mm});
            skLineSegment(sketch, "E923", {"start": v(18.95, 15.17) * mm, "end": v(18.95, 14.6) * mm});
            skSolve(sketch);
        }
        {
            var Q0;
            Q0=makeQuery(id+"F14.imprint","IMPRINT",FACE,{"disambiguationData":[TD([[makeQuery(id+"F14.imprint","IMPRINT",EDGE,{"derivedFrom":sQuery(id+"F14.wireOp",EDGE,"E675")}),1.0]])]});
            var Q1;
            Q1=makeQuery(id+"F14.imprint","IMPRINT",FACE,{"disambiguationData":[TD([[makeQuery(id+"F14.imprint","IMPRINT",EDGE,{"derivedFrom":sQuery(id+"F14.wireOp",EDGE,"E712")}),1.0]])]});
            var Q2;
            Q2=makeQuery(id+"F14.imprint","IMPRINT",FACE,{"disambiguationData":[TD([[makeQuery(id+"F14.imprint","IMPRINT",EDGE,{"derivedFrom":sQuery(id+"F14.wireOp",EDGE,"E735")}),1.0]])]});
            var Q3;
            Q3=makeQuery(id+"F14.imprint","IMPRINT",FACE,{"disambiguationData":[TD([[makeQuery(id+"F14.imprint","IMPRINT",EDGE,{"derivedFrom":sQuery(id+"F14.wireOp",EDGE,"E769")}),1.0]])]});
            var Q4;
            Q4=makeQuery(id+"F14.imprint","IMPRINT",FACE,{"disambiguationData":[TD([[makeQuery(id+"F14.imprint","IMPRINT",EDGE,{"derivedFrom":sQuery(id+"F14.wireOp",EDGE,"E793")}),1.0]])]});
            var Q5;
            Q5=makeQuery(id+"F14.imprint","IMPRINT",FACE,{"disambiguationData":[TD([[makeQuery(id+"F14.imprint","IMPRINT",EDGE,{"derivedFrom":sQuery(id+"F14.wireOp",EDGE,"E830")}),1.0]])]});
            var Q6;
            Q6=makeQuery(id+"F14.imprint","IMPRINT",FACE,{"disambiguationData":[TD([[makeQuery(id+"F14.imprint","IMPRINT",EDGE,{"derivedFrom":sQuery(id+"F14.wireOp",EDGE,"E853")}),1.0]])]});
            var Q7;
            Q7=makeQuery(id+"F14.imprint","IMPRINT",FACE,{"disambiguationData":[TD([[makeQuery(id+"F14.imprint","IMPRINT",EDGE,{"derivedFrom":sQuery(id+"F14.wireOp",EDGE,"E875")}),1.0]])]});
            var Q8;
            Q8=makeQuery(id+"F14.imprint","IMPRINT",FACE,{"disambiguationData":[TD([[makeQuery(id+"F14.imprint","IMPRINT",EDGE,{"derivedFrom":sQuery(id+"F14.wireOp",EDGE,"E898")}),1.0]])]});
            var Q9;
            Q9=makeQuery(id+"F14.imprint","IMPRINT",FACE,{"disambiguationData":[TD([[makeQuery(id+"F14.imprint","IMPRINT",EDGE,{"derivedFrom":sQuery(id+"F14.wireOp",EDGE,"E916")}),1.0]])]});
            var Q10;
            Q10=makeQuery(id+"F14.imprint","IMPRINT",FACE,{"disambiguationData":[TD([[makeQuery(id+"F14.imprint","IMPRINT",EDGE,{"derivedFrom":sQuery(id+"F14.wireOp",EDGE,"E587")}),1.0]])]});
            var Q11;
            Q11=makeQuery(id+"F14.imprint","IMPRINT",FACE,{"disambiguationData":[TD([[makeQuery(id+"F14.imprint","IMPRINT",EDGE,{"derivedFrom":sQuery(id+"F14.wireOp",EDGE,"E601")}),1.0]])]});
            var Q12;
            Q12=makeQuery(id+"F14.imprint","IMPRINT",FACE,{"disambiguationData":[TD([[makeQuery(id+"F14.imprint","IMPRINT",EDGE,{"derivedFrom":sQuery(id+"F14.wireOp",EDGE,"E620")}),1.0]])]});
            var Q13;
            Q13=makeQuery(id+"F14.imprint","IMPRINT",FACE,{"disambiguationData":[TD([[makeQuery(id+"F14.imprint","IMPRINT",EDGE,{"derivedFrom":sQuery(id+"F14.wireOp",EDGE,"E642")}),1.0]])]});
            var Q14;
            Q14=makeQuery(id+"F14.imprint","IMPRINT",FACE,{"disambiguationData":[TD([[makeQuery(id+"F14.imprint","IMPRINT",EDGE,{"derivedFrom":sQuery(id+"F14.wireOp",EDGE,"E653")}),1.0]])]});
            var Q15;
            Q15=makeQuery(id+"F14.imprint","IMPRINT",FACE,{"disambiguationData":[TD([[makeQuery(id+"F14.imprint","IMPRINT",EDGE,{"derivedFrom":sQuery(id+"F14.wireOp",EDGE,"E657")}),1.0]])]});
            var Q16;
            Q16=makeQuery(id+"F14.imprint","IMPRINT",FACE,{"disambiguationData":[TD([[makeQuery(id+"F14.imprint","IMPRINT",EDGE,{"derivedFrom":sQuery(id+"F14.wireOp",EDGE,"E671")}),1.0]])]});
            var Q17;
            Q17=sQuery(id+"F14.wireOp",EDGE,"E906");
            var Q18;
            Q18=sQuery(id+"F14.wireOp",EDGE,"E595");
            var Q19;
            Q19=sQuery(id+"F14.wireOp",EDGE,"E647");
            var Q20;
            Q20=sQuery(id+"F14.wireOp",EDGE,"E617");
            var Q21;
            Q21=sQuery(id+"F14.wireOp",EDGE,"E919");
            var Q22;
            Q22=sQuery(id+"F14.wireOp",EDGE,"E600");
            var Q23;
            Q23=sQuery(id+"F14.wireOp",EDGE,"E593");
            var Q24;
            Q24=sQuery(id+"F14.wireOp",EDGE,"E869");
            var Q25;
            Q25=sQuery(id+"F14.wireOp",EDGE,"E645");
            var Q26;
            Q26=sQuery(id+"F14.wireOp",EDGE,"E858");
            var Q27;
            Q27=sQuery(id+"F14.wireOp",EDGE,"E917");
            var Q28;
            Q28=sQuery(id+"F14.wireOp",EDGE,"E588");
            var Q29;
            Q29=sQuery(id+"F14.wireOp",EDGE,"E616");
            var Q30;
            Q30=sQuery(id+"F14.wireOp",EDGE,"E601");
            var Q31;
            Q31=sQuery(id+"F14.wireOp",EDGE,"E620");
            var Q32;
            Q32=sQuery(id+"F14.wireOp",EDGE,"E908");
            var Q33;
            Q33=sQuery(id+"F14.wireOp",EDGE,"E669");
            var Q34;
            Q34=sQuery(id+"F14.wireOp",EDGE,"E653");
            var Q35;
            Q35=sQuery(id+"F14.wireOp",EDGE,"E671");
            var Q36;
            Q36=sQuery(id+"F14.wireOp",EDGE,"E655");
            var Q37;
            Q37=sQuery(id+"F14.wireOp",EDGE,"E670");
            var Q38;
            Q38=sQuery(id+"F14.wireOp",EDGE,"E658");
            var Q39;
            Q39=sQuery(id+"F14.wireOp",EDGE,"E673");
            var Q40;
            Q40=sQuery(id+"F14.wireOp",EDGE,"E657");
            var Q41;
            Q41=sQuery(id+"F14.wireOp",EDGE,"E635");
            var Q42;
            Q42=sQuery(id+"F14.wireOp",EDGE,"E890");
            var Q43;
            Q43=sQuery(id+"F14.wireOp",EDGE,"E599");
            var Q44;
            Q44=sQuery(id+"F14.wireOp",EDGE,"E619");
            var Q45;
            Q45=sQuery(id+"F14.wireOp",EDGE,"E667");
            var Q46;
            Q46=sQuery(id+"F14.wireOp",EDGE,"E631");
            var Q47;
            Q47=sQuery(id+"F14.wireOp",EDGE,"E773");
            var Q48;
            Q48=sQuery(id+"F14.wireOp",EDGE,"E916");
            var Q49;
            Q49=sQuery(id+"F14.wireOp",EDGE,"E921");
            var Q50;
            Q50=sQuery(id+"F14.wireOp",EDGE,"E666");
            var Q51;
            Q51=sQuery(id+"F14.wireOp",EDGE,"E618");
            var Q52;
            Q52=sQuery(id+"F14.wireOp",EDGE,"E920");
            var Q53;
            Q53=sQuery(id+"F14.wireOp",EDGE,"E613");
            var Q54;
            Q54=sQuery(id+"F14.wireOp",EDGE,"E629");
            var Q55;
            Q55=sQuery(id+"F14.wireOp",EDGE,"E651");
            var Q56;
            Q56=sQuery(id+"F14.wireOp",EDGE,"E603");
            var Q57;
            Q57=sQuery(id+"F14.wireOp",EDGE,"E922");
            var Q58;
            Q58=sQuery(id+"F14.wireOp",EDGE,"E634");
            var Q59;
            Q59=sQuery(id+"F14.wireOp",EDGE,"E650");
            var Q60;
            Q60=sQuery(id+"F14.wireOp",EDGE,"E662");
            var Q61;
            Q61=sQuery(id+"F14.wireOp",EDGE,"E633");
            var Q62;
            Q62=sQuery(id+"F14.wireOp",EDGE,"E596");
            var Q63;
            Q63=sQuery(id+"F14.wireOp",EDGE,"E728");
            var Q64;
            Q64=sQuery(id+"F14.wireOp",EDGE,"E660");
            var Q65;
            Q65=sQuery(id+"F14.wireOp",EDGE,"E614");
            var Q66;
            Q66=sQuery(id+"F14.wireOp",EDGE,"E646");
            var Q67;
            Q67=sQuery(id+"F14.wireOp",EDGE,"E857");
            var Q68;
            Q68=sQuery(id+"F14.wireOp",EDGE,"E598");
            var Q69;
            Q69=sQuery(id+"F14.wireOp",EDGE,"E644");
            var Q70;
            Q70=sQuery(id+"F14.wireOp",EDGE,"E615");
            var Q71;
            Q71=sQuery(id+"F14.wireOp",EDGE,"E664");
            var Q72;
            Q72=sQuery(id+"F14.wireOp",EDGE,"E632");
            var Q73;
            Q73=sQuery(id+"F14.wireOp",EDGE,"E648");
            var Q74;
            Q74=sQuery(id+"F14.wireOp",EDGE,"E594");
            var Q75;
            Q75=sQuery(id+"F14.wireOp",EDGE,"E590");
            var Q76;
            Q76=sQuery(id+"F14.wireOp",EDGE,"E589");
            var Q77;
            Q77=sQuery(id+"F14.wireOp",EDGE,"E592");
            var Q78;
            Q78=sQuery(id+"F14.wireOp",EDGE,"E630");
            var Q79;
            Q79=sQuery(id+"F14.wireOp",EDGE,"E587");
            var Q80;
            Q80=sQuery(id+"F14.wireOp",EDGE,"E887");
            var Q81;
            Q81=sQuery(id+"F14.wireOp",EDGE,"E663");
            var Q82;
            Q82=sQuery(id+"F14.wireOp",EDGE,"E870");
            var Q83;
            Q83=sQuery(id+"F14.wireOp",EDGE,"E918");
            var Q84;
            Q84=sQuery(id+"F14.wireOp",EDGE,"E789");
            var Q85;
            Q85=sQuery(id+"F14.wireOp",EDGE,"E628");
            var Q86;
            Q86=sQuery(id+"F14.wireOp",EDGE,"E790");
            var Q87;
            Q87=sQuery(id+"F14.wireOp",EDGE,"E774");
            var Q88;
            Q88=sQuery(id+"F14.wireOp",EDGE,"E665");
            var Q89;
            Q89=sQuery(id+"F14.wireOp",EDGE,"E591");
            var Q90;
            Q90=sQuery(id+"F14.wireOp",EDGE,"E661");
            var Q91;
            Q91=sQuery(id+"F14.wireOp",EDGE,"E602");
            var Q92;
            Q92=sQuery(id+"F14.wireOp",EDGE,"E612");
            var Q93;
            Q93=sQuery(id+"F14.wireOp",EDGE,"E597");
            var Q94;
            Q94=sQuery(id+"F14.wireOp",EDGE,"E923");
            var Q95;
            Q95=sQuery(id+"F14.wireOp",EDGE,"E891");
            var Q96;
            Q96=sQuery(id+"F14.wireOp",EDGE,"E604");
            var Q97;
            Q97=sQuery(id+"F14.wireOp",EDGE,"E668");
            var Q98;
            Q98=sQuery(id+"F14.wireOp",EDGE,"E652");
            var Q99;
            Q99=sQuery(id+"F14.wireOp",EDGE,"E780");
            var Q100;
            Q100=sQuery(id+"F14.wireOp",EDGE,"E782");
            var Q101;
            Q101=sQuery(id+"F14.wireOp",EDGE,"E862");
            var Q102;
            Q102=sQuery(id+"F14.wireOp",EDGE,"E621");
            var Q103;
            Q103=sQuery(id+"F14.wireOp",EDGE,"E605");
            var Q104;
            Q104=sQuery(id+"F14.wireOp",EDGE,"E910");
            var Q105;
            Q105=sQuery(id+"F14.wireOp",EDGE,"E637");
            var Q106;
            Q106=sQuery(id+"F14.wireOp",EDGE,"E607");
            var Q107;
            Q107=sQuery(id+"F14.wireOp",EDGE,"E639");
            var Q108;
            Q108=sQuery(id+"F14.wireOp",EDGE,"E781");
            var Q109;
            Q109=sQuery(id+"F14.wireOp",EDGE,"E783");
            var Q110;
            Q110=sQuery(id+"F14.wireOp",EDGE,"E909");
            var Q111;
            Q111=sQuery(id+"F14.wireOp",EDGE,"E622");
            var Q112;
            Q112=sQuery(id+"F14.wireOp",EDGE,"E606");
            var Q113;
            Q113=sQuery(id+"F14.wireOp",EDGE,"E638");
            var Q114;
            Q114=sQuery(id+"F14.wireOp",EDGE,"E654");
            var Q115;
            Q115=sQuery(id+"F14.wireOp",EDGE,"E608");
            var Q116;
            Q116=sQuery(id+"F14.wireOp",EDGE,"E672");
            var Q117;
            Q117=sQuery(id+"F14.wireOp",EDGE,"E656");
            var Q118;
            Q118=sQuery(id+"F14.wireOp",EDGE,"E640");
            var Q119;
            Q119=sQuery(id+"F14.wireOp",EDGE,"E784");
            var Q120;
            Q120=sQuery(id+"F14.wireOp",EDGE,"E642");
            var Q121;
            Q121=sQuery(id+"F14.wireOp",EDGE,"E626");
            var Q122;
            Q122=sQuery(id+"F14.wireOp",EDGE,"E610");
            var Q123;
            Q123=sQuery(id+"F14.wireOp",EDGE,"E674");
            var Q124;
            Q124=sQuery(id+"F14.wireOp",EDGE,"E899");
            var Q125;
            Q125=sQuery(id+"F14.wireOp",EDGE,"E625");
            var Q126;
            Q126=sQuery(id+"F14.wireOp",EDGE,"E609");
            var Q127;
            Q127=sQuery(id+"F14.wireOp",EDGE,"E641");
            var Q128;
            Q128=sQuery(id+"F14.wireOp",EDGE,"E785");
            var Q129;
            Q129=sQuery(id+"F14.wireOp",EDGE,"E779");
            var Q130;
            Q130=sQuery(id+"F14.wireOp",EDGE,"E659");
            var Q131;
            Q131=sQuery(id+"F14.wireOp",EDGE,"E649");
            var Q132;
            Q132=sQuery(id+"F14.wireOp",EDGE,"E643");
            var Q133;
            Q133=sQuery(id+"F14.wireOp",EDGE,"E627");
            var Q134;
            Q134=sQuery(id+"F14.wireOp",EDGE,"E611");
            var Q135;
            Q135=sQuery(id+"F14.wireOp",EDGE,"E787");
            var Q136;
            Q136=sQuery(id+"F14.wireOp",EDGE,"E786");
            var Q137;
            Q137=sQuery(id+"F14.wireOp",EDGE,"E914");
            var Q138;
            Q138=sQuery(id+"F14.wireOp",EDGE,"E778");
            var Q139;
            Q139=sQuery(id+"F14.wireOp",EDGE,"E725");
            var Q140;
            Q140=sQuery(id+"F14.wireOp",EDGE,"E886");
            var Q141;
            Q141=sQuery(id+"F14.wireOp",EDGE,"E854");
            var Q142;
            Q142=sQuery(id+"F14.wireOp",EDGE,"E726");
            var Q143;
            Q143=sQuery(id+"F14.wireOp",EDGE,"E727");
            var Q144;
            Q144=sQuery(id+"F14.wireOp",EDGE,"E907");
            var Q145;
            Q145=sQuery(id+"F14.wireOp",EDGE,"E636");
            var Q146;
            Q146=sQuery(id+"F14.wireOp",EDGE,"E732");
            var Q147;
            Q147=sQuery(id+"F14.wireOp",EDGE,"E892");
            var Q148;
            Q148=sQuery(id+"F14.wireOp",EDGE,"E766");
            var Q149;
            Q149=sQuery(id+"F14.wireOp",EDGE,"E894");
            var Q150;
            Q150=sQuery(id+"F14.wireOp",EDGE,"E749");
            var Q151;
            Q151=sQuery(id+"F14.wireOp",EDGE,"E733");
            var Q152;
            Q152=sQuery(id+"F14.wireOp",EDGE,"E765");
            var Q153;
            Q153=sQuery(id+"F14.wireOp",EDGE,"E861");
            var Q154;
            Q154=sQuery(id+"F14.wireOp",EDGE,"E893");
            var Q155;
            Q155=sQuery(id+"F14.wireOp",EDGE,"E750");
            var Q156;
            Q156=sQuery(id+"F14.wireOp",EDGE,"E734");
            var Q157;
            Q157=sQuery(id+"F14.wireOp",EDGE,"E915");
            var Q158;
            Q158=sQuery(id+"F14.wireOp",EDGE,"E753");
            var Q159;
            Q159=sQuery(id+"F14.wireOp",EDGE,"E897");
            var Q160;
            Q160=sQuery(id+"F14.wireOp",EDGE,"E913");
            var Q161;
            Q161=sQuery(id+"F14.wireOp",EDGE,"E754");
            var Q162;
            Q162=sQuery(id+"F14.wireOp",EDGE,"E898");
            var Q163;
            Q163=sQuery(id+"F14.wireOp",EDGE,"E731");
            var Q164;
            Q164=sQuery(id+"F14.wireOp",EDGE,"E762");
            var Q165;
            Q165=sQuery(id+"F14.wireOp",EDGE,"E874");
            var Q166;
            Q166=sQuery(id+"F14.wireOp",EDGE,"E772");
            var Q167;
            Q167=sQuery(id+"F14.wireOp",EDGE,"E792");
            var Q168;
            Q168=sQuery(id+"F14.wireOp",EDGE,"E841");
            var Q169;
            Q169=sQuery(id+"F14.wireOp",EDGE,"E904");
            var Q170;
            Q170=sQuery(id+"F14.wireOp",EDGE,"E744");
            var Q171;
            Q171=sQuery(id+"F14.wireOp",EDGE,"E776");
            var Q172;
            Q172=sQuery(id+"F14.wireOp",EDGE,"E756");
            var Q173;
            Q173=sQuery(id+"F14.wireOp",EDGE,"E696");
            var Q174;
            Q174=sQuery(id+"F14.wireOp",EDGE,"E868");
            var Q175;
            Q175=sQuery(id+"F14.wireOp",EDGE,"E872");
            var Q176;
            Q176=sQuery(id+"F14.wireOp",EDGE,"E743");
            var Q177;
            Q177=sQuery(id+"F14.wireOp",EDGE,"E788");
            var Q178;
            Q178=sQuery(id+"F14.wireOp",EDGE,"E745");
            var Q179;
            Q179=sQuery(id+"F14.wireOp",EDGE,"E905");
            var Q180;
            Q180=sQuery(id+"F14.wireOp",EDGE,"E761");
            var Q181;
            Q181=sQuery(id+"F14.wireOp",EDGE,"E760");
            var Q182;
            Q182=sQuery(id+"F14.wireOp",EDGE,"E681");
            var Q183;
            Q183=sQuery(id+"F14.wireOp",EDGE,"E712");
            var Q184;
            Q184=sQuery(id+"F14.wireOp",EDGE,"E855");
            var Q185;
            Q185=sQuery(id+"F14.wireOp",EDGE,"E709");
            var Q186;
            Q186=sQuery(id+"F14.wireOp",EDGE,"E853");
            var Q187;
            Q187=sQuery(id+"F14.wireOp",EDGE,"E741");
            var Q188;
            Q188=sQuery(id+"F14.wireOp",EDGE,"E885");
            var Q189;
            Q189=sQuery(id+"F14.wireOp",EDGE,"E740");
            var Q190;
            Q190=sQuery(id+"F14.wireOp",EDGE,"E757");
            var Q191;
            Q191=sQuery(id+"F14.wireOp",EDGE,"E775");
            var Q192;
            Q192=sQuery(id+"F14.wireOp",EDGE,"E693");
            var Q193;
            Q193=sQuery(id+"F14.wireOp",EDGE,"E889");
            var Q194;
            Q194=sQuery(id+"F14.wireOp",EDGE,"E697");
            var Q195;
            Q195=sQuery(id+"F14.wireOp",EDGE,"E873");
            var Q196;
            Q196=sQuery(id+"F14.wireOp",EDGE,"E901");
            var Q197;
            Q197=sQuery(id+"F14.wireOp",EDGE,"E856");
            var Q198;
            Q198=sQuery(id+"F14.wireOp",EDGE,"E777");
            var Q199;
            Q199=sQuery(id+"F14.wireOp",EDGE,"E888");
            var Q200;
            Q200=sQuery(id+"F14.wireOp",EDGE,"E900");
            var Q201;
            Q201=sQuery(id+"F14.wireOp",EDGE,"E871");
            var Q202;
            Q202=sQuery(id+"F14.wireOp",EDGE,"E791");
            var Q203;
            Q203=sQuery(id+"F14.wireOp",EDGE,"E759");
            var Q204;
            Q204=sQuery(id+"F14.wireOp",EDGE,"E903");
            var Q205;
            Q205=sQuery(id+"F14.wireOp",EDGE,"E884");
            var Q206;
            Q206=sQuery(id+"F14.wireOp",EDGE,"E763");
            var Q207;
            Q207=sQuery(id+"F14.wireOp",EDGE,"E875");
            var Q208;
            Q208=sQuery(id+"F14.wireOp",EDGE,"E859");
            var Q209;
            Q209=sQuery(id+"F14.wireOp",EDGE,"E843");
            var Q210;
            Q210=sQuery(id+"F14.wireOp",EDGE,"E716");
            var Q211;
            Q211=sQuery(id+"F14.wireOp",EDGE,"E814");
            var Q212;
            Q212=sQuery(id+"F14.wireOp",EDGE,"E764");
            var Q213;
            Q213=sQuery(id+"F14.wireOp",EDGE,"E876");
            var Q214;
            Q214=sQuery(id+"F14.wireOp",EDGE,"E860");
            var Q215;
            Q215=sQuery(id+"F14.wireOp",EDGE,"E844");
            var Q216;
            Q216=sQuery(id+"F14.wireOp",EDGE,"E878");
            var Q217;
            Q217=sQuery(id+"F14.wireOp",EDGE,"E846");
            var Q218;
            Q218=sQuery(id+"F14.wireOp",EDGE,"E717");
            var Q219;
            Q219=sQuery(id+"F14.wireOp",EDGE,"E623");
            var Q220;
            Q220=sQuery(id+"F14.wireOp",EDGE,"E751");
            var Q221;
            Q221=sQuery(id+"F14.wireOp",EDGE,"E767");
            var Q222;
            Q222=sQuery(id+"F14.wireOp",EDGE,"E879");
            var Q223;
            Q223=sQuery(id+"F14.wireOp",EDGE,"E863");
            var Q224;
            Q224=sQuery(id+"F14.wireOp",EDGE,"E911");
            var Q225;
            Q225=sQuery(id+"F14.wireOp",EDGE,"E895");
            var Q226;
            Q226=sQuery(id+"F14.wireOp",EDGE,"E877");
            var Q227;
            Q227=sQuery(id+"F14.wireOp",EDGE,"E845");
            var Q228;
            Q228=sQuery(id+"F14.wireOp",EDGE,"E624");
            var Q229;
            Q229=sQuery(id+"F14.wireOp",EDGE,"E752");
            var Q230;
            Q230=sQuery(id+"F14.wireOp",EDGE,"E768");
            var Q231;
            Q231=sQuery(id+"F14.wireOp",EDGE,"E880");
            var Q232;
            Q232=sQuery(id+"F14.wireOp",EDGE,"E864");
            var Q233;
            Q233=sQuery(id+"F14.wireOp",EDGE,"E912");
            var Q234;
            Q234=sQuery(id+"F14.wireOp",EDGE,"E896");
            var Q235;
            Q235=sQuery(id+"F14.wireOp",EDGE,"E851");
            var Q236;
            Q236=sQuery(id+"F14.wireOp",EDGE,"E883");
            var Q237;
            Q237=sQuery(id+"F14.wireOp",EDGE,"E867");
            var Q238;
            Q238=sQuery(id+"F14.wireOp",EDGE,"E881");
            var Q239;
            Q239=sQuery(id+"F14.wireOp",EDGE,"E769");
            var Q240;
            Q240=sQuery(id+"F14.wireOp",EDGE,"E865");
            var Q241;
            Q241=sQuery(id+"F14.wireOp",EDGE,"E723");
            var Q242;
            Q242=sQuery(id+"F14.wireOp",EDGE,"E771");
            var Q243;
            Q243=sQuery(id+"F14.wireOp",EDGE,"E739");
            var Q244;
            Q244=sQuery(id+"F14.wireOp",EDGE,"E755");
            var Q245;
            Q245=sQuery(id+"F14.wireOp",EDGE,"E770");
            var Q246;
            Q246=sQuery(id+"F14.wireOp",EDGE,"E738");
            var Q247;
            Q247=sQuery(id+"F14.wireOp",EDGE,"E850");
            var Q248;
            Q248=sQuery(id+"F14.wireOp",EDGE,"E866");
            var Q249;
            Q249=sQuery(id+"F14.wireOp",EDGE,"E746");
            var Q250;
            Q250=sQuery(id+"F14.wireOp",EDGE,"E820");
            var Q251;
            Q251=sQuery(id+"F14.wireOp",EDGE,"E714");
            var Q252;
            Q252=sQuery(id+"F14.wireOp",EDGE,"E713");
            var Q253;
            Q253=sQuery(id+"F14.wireOp",EDGE,"E695");
            var Q254;
            Q254=sQuery(id+"F14.wireOp",EDGE,"E758");
            var Q255;
            Q255=sQuery(id+"F14.wireOp",EDGE,"E730");
            var Q256;
            Q256=sQuery(id+"F14.wireOp",EDGE,"E840");
            var Q257;
            Q257=sQuery(id+"F14.wireOp",EDGE,"E902");
            var Q258;
            Q258=sQuery(id+"F14.wireOp",EDGE,"E742");
            var Q259;
            Q259=sQuery(id+"F14.wireOp",EDGE,"E724");
            var Q260;
            Q260=sQuery(id+"F14.wireOp",EDGE,"E794");
            var Q261;
            Q261=sQuery(id+"F14.wireOp",EDGE,"E793");
            var Q262;
            Q262=sQuery(id+"F14.wireOp",EDGE,"E680");
            var Q263;
            Q263=sQuery(id+"F14.wireOp",EDGE,"E748");
            var Q264;
            Q264=sQuery(id+"F14.wireOp",EDGE,"E796");
            var Q265;
            Q265=sQuery(id+"F14.wireOp",EDGE,"E798");
            var Q266;
            Q266=sQuery(id+"F14.wireOp",EDGE,"E735");
            var Q267;
            Q267=sQuery(id+"F14.wireOp",EDGE,"E813");
            var Q268;
            Q268=sQuery(id+"F14.wireOp",EDGE,"E797");
            var Q269;
            Q269=sQuery(id+"F14.wireOp",EDGE,"E815");
            var Q270;
            Q270=sQuery(id+"F14.wireOp",EDGE,"E829");
            var Q271;
            Q271=sQuery(id+"F14.wireOp",EDGE,"E736");
            var Q272;
            Q272=sQuery(id+"F14.wireOp",EDGE,"E722");
            var Q273;
            Q273=sQuery(id+"F14.wireOp",EDGE,"E737");
            var Q274;
            Q274=sQuery(id+"F14.wireOp",EDGE,"E849");
            var Q275;
            Q275=sQuery(id+"F14.wireOp",EDGE,"E795");
            var Q276;
            Q276=sQuery(id+"F14.wireOp",EDGE,"E882");
            var Q277;
            Q277=sQuery(id+"F14.wireOp",EDGE,"E747");
            var Q278;
            Q278=sQuery(id+"F14.wireOp",EDGE,"E715");
            var Q279;
            Q279=sQuery(id+"F14.wireOp",EDGE,"E811");
            var Q280;
            Q280=sQuery(id+"F14.wireOp",EDGE,"E842");
            var Q281;
            Q281=sQuery(id+"F14.wireOp",EDGE,"E805");
            var Q282;
            Q282=sQuery(id+"F14.wireOp",EDGE,"E683");
            var Q283;
            Q283=sQuery(id+"F14.wireOp",EDGE,"E810");
            var Q284;
            Q284=sQuery(id+"F14.wireOp",EDGE,"E698");
            var Q285;
            Q285=sQuery(id+"F14.wireOp",EDGE,"E838");
            var Q286;
            Q286=sQuery(id+"F14.wireOp",EDGE,"E806");
            var Q287;
            Q287=sQuery(id+"F14.wireOp",EDGE,"E678");
            var Q288;
            Q288=sQuery(id+"F14.wireOp",EDGE,"E677");
            var Q289;
            Q289=sQuery(id+"F14.wireOp",EDGE,"E821");
            var Q290;
            Q290=sQuery(id+"F14.wireOp",EDGE,"E809");
            var Q291;
            Q291=sQuery(id+"F14.wireOp",EDGE,"E711");
            var Q292;
            Q292=sQuery(id+"F14.wireOp",EDGE,"E729");
            var Q293;
            Q293=sQuery(id+"F14.wireOp",EDGE,"E808");
            var Q294;
            Q294=sQuery(id+"F14.wireOp",EDGE,"E708");
            var Q295;
            Q295=sQuery(id+"F14.wireOp",EDGE,"E822");
            var Q296;
            Q296=sQuery(id+"F14.wireOp",EDGE,"E679");
            var Q297;
            Q297=sQuery(id+"F14.wireOp",EDGE,"E692");
            var Q298;
            Q298=sQuery(id+"F14.wireOp",EDGE,"E836");
            var Q299;
            Q299=sQuery(id+"F14.wireOp",EDGE,"E682");
            var Q300;
            Q300=sQuery(id+"F14.wireOp",EDGE,"E710");
            var Q301;
            Q301=sQuery(id+"F14.wireOp",EDGE,"E807");
            var Q302;
            Q302=sQuery(id+"F14.wireOp",EDGE,"E839");
            var Q303;
            Q303=sQuery(id+"F14.wireOp",EDGE,"E852");
            var Q304;
            Q304=sQuery(id+"F14.wireOp",EDGE,"E694");
            var Q305;
            Q305=sQuery(id+"F14.wireOp",EDGE,"E827");
            var Q306;
            Q306=sQuery(id+"F14.wireOp",EDGE,"E684");
            var Q307;
            Q307=sQuery(id+"F14.wireOp",EDGE,"E700");
            var Q308;
            Q308=sQuery(id+"F14.wireOp",EDGE,"E718");
            var Q309;
            Q309=sQuery(id+"F14.wireOp",EDGE,"E812");
            var Q310;
            Q310=sQuery(id+"F14.wireOp",EDGE,"E702");
            var Q311;
            Q311=sQuery(id+"F14.wireOp",EDGE,"E828");
            var Q312;
            Q312=sQuery(id+"F14.wireOp",EDGE,"E830");
            var Q313;
            Q313=sQuery(id+"F14.wireOp",EDGE,"E685");
            var Q314;
            Q314=sQuery(id+"F14.wireOp",EDGE,"E799");
            var Q315;
            Q315=sQuery(id+"F14.wireOp",EDGE,"E847");
            var Q316;
            Q316=sQuery(id+"F14.wireOp",EDGE,"E831");
            var Q317;
            Q317=sQuery(id+"F14.wireOp",EDGE,"E720");
            var Q318;
            Q318=sQuery(id+"F14.wireOp",EDGE,"E816");
            var Q319;
            Q319=sQuery(id+"F14.wireOp",EDGE,"E800");
            var Q320;
            Q320=sQuery(id+"F14.wireOp",EDGE,"E848");
            var Q321;
            Q321=sQuery(id+"F14.wireOp",EDGE,"E832");
            var Q322;
            Q322=sQuery(id+"F14.wireOp",EDGE,"E706");
            var Q323;
            Q323=sQuery(id+"F14.wireOp",EDGE,"E835");
            var Q324;
            Q324=sQuery(id+"F14.wireOp",EDGE,"E819");
            var Q325;
            Q325=sQuery(id+"F14.wireOp",EDGE,"E721");
            var Q326;
            Q326=sQuery(id+"F14.wireOp",EDGE,"E817");
            var Q327;
            Q327=sQuery(id+"F14.wireOp",EDGE,"E833");
            var Q328;
            Q328=sQuery(id+"F14.wireOp",EDGE,"E707");
            var Q329;
            Q329=sQuery(id+"F14.wireOp",EDGE,"E691");
            var Q330;
            Q330=sQuery(id+"F14.wireOp",EDGE,"E675");
            var Q331;
            Q331=sQuery(id+"F14.wireOp",EDGE,"E834");
            var Q332;
            Q332=sQuery(id+"F14.wireOp",EDGE,"E818");
            var Q333;
            Q333=sQuery(id+"F14.wireOp",EDGE,"E699");
            var Q334;
            Q334=sQuery(id+"F14.wireOp",EDGE,"E804");
            var Q335;
            Q335=sQuery(id+"F14.wireOp",EDGE,"E676");
            var Q336;
            Q336=sQuery(id+"F14.wireOp",EDGE,"E824");
            var Q337;
            Q337=sQuery(id+"F14.wireOp",EDGE,"E837");
            var Q338;
            Q338=sQuery(id+"F14.wireOp",EDGE,"E823");
            var Q339;
            Q339=sQuery(id+"F14.wireOp",EDGE,"E826");
            var Q340;
            Q340=sQuery(id+"F14.wireOp",EDGE,"E825");
            var Q341;
            Q341=sQuery(id+"F14.wireOp",EDGE,"E687");
            var Q342;
            Q342=sQuery(id+"F14.wireOp",EDGE,"E719");
            var Q343;
            Q343=sQuery(id+"F14.wireOp",EDGE,"E701");
            var Q344;
            Q344=sQuery(id+"F14.wireOp",EDGE,"E703");
            var Q345;
            Q345=sQuery(id+"F14.wireOp",EDGE,"E686");
            var Q346;
            Q346=sQuery(id+"F14.wireOp",EDGE,"E688");
            var Q347;
            Q347=sQuery(id+"F14.wireOp",EDGE,"E704");
            var Q348;
            Q348=sQuery(id+"F14.wireOp",EDGE,"E690");
            var Q349;
            Q349=sQuery(id+"F14.wireOp",EDGE,"E803");
            var Q350;
            Q350=sQuery(id+"F14.wireOp",EDGE,"E689");
            var Q351;
            Q351=sQuery(id+"F14.wireOp",EDGE,"E705");
            var Q352;
            Q352=sQuery(id+"F14.wireOp",EDGE,"E801");
            var Q353;
            Q353=sQuery(id+"F14.wireOp",EDGE,"E802");
            extrude(context, id + "F15", {"entities" : qUnion([Q0, Q1, Q2, Q3, Q4, Q5, Q6, Q7, Q8, Q9, Q10, Q11, Q12, Q13, Q14, Q15, Q16]), "operationType" : NewBodyOperationType.ADD, "surfaceEntities" : qUnion([Q17, Q18, Q19, Q20, Q21, Q22, Q23, Q24, Q25, Q26, Q27, Q28, Q29, Q30, Q31, Q32, Q33, Q34, Q35, Q36, Q37, Q38, Q39, Q40, Q41, Q42, Q43, Q44, Q45, Q46, Q47, Q48, Q49, Q50, Q51, Q52, Q53, Q54, Q55, Q56, Q57, Q58, Q59, Q60, Q61, Q62, Q63, Q64, Q65, Q66, Q67, Q68, Q69, Q70, Q71, Q72, Q73, Q74, Q75, Q76, Q77, Q78, Q79, Q80, Q81, Q82, Q83, Q84, Q85, Q86, Q87, Q88, Q89, Q90, Q91, Q92, Q93, Q94, Q95, Q96, Q97, Q98, Q99, Q100, Q101, Q102, Q103, Q104, Q105, Q106, Q107, Q108, Q109, Q110, Q111, Q112, Q113, Q114, Q115, Q116, Q117, Q118, Q119, Q120, Q121, Q122, Q123, Q124, Q125, Q126, Q127, Q128, Q129, Q130, Q131, Q132, Q133, Q134, Q135, Q136, Q137, Q138, Q139, Q140, Q141, Q142, Q143, Q144, Q145, Q146, Q147, Q148, Q149, Q150, Q151, Q152, Q153, Q154, Q155, Q156, Q157, Q158, Q159, Q160, Q161, Q162, Q163, Q164, Q165, Q166, Q167, Q168, Q169, Q170, Q171, Q172, Q173, Q174, Q175, Q176, Q177, Q178, Q179, Q180, Q181, Q182, Q183, Q184, Q185, Q186, Q187, Q188, Q189, Q190, Q191, Q192, Q193, Q194, Q195, Q196, Q197, Q198, Q199, Q200, Q201, Q202, Q203, Q204, Q205, Q206, Q207, Q208, Q209, Q210, Q211, Q212, Q213, Q214, Q215, Q216, Q217, Q218, Q219, Q220, Q221, Q222, Q223, Q224, Q225, Q226, Q227, Q228, Q229, Q230, Q231, Q232, Q233, Q234, Q235, Q236, Q237, Q238, Q239, Q240, Q241, Q242, Q243, Q244, Q245, Q246, Q247, Q248, Q249, Q250, Q251, Q252, Q253, Q254, Q255, Q256, Q257, Q258, Q259, Q260, Q261, Q262, Q263, Q264, Q265, Q266, Q267, Q268, Q269, Q270, Q271, Q272, Q273, Q274, Q275, Q276, Q277, Q278, Q279, Q280, Q281, Q282, Q283, Q284, Q285, Q286, Q287, Q288, Q289, Q290, Q291, Q292, Q293, Q294, Q295, Q296, Q297, Q298, Q299, Q300, Q301, Q302, Q303, Q304, Q305, Q306, Q307, Q308, Q309, Q310, Q311, Q312, Q313, Q314, Q315, Q316, Q317, Q318, Q319, Q320, Q321, Q322, Q323, Q324, Q325, Q326, Q327, Q328, Q329, Q330, Q331, Q332, Q333, Q334, Q335, Q336, Q337, Q338, Q339, Q340, Q341, Q342, Q343, Q344, Q345, Q346, Q347, Q348, Q349, Q350, Q351, Q352, Q353]), "depth" : 1.8 * mm});
        }
    });
